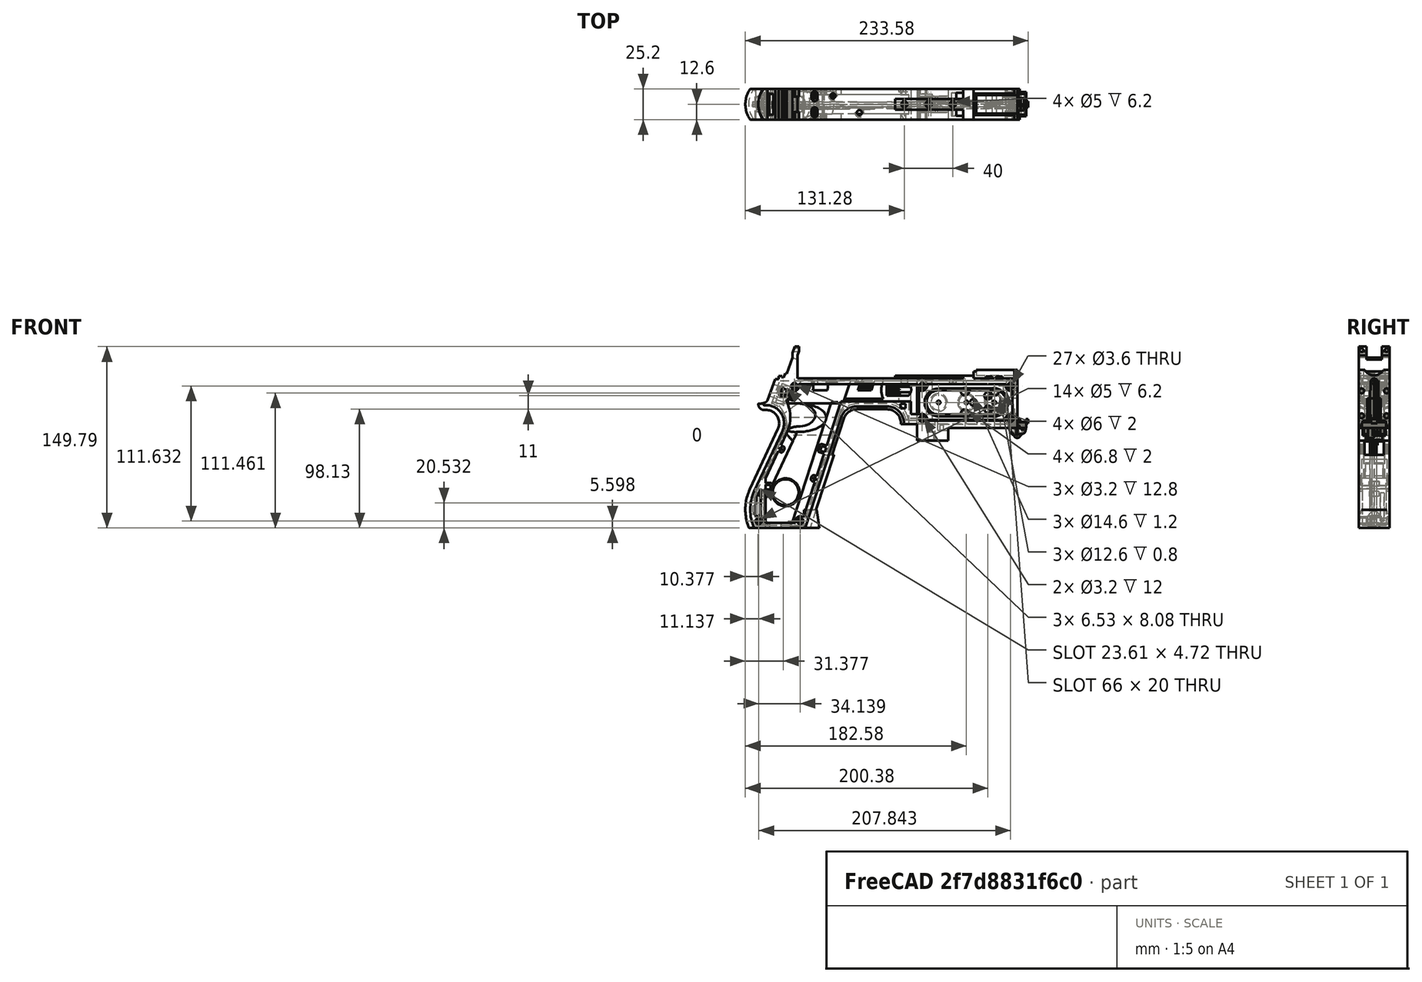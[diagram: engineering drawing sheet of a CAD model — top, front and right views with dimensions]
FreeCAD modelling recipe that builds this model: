
FCSTD DOCUMENT  (FreeCAD 1.0R39319 (Git))
Label: PICON-OF_ver_32
License: All rights reserved
LicenseURL: https://en.wikipedia.org/wiki/All_rights_reserved
objects: Sketcher::SketchObject×119, Part::Extrusion×75, Part::Cut×47, PartDesign::Pad×19, PartDesign::Chamfer×13, PartDesign::Pocket×12, PartDesign::Fillet×9, PartDesign::Body×8, Part::MultiFuse×6, PartDesign::SubtractivePipe×4, PartDesign::SubtractiveLoft×4, PartDesign::Plane×2, PartDesign::SubShapeBinder×2, Part::Part2DObjectPython×2, Part::Sweep×1, PartDesign::ShapeBinder×1, PartDesign::FeatureBase×1, Part::Cone×1, Part::Chamfer×1, Part::Mirroring×1, +1 more types
note: 570 computed .brp shape members not serialized (recipe doc carries the construction recipe); baked Part::Feature solids carry a one-line shape summary decoded from their .brp

FEATURE [Sketcher::SketchObject] Sketch  label="corpo principale"
  ArcFitTolerance = 1e-06
  AttacherType = Attacher::AttachEngine3D
  AttachmentSupport = -> [XZ_Plane]
  FullyConstrained = true
  MakeInternals = false
  MapMode = 5
  Placement = pos=(0,0,0) rot=(1,0,0;1.5708rad)
  sketch-geometry (65):
    g0: LineSegment StartX=0 StartY=0 StartZ=0 EndX=-57.2 EndY=0 EndZ=0
    g1: LineSegment StartX=-57.2 StartY=0 StartZ=0 EndX=-57.2 EndY=-10.4 EndZ=0
    g2: LineSegment StartX=-57.2 StartY=-10.4 StartZ=0 EndX=-82.8 EndY=-10.4 EndZ=0
    g3: LineSegment StartX=-82.8 StartY=-10.4 StartZ=0 EndX=-82.8 EndY=3.2 EndZ=0
    g4: LineSegment StartX=-82.8 StartY=3.2 StartZ=0 EndX=-93.6 EndY=3.2 EndZ=0
    g5: LineSegment StartX=-93.6 StartY=3.2 StartZ=0 EndX=-93.6 EndY=4 EndZ=0
    g6: LineSegment StartX=-107.6 StartY=18 StartZ=0 EndX=-132.428 EndY=18 EndZ=0
    g7: LineSegment StartX=-145.743 StartY=8.32624 StartZ=0 EndX=-175.232 EndY=-82.4316 EndZ=0
    g8: LineSegment StartX=-175.232 StartY=-82.4316 StartZ=0 EndX=-217.232 EndY=-82.4316 EndZ=0
    g9: LineSegment StartX=-217.232 StartY=-52.1862 StartZ=0 EndX=-193.988 EndY=-2.33927 EndZ=0
    g10: LineSegment StartX=-206.196 StartY=23.0857 StartZ=0 EndX=-199.861 EndY=40.4914 EndZ=0
    g11: LineSegment StartX=-199.861 StartY=40.4914 StartZ=0 EndX=-197.061 EndY=40.4914 EndZ=0
    g12: LineSegment StartX=-197.061 StartY=40.4914 StartZ=0 EndX=-197.061 EndY=42.8914 EndZ=0
    g13: LineSegment StartX=-197.061 StartY=42.8914 StartZ=0 EndX=-194.261 EndY=42.8914 EndZ=0
    g14: LineSegment StartX=-194.261 StartY=42.8914 StartZ=0 EndX=-194.535 EndY=42.1397 EndZ=0
    g15: LineSegment StartX=-194.535 StartY=42.1397 StartZ=0 EndX=-193.031 EndY=41.5924 EndZ=0
    g16: LineSegment StartX=-193.031 StartY=41.5924 StartZ=0 EndX=-191.663 EndY=45.3512 EndZ=0
    g17: LineSegment StartX=-191.663 StartY=45.3512 StartZ=0 EndX=-190.536 EndY=44.9408 EndZ=0
    g18: LineSegment StartX=-190.536 StartY=44.9408 StartZ=0 EndX=-185.747 EndY=58.0965 EndZ=0
    g19: LineSegment StartX=-185.747 StartY=58.0965 StartZ=0 EndX=-185.747 EndY=62.0965 EndZ=0
    g20: LineSegment StartX=-185.747 StartY=62.0965 StartZ=0 EndX=-183.832 EndY=67.3588 EndZ=0
    g21: LineSegment StartX=-183.832 StartY=67.3588 StartZ=0 EndX=-180.232 EndY=67.3588 EndZ=0
    g22: LineSegment StartX=-180.232 StartY=67.3588 StartZ=0 EndX=-180.232 EndY=63.7588 EndZ=0
    g23: LineSegment StartX=-180.232 StartY=63.7588 StartZ=0 EndX=-181.6 EndY=60 EndZ=0
    g24: LineSegment StartX=-181.6 StartY=60 StartZ=0 EndX=-181.6 EndY=41.2 EndZ=0
    g25: LineSegment StartX=-181.6 StartY=41.2 StartZ=0 EndX=-100.8 EndY=41.2 EndZ=0
    g26: LineSegment StartX=-36 StartY=43.2 StartZ=0 EndX=-36 EndY=41.2 EndZ=0
    g27: LineSegment StartX=0 StartY=48 StartZ=0 EndX=0 EndY=0 EndZ=0
    g28: LineSegment StartX=-209.901 StartY=19.85 StartZ=0 EndX=-209.901 EndY=20.1 EndZ=0
    g29: LineSegment StartX=-208.001 StartY=22 StartZ=0 EndX=-207.747 EndY=22 EndZ=0
    g30: LineSegment StartX=-207.583 StartY=19 StartZ=0 EndX=-209.051 EndY=19 EndZ=0
    g31: ArcOfCircle CenterX=-208.001 CenterY=20.1 CenterZ=0 NormalX=0 NormalY=0 NormalZ=1 AngleXU=0 Radius=1.9 StartAngle=1.5708 EndAngle=3.14159
    g32: GeomPoint [constr] X=-209.901 Y=22 Z=0
    g33: ArcOfCircle CenterX=-209.051 CenterY=19.85 CenterZ=0 NormalX=0 NormalY=0 NormalZ=1 AngleXU=0 Radius=0.85 StartAngle=3.14159 EndAngle=4.71239
    g34: GeomPoint [constr] X=-209.901 Y=19 Z=0
    g35: ArcOfCircle CenterX=-207.747 CenterY=23.65 CenterZ=0 NormalX=0 NormalY=0 NormalZ=1 AngleXU=0 Radius=1.65 StartAngle=4.71239 EndAngle=5.93412
    g36: GeomPoint [constr] X=-206.591 Y=22 Z=0
    g37: LineSegment StartX=-4 StartY=6 StartZ=0 EndX=-4 EndY=36.4 EndZ=0
    g38: LineSegment StartX=-4 StartY=36.4 StartZ=0 EndX=-185.2 EndY=36.4 EndZ=0
    g39: LineSegment StartX=-185.2 StartY=36.4 StartZ=0 EndX=-190.441 EndY=22 EndZ=0
    g40: LineSegment StartX=-214.575 StartY=-78.4316 StartZ=0 EndX=-178.142 EndY=-78.4316 EndZ=0
    g41: LineSegment StartX=-178.142 StartY=-78.4316 StartZ=0 EndX=-145.51 EndY=22 EndZ=0
    g42: LineSegment StartX=-145.51 StartY=22 StartZ=0 EndX=-87.91 EndY=22 EndZ=0
    g43: LineSegment StartX=-87.91 StartY=22 StartZ=0 EndX=-87.91 EndY=11.6 EndZ=0
    g44: LineSegment StartX=-87.91 StartY=11.6 StartZ=0 EndX=-80.11 EndY=11.6 EndZ=0
    g45: LineSegment StartX=-80.11 StartY=11.6 StartZ=0 EndX=-80.11 EndY=6 EndZ=0
    g46: LineSegment StartX=-80.11 StartY=6 StartZ=0 EndX=-4 EndY=6 EndZ=0
    g47: LineSegment StartX=-190.363 StartY=-4.02975 StartZ=0 EndX=-213.607 EndY=-53.8767 EndZ=0
    g48: ArcOfCircle CenterX=-132.428 CenterY=4 CenterZ=0 NormalX=0 NormalY=0 NormalZ=1 AngleXU=0 Radius=14 StartAngle=1.5708 EndAngle=2.82743
    g49: GeomPoint [constr] X=-142.6 Y=18 Z=0
    g50: ArcOfCircle CenterX=-107.6 CenterY=4 CenterZ=0 NormalX=0 NormalY=0 NormalZ=1 AngleXU=0 Radius=14 StartAngle=0 EndAngle=1.5708
    g51: GeomPoint [constr] X=-93.6 Y=18 Z=0
    g52: ArcOfCircle CenterX=-184.801 CenterY=-67.3089 CenterZ=0 NormalX=0 NormalY=0 NormalZ=1 AngleXU=0 Radius=35.7833 StartAngle=2.70526 EndAngle=3.57792
    g53: ArcOfCircle CenterX=-207.583 CenterY=4 CenterZ=0 NormalX=0 NormalY=0 NormalZ=1 AngleXU=0 Radius=15 StartAngle=5.84685 EndAngle=7.85398
    g54: LineSegment [constr] StartX=-213.607 StartY=-53.8767 StartZ=0 EndX=-217.232 EndY=-52.1862 EndZ=0
    g55: ArcOfCircle CenterX=-184.801 CenterY=-67.3089 CenterZ=0 NormalX=0 NormalY=0 NormalZ=1 AngleXU=0 Radius=31.7833 StartAngle=2.70526 EndAngle=3.49911
    g56: ArcOfCircle CenterX=-218.095 CenterY=8.90192 CenterZ=0 NormalX=0 NormalY=0 NormalZ=1 AngleXU=0 Radius=30.5989 StartAngle=5.84685 EndAngle=6.72553
    g57: LineSegment StartX=-44.6 StartY=43.2 StartZ=0 EndX=-36 EndY=43.2 EndZ=0
    g58: LineSegment StartX=-100.8 StartY=41.2 StartZ=0 EndX=-44.6 EndY=41.2 EndZ=0
    g59: LineSegment StartX=-44.6 StartY=41.2 StartZ=0 EndX=-44.6 EndY=43.2 EndZ=0
    g60: LineSegment StartX=-2.4 StartY=48 StartZ=0 EndX=0 EndY=48 EndZ=0
    g61: LineSegment StartX=-36 StartY=41.2 StartZ=0 EndX=-2.4 EndY=41.2 EndZ=0
    g62: LineSegment StartX=-2.4 StartY=41.2 StartZ=0 EndX=-2.4 EndY=48 EndZ=0
    g63: LineSegment [constr] StartX=-181.6 StartY=36.4 StartZ=0 EndX=-152.209 EndY=36.4 EndZ=0
    g64: LineSegment [constr] StartX=-181.6 StartY=36.4 StartZ=0 EndX=-130.41 EndY=36.4 EndZ=0
  constraints (183):
    c: Coincident(g-1,g0)
    c: PointOnObject(g0,g-1)
    c: Coincident(g0,g1)
    c: Vertical(g1)
    c: Coincident(g1,g2)
    c: Horizontal(g2)
    c: Coincident(g2,g3)
    c: Vertical(g3)
    c: Coincident(g3,g4)
    c: Coincident(g4,g5)
    c: Vertical(g5)
    c: Horizontal(g6)
    c: Coincident(g7,g8)
    c: Horizontal(g8)
    c: Coincident(g10,g11)
    c: Horizontal(g11)
    c: Coincident(g11,g12)
    c: Vertical(g12)
    c: Coincident(g12,g13)
    c: Horizontal(g13)
    c: Coincident(g13,g14)
    c: Coincident(g14,g15)
    c: Coincident(g15,g16)
    c: Coincident(g16,g17)
    c: Coincident(g17,g18)
    c: Coincident(g18,g19)
    c: Vertical(g19)
    c: Coincident(g19,g20)
    c: Coincident(g20,g21)
    c: Horizontal(g21)
    c: Coincident(g21,g22)
    c: Vertical(g22)
    c: Coincident(g22,g23)
    c: Coincident(g23,g24)
    c: Vertical(g24)
    c: Coincident(g24,g25)
    c: Horizontal(g25)
    c: Coincident(g57,g26)
    c: Vertical(g26)
    c: Coincident(g26,g61)
    c: PointOnObject(g60,g-2)
    c: Coincident(g60,g27)
    c: Coincident(g27,g0)
    c: DistanceY(g27,g27) = 48
    c: DistanceY(g1,g1) = 10.4
    c: DistanceX(g0,g0) = 57.2
    c: DistanceX(g2,g2) = 25.6
    c: Horizontal(g4)
    c: DistanceY(g3,g3) = 13.6
    c: DistanceX(g4,g4) = 10.8
    c: DistanceY(g5,g51) = 14.8
    c: DistanceX(g49,g51) = 49
    c: Distance(g7,g49) = 105.6
    c: DistanceX(g61,g60) = 36
    c: DistanceX(g25,g25) = 80.8
    c: DistanceY(g24,g24) = 18.8
    c: DistanceY(g22,g22) = 3.6
    c: Distance(g23) = 4
    c: Angle(g-1,g23) = 1.22173
    c: DistanceX(g21,g21) = 3.6
    c: Distance(g20) = 5.6
    c: Angle(g-1,g20) = 1.22173
    c: DistanceY(g19,g19) = 4
    c: Distance(g18) = 14
    c: Angle(g-1,g18) = 1.22173
    c: Distance(g17) = 1.2
    c: Distance(g16) = 4
    c: Angle(g16) = 1.22173
    c: Perpendicular(g18,g17)
    c: Distance(g15) = 1.6
    c: Perpendicular(g16,g15)
    c: Distance(g14) = 0.8
    c: DistanceX(g13,g13) = 2.8
    c: Perpendicular(g15,g14)
    c: DistanceY(g12,g12) = 2.4
    c: DistanceX(g11,g11) = 2.8
    c: Distance(g9) = 55
    c: Angle(g9,g-1) = 2.00713
    c: Horizontal(g29)
    c: Vertical(g28)
    c: Horizontal(g30)
    c: PointOnObject(g32,g29)
    c: PointOnObject(g32,g28)
    c: Tangent(g29,g31) = 1.5708
    c: Tangent(g28,g31) = 1.5708
    c: PointOnObject(g34,g28)
    c: PointOnObject(g34,g30)
    c: Tangent(g28,g33) = 1.5708
    c: Tangent(g30,g33) = 1.5708
    c: PointOnObject(g36,g29)
    c: PointOnObject(g36,g10)
    c: Tangent(g29,g35) = -1.5708
    c: Tangent(g10,g35) = -1.5708
    c: Angle(g-1,g10) = 1.22173
    c: Radius(g35) = 1.65
    c: Vertical(g37)
    c: Coincident(g37,g38)
    c: Horizontal(g38)
    c: Coincident(g38,g39)
    c: Horizontal(g40)
    c: Coincident(g40,g41)
    c: Coincident(g41,g42)
    c: Horizontal(g42)
    c: Coincident(g42,g43)
    c: Vertical(g43)
    c: Coincident(g43,g44)
    c: Horizontal(g44)
    c: Coincident(g44,g45)
    c: Vertical(g45)
    c: Coincident(g45,g46)
    c: Coincident(g46,g37)
    c: Horizontal(g46)
    c: DistanceY(g0,g37) = 6
    c: DistanceX(g37,g0) = 4
    c: DistanceY(g37,g25) = 4.8
    c: DistanceX(g38,g38) = 181.2
    c: DistanceX(g42,g42) = 57.6
    c: DistanceY(g49,g41) = 4
    c: DistanceX(g41,g49) = 2.91
    c: DistanceY(g43,g43) = 10.4
    c: DistanceX(g44,g44) = 7.8
    c: DistanceY(g7,g40) = 4
    c: Distance(g47) = 55
    c: Angle(g-1,g39) = 1.22173
    c: PointOnObject(g49,g7)
    c: PointOnObject(g49,g6)
    c: Tangent(g7,g48) = -1.5708
    c: Tangent(g6,g48) = -1.5708
    c: PointOnObject(g51,g5)
    c: PointOnObject(g51,g6)
    c: Tangent(g5,g50) = -1.5708
    c: Tangent(g6,g50) = -1.5708
    c: Radius(g50) = 14
    c: Radius(g48) = 14
    c: DistanceX(g8,g8) = 42
    c: Angle(g7,g-1) = 1.88496
    c: Parallel(g41,g7)
    c: Parallel(g47,g9)
    c: Coincident(g52,g8)
    c: Tangent(g52,g9) = 1.5708
    c: DistanceX(g9,g8) = 0
    c: Tangent(g53,g9) = -1.5708
    c: Tangent(g53,g30) = -1.5708
    c: Diameter(g53) = 30
    c: DistanceY(g53,g0) = -4
    c: Coincident(g54,g47)
    c: Distance(g54) = 4
    c: Coincident(g54,g9)
    c: Coincident(g55,g40)
    c: Tangent(g55,g47) = -1.5708
    c: Coincident(g52,g55)
    c: Coincident(g56,g39)
    c: Tangent(g56,g47) = 1.5708
    c: Horizontal(g57)
    c: DistanceX(g57,g57) = 8.6
    c: Coincident(g58,g25)
    c: Horizontal(g58)
    c: Coincident(g59,g58)
    c: Vertical(g59)
    c: DistanceY(g58,g57) = 2
    c: DistanceX(g58,g58) = 56.2
    c: Coincident(g59,g57)
    c: DistanceY(g41,g36) = 0
    c: DistanceY(g36,g39) = 0
    c: DistanceY(g28,g28) = 0.25
    c: DistanceX(g30,g36) = 2.46
    c: DistanceX(g28,g29) = 1.9
    c: Coincident(g62,g60)
    c: Horizontal(g60)
    c: DistanceX(g62,g27) = 2.4
    c: Coincident(g61,g62)
    c: DistanceY(g26,g26) = 2
    c: Vertical(g62)
    c: DistanceY(g61,g60) = 6.8
    c: Horizontal(g61)
    c: Distance(g63) = 29.391
    c: PointOnObject(g63,g38)
    c: PointOnObject(g63,g38)
    c: Distance(g64) = 51.19
    c: PointOnObject(g64,g38)
    c: PointOnObject(g64,g38)
    c: DistanceX(g24,g63) = 0
    c: DistanceX(g24,g64) = 0
FEATURE [Part::Extrusion] Extrude  label="Extrude corpo principale"
  Base = -> Sketch
  Dir = (0,-1,2e-16)
  DirMode = 2
  FaceMakerClass = Part::FaceMakerBullseye
  FaceMakerMode = 3
  LengthFwd = 25.2
  LengthRev = 12.6
  Solid = true
  Symmetric = true
FEATURE [Sketcher::SketchObject] Sketch002  label="scavo grilletto"
  ArcFitTolerance = 1e-06
  AttachmentSupport = -> [XZ_Plane]
  ExternalGeometry = -> [Sketch]
  FullyConstrained = true
  MakeInternals = false
  MapMode = 5
  Placement = pos=(0,0,0) rot=(1,0,0;1.5708rad)
  sketch-geometry (4):
    g0: LineSegment StartX=-89.51 StartY=22 StartZ=0 EndX=-152.71 EndY=22 EndZ=0
    g1: LineSegment StartX=-152.71 StartY=22 StartZ=0 EndX=-167.006 EndY=-22 EndZ=0
    g2: LineSegment StartX=-167.006 StartY=-22 StartZ=0 EndX=-89.51 EndY=-22 EndZ=0
    g3: LineSegment StartX=-89.51 StartY=-22 StartZ=0 EndX=-89.51 EndY=22 EndZ=0
  constraints (12):
    c: Horizontal(g0)
    c: Coincident(g0,g1)
    c: Coincident(g1,g2)
    c: Horizontal(g2)
    c: Coincident(g2,g3)
    c: Coincident(g3,g0)
    c: Vertical(g3)
    c: Angle(g1,g0) = 1.88496
    c: DistanceY(g3,g3) = 44
    c: DistanceX(g0,g0) = 63.2
    c: DistanceX(g0,g-3) = 1.6
    c: DistanceY(g-3,g0) = 0
FEATURE [Sketcher::SketchObject] Sketch004  label="traiettoria arrotondamento impugnatura anteriore"
  ArcFitTolerance = 1e-06
  AttachmentSupport = -> [XZ_Plane]
  ExternalGeometry = -> [Sketch]
  FullyConstrained = true
  MakeInternals = false
  MapMode = 5
  Placement = pos=(0,0,0) rot=(1,0,0;1.5708rad)
  sketch-geometry (13):
    g0: LineSegment StartX=-175.232 StartY=-82.4316 StartZ=0 EndX=-145.743 EndY=8.32624 EndZ=0
    g1: LineSegment StartX=-93.6 StartY=3.2 StartZ=0 EndX=-93.6 EndY=4 EndZ=0
    g2: LineSegment StartX=-132.428 StartY=18 StartZ=0 EndX=-107.6 EndY=18 EndZ=0
    g3: ArcOfCircle CenterX=-132.428 CenterY=4 CenterZ=0 NormalX=0 NormalY=0 NormalZ=1 AngleXU=0 Radius=14 StartAngle=1.5708 EndAngle=2.82743
    g4: ArcOfCircle CenterX=-107.6 CenterY=4 CenterZ=0 NormalX=0 NormalY=0 NormalZ=1 AngleXU=0 Radius=14 StartAngle=0 EndAngle=1.5708
    g5: LineSegment StartX=-175.232 StartY=-82.4316 StartZ=0 EndX=-217.232 EndY=-82.4316 EndZ=0
    g6: LineSegment StartX=-217.232 StartY=-52.1862 StartZ=0 EndX=-193.988 EndY=-2.33927 EndZ=0
    g7: LineSegment StartX=-209.051 StartY=19 StartZ=0 EndX=-207.583 EndY=19 EndZ=0
    g8: LineSegment StartX=-209.901 StartY=20.1 StartZ=0 EndX=-209.901 EndY=19.85 EndZ=0
    g9: ArcOfCircle CenterX=-184.801 CenterY=-67.3089 CenterZ=0 NormalX=0 NormalY=0 NormalZ=1 AngleXU=0 Radius=35.7833 StartAngle=2.70526 EndAngle=3.57792
    g10: ArcOfCircle CenterX=-207.583 CenterY=4 CenterZ=0 NormalX=0 NormalY=0 NormalZ=1 AngleXU=0 Radius=15 StartAngle=5.84685 EndAngle=7.85398
    g11: ArcOfCircle CenterX=-209.051 CenterY=19.85 CenterZ=0 NormalX=0 NormalY=0 NormalZ=1 AngleXU=0 Radius=0.85 StartAngle=3.14159 EndAngle=4.71239
    g12: ArcOfCircle CenterX=-208.001 CenterY=20.1 CenterZ=0 NormalX=0 NormalY=0 NormalZ=1 AngleXU=0 Radius=1.9 StartAngle=1.5708 EndAngle=3.14159
  constraints (26):
    c: Coincident(g0,g-3)
    c: Coincident(g0,g-6)
    c: Coincident(g1,g-8)
    c: Coincident(g1,g-7)
    c: Coincident(g2,g-5)
    c: Coincident(g2,g-4)
    c: Coincident(g3,g2)
    c: Tangent(g3,g0) = 1.5708
    c: Coincident(g4,g1)
    c: Tangent(g4,g2) = 1.5708
    c: Coincident(g5,g0)
    c: Coincident(g5,g-9)
    c: Coincident(g6,g-12)
    c: Coincident(g6,g-11)
    c: Coincident(g7,g-15)
    c: Coincident(g7,g-14)
    c: Coincident(g8,g-16)
    c: Coincident(g8,g-17)
    c: Tangent(g9,g6) = 1.5708
    c: Coincident(g9,g5)
    c: Coincident(g10,g7)
    c: Tangent(g10,g6) = -1.5708
    c: Tangent(g11,g7) = -1.5708
    c: Coincident(g11,g8)
    c: Tangent(g12,g8) = -1.5708
    c: Coincident(g12,g-17)
FEATURE [PartDesign::Plane] DatumPlane  label="Piano per disegno arrotondamento impugnatura"
  AttachmentSupport = -> [Sketch]
  Length = 68.5841
  MapMode = 7
  Placement = pos=(-145.743,1.8e-15,8.32624) rot=(0.154555,0.154555,0.97582;1.59527rad)
  ResizeMode = 0
  Width = 191.269
FEATURE [Sketcher::SketchObject] Sketch005  label="forma arrotondamento impugnatura anteriore"
  ArcFitTolerance = 1e-06
  AttachmentSupport = -> [DatumPlane]
  FullyConstrained = true
  MakeInternals = false
  MapMode = 5
  Placement = pos=(-145.743,1.8e-15,8.32624) rot=(0.154555,0.154555,0.97582;1.59527rad)
  sketch-geometry (5):
    g0: GeomPoint [constr] X=0 Y=-4 Z=0
    g1: GeomPoint [constr] X=-12.6 Y=7.1e-15 Z=0
    g2: GeomPoint [constr] X=12.6 Y=4.97e-14 Z=0
    g3: LineSegment StartX=-12.6 StartY=7.1e-15 StartZ=0 EndX=12.6 EndY=4.97e-14 EndZ=0
    g4: ArcOfCircle CenterX=-3.88e-14 CenterY=17.845 CenterZ=0 NormalX=0 NormalY=0 NormalZ=1 AngleXU=0 Radius=21.845 StartAngle=4.09759 EndAngle=5.32718
  constraints (11):
    c: DistanceY(g0,g-1) = 4
    c: DistanceX(g-1,g0) = 0
    c: DistanceX(g1,g-1) = 12.6
    c: DistanceX(g-1,g2) = 12.6
    c: DistanceY(g-1,g2) = 0
    c: DistanceY(g-1,g1) = 0
    c: Coincident(g3,g1)
    c: Coincident(g3,g2)
    c: Coincident(g4,g1)
    c: Coincident(g4,g2)
    c: PointOnObject(g0,g4)
FEATURE [Part::Sweep] Sweep  label="Sweep impugnatura"
  Frenet = true
  Sections = -> [Sketch005]
  Solid = true
  Spine = -> Sketch [Edge32,Edge33,Edge34,Edge35,Edge36,Edge37,Edge38,Edge39,Edge40,Edge41,Edge42,Edge43,Edge44]
  Transition = 1
FEATURE [Sketcher::SketchObject] Sketch008  label="buchi e pulizie varie"
  ArcFitTolerance = 1e-06
  AttachmentSupport = -> [XZ_Plane]
  ExternalGeometry = -> [Sketch]
  FullyConstrained = true
  MakeInternals = false
  MapMode = 5
  Placement = pos=(0,0,0) rot=(1,0,0;1.5708rad)
  sketch-geometry (26):
    g0: LineSegment StartX=-96.278 StartY=20.155 StartZ=0 EndX=-92.278 EndY=20.155 EndZ=0
    g1: LineSegment StartX=-92.278 StartY=20.155 StartZ=0 EndX=-92.278 EndY=16.155 EndZ=0
    g2: LineSegment StartX=-92.278 StartY=16.155 StartZ=0 EndX=-96.278 EndY=16.155 EndZ=0
    g3: LineSegment StartX=-96.278 StartY=16.155 StartZ=0 EndX=-96.278 EndY=20.155 EndZ=0
    g4: LineSegment StartX=-222.232 StartY=-82.4316 StartZ=0 EndX=-170.232 EndY=-82.4316 EndZ=0
    g5: LineSegment StartX=-170.232 StartY=-82.4316 StartZ=0 EndX=-170.232 EndY=-86.4316 EndZ=0
    g6: LineSegment StartX=-170.232 StartY=-86.4316 StartZ=0 EndX=-222.232 EndY=-86.4316 EndZ=0
    g7: LineSegment StartX=-222.232 StartY=-86.4316 StartZ=0 EndX=-222.232 EndY=-82.4316 EndZ=0
    g8: LineSegment StartX=-213.901 StartY=20.1 StartZ=0 EndX=-213.901 EndY=26 EndZ=0
    g9: LineSegment StartX=-213.901 StartY=26 StartZ=0 EndX=-206.196 EndY=26 EndZ=0
    g10: LineSegment StartX=-17.4 StartY=42.8 StartZ=0 EndX=-12.4 EndY=42.8 EndZ=0
    g11: LineSegment StartX=-12.4 StartY=42.8 StartZ=0 EndX=-12.4 EndY=41.2 EndZ=0
    g12: LineSegment StartX=-12.4 StartY=41.2 StartZ=0 EndX=-17.4 EndY=41.2 EndZ=0
    g13: LineSegment StartX=-17.4 StartY=41.2 StartZ=0 EndX=-17.4 EndY=42.8 EndZ=0
    g14: LineSegment StartX=-25.9 StartY=42.8 StartZ=0 EndX=-20.9 EndY=42.8 EndZ=0
    g15: LineSegment StartX=-20.9 StartY=42.8 StartZ=0 EndX=-20.9 EndY=41.2 EndZ=0
    g16: LineSegment StartX=-20.9 StartY=41.2 StartZ=0 EndX=-25.9 EndY=41.2 EndZ=0
    g17: LineSegment StartX=-25.9 StartY=41.2 StartZ=0 EndX=-25.9 EndY=42.8 EndZ=0
    g18: GeomPoint [constr] X=-206.196 Y=23.0857 Z=0
    g19: GeomPoint [constr] X=-213.901 Y=20.1 Z=0
    g20: BSplineCurve PolesCount=4 KnotsCount=2 Degree=3 IsPeriodic=0
    g21-g24: Circle [constr] x4 (B-spline internal-alignment scaffolding for g20; pole/knot coordinates omitted)
    g25: LineSegment StartX=-206.196 StartY=26 StartZ=0 EndX=-206.196 EndY=23.0857 EndZ=0
  constraints (73):
    c: Horizontal(g0)
    c: Coincident(g1,g0)
    c: Vertical(g1)
    c: Coincident(g2,g1)
    c: Horizontal(g2)
    c: Coincident(g3,g2)
    c: Coincident(g3,g0)
    c: Vertical(g3)
    c: DistanceX(g0,g-4) = 4.368
    c: DistanceY(g0,g-4) = 1.845
    c: DistanceY(g1,g1) = 4
    c: DistanceX(g2,g2) = 4
    c: Horizontal(g4)
    c: Coincident(g5,g4)
    c: Vertical(g5)
    c: Coincident(g6,g5)
    c: Horizontal(g6)
    c: Coincident(g7,g6)
    c: Coincident(g7,g4)
    c: Vertical(g7)
    c: DistanceY(g7,g7) = 4
    c: DistanceX(g4,g-5) = 5
    c: DistanceX(g-5,g4) = 5
    c: DistanceY(g4,g-5) = 0
    c: Coincident(g9,g8)
    c: Parallel(g9,g-6)
    c: DistanceX(g8,g-8) = 4
    c: Horizontal(g10)
    c: Coincident(g11,g10)
    c: Vertical(g11)
    c: Coincident(g12,g11)
    c: Horizontal(g12)
    c: Coincident(g13,g12)
    c: Coincident(g13,g10)
    c: Vertical(g13)
    c: Horizontal(g14)
    c: Coincident(g15,g14)
    c: Vertical(g15)
    c: Coincident(g16,g15)
    c: Horizontal(g16)
    c: Coincident(g17,g16)
    c: Coincident(g17,g14)
    c: Vertical(g17)
    c: DistanceY(g11,g10) = 1.6
    c: DistanceX(g10,g10) = 5
    c: DistanceY(g15,g14) = 1.6
    c: DistanceX(g14,g14) = 5
    c: DistanceX(g15,g12) = 3.5
    c: DistanceX(g11,g-9) = 10
    c: DistanceY(g-9,g11) = 0
    c: DistanceY(g-9,g15) = 0
    c: Perpendicular(g8,g9)
    c: DistanceY(g-7,g9) = 4
    c: DistanceY(g8,g-8) = 0
    c: InternalAlignment(g18,g20)
    c: InternalAlignment(g19,g20)
    c: InternalAlignment(g21,g20)
    c: Weight(g21) = 1
    c: InternalAlignment(g22,g20)
    c: Equal(g22,g21)
    c: InternalAlignment(g23,g20)
    c: Equal(g23,g21)
    c: InternalAlignment(g24,g20)
    c: Equal(g24,g21)
    c: Coincident(g18,g-12)
    c: Coincident(g19,g8)
    c: Coincident(g25,g9)
    c: Coincident(g25,g20)
    c: Vertical(g25)
    c: DistanceY(g20,g23) = 0
    c: DistanceY(g22,g18) = 2.26
    c: DistanceX(g22,g18) = 0.93
    c: DistanceX(g20,g23) = 2.9
FEATURE [Part::Extrusion] Extrude004  label="Extrude Buchi e pulizie varie"
  Base = -> Sketch008
  Dir = (0,-1,2e-16)
  DirMode = 2
  FaceMakerClass = Part::FaceMakerBullseye
  FaceMakerMode = 3
  LengthFwd = 25.2
  LengthRev = 0
  Solid = true
  Symmetric = true
FEATURE [Sketcher::SketchObject] Sketch009  label="rinforzi"
  ArcFitTolerance = 1e-06
  AttachmentSupport = -> [XZ_Plane]
  ExternalGeometry = -> [Sketch]
  FullyConstrained = true
  MakeInternals = false
  MapMode = 5
  Placement = pos=(0,0,0) rot=(1,0,0;1.5708rad)
  sketch-geometry (9):
    g0: LineSegment StartX=-87.91 StartY=22 StartZ=0 EndX=-87.91 EndY=36.4 EndZ=0
    g1: LineSegment StartX=-87.91 StartY=36.4 StartZ=0 EndX=-97.91 EndY=36.4 EndZ=0
    g2: LineSegment StartX=-97.91 StartY=36.4 StartZ=0 EndX=-97.91 EndY=22 EndZ=0
    g3: LineSegment StartX=-97.91 StartY=22 StartZ=0 EndX=-87.91 EndY=22 EndZ=0
    g4: LineSegment StartX=-149.713 StartY=9.06563 StartZ=0 EndX=-154.586 EndY=-5.93437 EndZ=0
    g5: LineSegment StartX=-154.586 StartY=-5.93437 StartZ=0 EndX=-191.863 EndY=-5.93437 EndZ=0
    g6: LineSegment StartX=-191.863 StartY=-5.93437 StartZ=0 EndX=-191.863 EndY=9.06563 EndZ=0
    g7: LineSegment StartX=-191.863 StartY=9.06563 StartZ=0 EndX=-149.713 EndY=9.06563 EndZ=0
    g8: LineSegment [constr] StartX=-145.51 StartY=22 StartZ=0 EndX=-149.713 EndY=9.06563 EndZ=0
  constraints (25):
    c: Vertical(g0)
    c: Coincident(g1,g0)
    c: Horizontal(g1)
    c: Coincident(g2,g1)
    c: Vertical(g2)
    c: Coincident(g3,g2)
    c: Coincident(g3,g0)
    c: Horizontal(g3)
    c: Coincident(g0,g-4)
    c: DistanceX(g3,g3) = 10
    c: DistanceY(g0,g-3) = 0
    c: Coincident(g5,g4)
    c: Horizontal(g5)
    c: Coincident(g6,g5)
    c: Vertical(g6)
    c: Coincident(g7,g6)
    c: Coincident(g7,g4)
    c: Horizontal(g7)
    c: Distance(g8) = 13.6
    c: Parallel(g-6,g8)
    c: Coincident(g-6,g8)
    c: Parallel(g4,g-6)
    c: DistanceY(g4,g4) = 15
    c: Coincident(g4,g8)
    c: DistanceX(g-5,g5) = -1.5
FEATURE [Part::Extrusion] Extrude001  label="Extrude scavo grilletto"
  Base = -> Sketch002
  Dir = (0,-1,2e-16)
  DirMode = 2
  FaceMakerClass = Part::FaceMakerBullseye
  FaceMakerMode = 3
  LengthFwd = 16
  LengthRev = 0
  Solid = true
  Symmetric = true
FEATURE [Part::Extrusion] Extrude005  label="Extrude Rinforzi"
  Base = -> Sketch009
  Dir = (0,-1,2e-16)
  DirMode = 2
  FaceMakerClass = Part::FaceMakerBullseye
  FaceMakerMode = 3
  LengthFwd = 2
  LengthRev = 0
  Placement = pos=(0,12.6,0) rot=(0,0,1;0rad)
  Solid = true
  Symmetric = false
FEATURE [PartDesign::ShapeBinder] CopyCut
  TraceSupport = false
FEATURE [PartDesign::Plane] DatumPlane001
  AttachmentSupport = -> [CopyCut]
  Length = 60
  MapMode = 5
  Placement = pos=(0,12.6,0) rot=(0,0.707107,0.707107;3.14159rad)
  ResizeMode = 0
  Width = 60
FEATURE [Sketcher::SketchObject] Sketch010  label="buco neopixel"
  ArcFitTolerance = 1e-06
  AttachmentSupport = -> [XZ_Plane]
  ExternalGeometry = -> [Sketch]
  FullyConstrained = true
  MakeInternals = false
  MapMode = 5
  Placement = pos=(0,0,0) rot=(1,0,0;1.5708rad)
  sketch-geometry (5):
    g0: LineSegment [constr] StartX=-199.861 StartY=40.4914 StartZ=0 EndX=-201.368 EndY=36.3521 EndZ=0
    g1: LineSegment StartX=-201.368 StartY=36.3521 StartZ=0 EndX=-204.932 EndY=26.5605 EndZ=0
    g2: LineSegment StartX=-201.368 StartY=36.3521 StartZ=0 EndX=-180.2 EndY=28.6477 EndZ=0
    g3: LineSegment StartX=-180.2 StartY=28.6477 StartZ=0 EndX=-183.764 EndY=18.8561 EndZ=0
    g4: LineSegment StartX=-183.764 StartY=18.8561 StartZ=0 EndX=-204.932 EndY=26.5605 EndZ=0
  constraints (14):
    c: Parallel(g0,g-3)
    c: Distance(g0) = 4.405
    c: Coincident(g0,g-3)
    c: Coincident(g2,g1)
    c: Coincident(g3,g2)
    c: Coincident(g4,g3)
    c: Coincident(g4,g1)
    c: Parallel(g1,g-3)
    c: Distance(g1) = 10.42
    c: Coincident(g1,g0)
    c: Parallel(g2,g4)
    c: Perpendicular(g1,g2)
    c: DistanceX(g-4,g2) = 5
    c: Parallel(g3,g1)
FEATURE [Part::Extrusion] Extrude006  label="Extrude buco neopixel"
  Base = -> Sketch010
  Dir = (0,-1,2e-16)
  DirMode = 2
  FaceMakerClass = Part::FaceMakerBullseye
  FaceMakerMode = 3
  LengthFwd = 17.2
  LengthRev = 0
  Solid = true
  Symmetric = true
FEATURE [Sketcher::SketchObject] Sketch011  label="fermo grilletto"
  ArcFitTolerance = 1e-06
  AttachmentSupport = -> [XZ_Plane]
  ExternalGeometry = -> [Sketch]
  FullyConstrained = true
  MakeInternals = false
  MapMode = 5
  Placement = pos=(0,0,0) rot=(1,0,0;1.5708rad)
  sketch-geometry (18):
    g0: LineSegment [constr] StartX=-145.51 StartY=22 StartZ=0 EndX=-157.347 EndY=-14.4293 EndZ=0
    g1: LineSegment [constr] StartX=-157.347 StartY=-14.4293 StartZ=0 EndX=-157.841 EndY=-15.951 EndZ=0
    g2: LineSegment StartX=-161.151 StartY=-13.1932 StartZ=0 EndX=-155.825 EndY=-14.9237 EndZ=0
    g3: LineSegment StartX=-163.167 StartY=-14.2205 StartZ=0 EndX=-164.403 EndY=-18.0247 EndZ=0
    g4: LineSegment StartX=-163.376 StartY=-20.0408 StartZ=0 EndX=-158.05 EndY=-21.7713 EndZ=0
    g5: LineSegment StartX=-158.05 StartY=-21.7713 StartZ=0 EndX=-155.825 EndY=-14.9237 EndZ=0
    g6: LineSegment StartX=-161.645 StartY=-14.7149 StartZ=0 EndX=-157.841 EndY=-15.951 EndZ=0
    g7: LineSegment StartX=-157.841 StartY=-15.951 StartZ=0 EndX=-159.077 EndY=-19.7552 EndZ=0
    g8: LineSegment StartX=-159.077 StartY=-19.7552 StartZ=0 EndX=-162.881 EndY=-18.5191 EndZ=0
    g9: LineSegment StartX=-162.881 StartY=-18.5191 StartZ=0 EndX=-161.645 EndY=-14.7149 EndZ=0
    g10: LineSegment [constr] StartX=-161.645 StartY=-14.7149 StartZ=0 EndX=-161.151 EndY=-13.1932 EndZ=0
    g11: LineSegment [constr] StartX=-159.077 StartY=-19.7552 StartZ=0 EndX=-157.555 EndY=-20.2496 EndZ=0
    g12: LineSegment [constr] StartX=-159.077 StartY=-19.7552 StartZ=0 EndX=-159.572 EndY=-21.2769 EndZ=0
    g13: LineSegment [constr] StartX=-161.645 StartY=-14.7149 StartZ=0 EndX=-163.167 EndY=-14.2205 EndZ=0
    g14: ArcOfCircle CenterX=-161.645 CenterY=-14.7149 CenterZ=0 NormalX=0 NormalY=0 NormalZ=1 AngleXU=0 Radius=1.6 StartAngle=1.25664 EndAngle=2.82743
    g15: GeomPoint [constr] X=-162.673 Y=-12.6988 Z=0
    g16: ArcOfCircle CenterX=-162.881 CenterY=-18.5191 CenterZ=0 NormalX=0 NormalY=0 NormalZ=1 AngleXU=0 Radius=1.6 StartAngle=2.82743 EndAngle=4.39823
    g17: GeomPoint [constr] X=-164.897 Y=-19.5464 Z=0
  constraints (48):
    c: Parallel(g0,g-3)
    c: Distance(g0) = 38.304
    c: Coincident(g0,g-3)
    c: Parallel(g1,g-3)
    c: Distance(g1) = 1.6
    c: Coincident(g1,g0)
    c: Coincident(g5,g4)
    c: Coincident(g5,g2)
    c: Coincident(g7,g6)
    c: Coincident(g8,g7)
    c: Coincident(g9,g8)
    c: Coincident(g9,g6)
    c: Parallel(g7,g-3)
    c: Parallel(g9,g7)
    c: Perpendicular(g6,g7)
    c: Parallel(g6,g8)
    c: Distance(g6) = 4
    c: Distance(g9) = 4
    c: Parallel(g5,g7)
    c: Parallel(g9,g3)
    c: Parallel(g2,g6)
    c: Parallel(g4,g8)
    c: Parallel(g13,g6)
    c: Parallel(g10,g9)
    c: Parallel(g11,g8)
    c: Parallel(g12,g7)
    c: Distance(g10) = 1.6
    c: Distance(g13) = 1.6
    c: Distance(g12) = 1.6
    c: Distance(g11) = 1.6
    c: Coincident(g10,g6)
    c: Coincident(g13,g6)
    c: Coincident(g12,g7)
    c: Coincident(g11,g7)
    c: Distance(g10,g15) = 1.6
    c: Distance(g15,g13) = 1.6
    c: Distance(g4,g12) = 1.6
    c: Distance(g4,g11) = 1.6
    c: PointOnObject(g15,g2)
    c: Tangent(g3,g14) = -1.5708
    c: Tangent(g2,g14) = 1.5708
    c: PointOnObject(g17,g4)
    c: PointOnObject(g17,g3)
    c: Tangent(g4,g16) = -1.5708
    c: Tangent(g3,g16) = -1.5708
    c: Equal(g16,g14)
    c: Coincident(g16,g8)
    c: Coincident(g6,g1)
FEATURE [Part::Extrusion] Extrude007  label="Extrude fermo grilletto"
  Base = -> Sketch011
  Dir = (0,-1,2e-16)
  DirMode = 2
  FaceMakerClass = Part::FaceMakerBullseye
  FaceMakerMode = 3
  LengthFwd = 25.2
  LengthRev = 0
  Solid = true
  Symmetric = true
FEATURE [Sketcher::SketchObject] Sketch012  label="buco oled"
  ArcFitTolerance = 1e-06
  AttachmentSupport = -> [XZ_Plane]
  ExternalGeometry = -> [Sketch]
  FullyConstrained = true
  MakeInternals = false
  MapMode = 5
  Placement = pos=(0,0,0) rot=(1,0,0;1.5708rad)
  sketch-geometry (4):
    g0: LineSegment StartX=-185.747 StartY=58.0965 StartZ=0 EndX=-180.232 EndY=56.0891 EndZ=0
    g1: LineSegment StartX=-185.747 StartY=58.0965 StartZ=0 EndX=-185.747 EndY=67.3588 EndZ=0
    g2: LineSegment StartX=-185.747 StartY=67.3588 StartZ=0 EndX=-180.232 EndY=67.3588 EndZ=0
    g3: LineSegment StartX=-180.232 StartY=67.3588 StartZ=0 EndX=-180.232 EndY=56.0891 EndZ=0
  constraints (10):
    c: Coincident(g1,g0)
    c: Coincident(g2,g1)
    c: Coincident(g3,g2)
    c: Coincident(g3,g0)
    c: Parallel(g1,g-5)
    c: Perpendicular(g-3,g0)
    c: Parallel(g2,g-6)
    c: Parallel(g3,g-4)
    c: Coincident(g0,g-5)
    c: Coincident(g2,g-6)
FEATURE [Part::Extrusion] Extrude008  label="Extrude buco oled"
  Base = -> Sketch012
  Dir = (0,-1,2e-16)
  DirMode = 2
  FaceMakerClass = Part::FaceMakerBullseye
  FaceMakerMode = 3
  LengthFwd = 12.8
  LengthRev = 0
  Solid = true
  Symmetric = true
FEATURE [Sketcher::SketchObject] Sketch013  label="buco pompa"
  ArcFitTolerance = 1e-06
  AttachmentSupport = -> [XZ_Plane]
  ExternalGeometry = -> [Sketch]
  FullyConstrained = true
  MakeInternals = false
  MapMode = 5
  Placement = pos=(0,0,0) rot=(1,0,0;1.5708rad)
  sketch-geometry (8):
    g0: LineSegment StartX=-82.8 StartY=-10.4 StartZ=0 EndX=-82.8 EndY=-9.6 EndZ=0
    g1: LineSegment StartX=-82.8 StartY=-9.6 StartZ=0 EndX=-67.9 EndY=-9.6 EndZ=0
    g2: LineSegment StartX=-67.9 StartY=-9.6 StartZ=0 EndX=-67.9 EndY=6 EndZ=0
    g3: LineSegment StartX=-67.9 StartY=6 StartZ=0 EndX=-65.9 EndY=6 EndZ=0
    g4: LineSegment StartX=-65.9 StartY=6 StartZ=0 EndX=-65.9 EndY=-1.7 EndZ=0
    g5: LineSegment StartX=-65.9 StartY=-1.7 StartZ=0 EndX=-57.2 EndY=-1.7 EndZ=0
    g6: LineSegment StartX=-57.2 StartY=-1.7 StartZ=0 EndX=-57.2 EndY=-10.4 EndZ=0
    g7: LineSegment StartX=-57.2 StartY=-10.4 StartZ=0 EndX=-82.8 EndY=-10.4 EndZ=0
  constraints (22):
    c: Vertical(g0)
    c: Coincident(g1,g0)
    c: Horizontal(g1)
    c: Coincident(g2,g1)
    c: Vertical(g2)
    c: Coincident(g3,g2)
    c: Horizontal(g3)
    c: Coincident(g4,g3)
    c: Vertical(g4)
    c: Coincident(g5,g4)
    c: Horizontal(g5)
    c: Coincident(g6,g5)
    c: Vertical(g6)
    c: Coincident(g7,g6)
    c: Coincident(g7,g0)
    c: DistanceY(g0,g0) = 0.8
    c: DistanceY(g6,g6) = 8.7
    c: DistanceX(g1,g1) = 14.9
    c: DistanceX(g3,g3) = 2
    c: Coincident(g0,g-4)
    c: DistanceY(g2,g-6) = 0
    c: Coincident(g6,g-5)
FEATURE [Part::Extrusion] Extrude009  label="Extrude buco pompa"
  Base = -> Sketch013
  Dir = (0,-1,2e-16)
  DirMode = 2
  FaceMakerClass = Part::FaceMakerBullseye
  FaceMakerMode = 3
  LengthFwd = 13.2
  LengthRev = 0
  Solid = true
  Symmetric = true
FEATURE [Sketcher::SketchObject] Sketch014  label="buco frontale"
  ArcFitTolerance = 1e-06
  AttachmentSupport = -> [XZ_Plane]
  ExternalGeometry = -> [Sketch]
  FullyConstrained = true
  MakeInternals = false
  MapMode = 5
  Placement = pos=(0,0,0) rot=(1,0,0;1.5708rad)
  sketch-geometry (10):
    g0: LineSegment StartX=0 StartY=0 StartZ=0 EndX=0 EndY=24.671 EndZ=0
    g1: LineSegment StartX=0 StartY=24.671 StartZ=0 EndX=-4 EndY=24.671 EndZ=0
    g2: LineSegment StartX=-4 StartY=24.671 StartZ=0 EndX=-4 EndY=16 EndZ=0
    g3: LineSegment StartX=-4 StartY=16 StartZ=0 EndX=-2.4 EndY=16 EndZ=0
    g4: LineSegment StartX=-2.4 StartY=16 StartZ=0 EndX=-2.4 EndY=10 EndZ=0
    g5: LineSegment StartX=-2.4 StartY=10 StartZ=0 EndX=-12 EndY=10 EndZ=0
    g6: LineSegment StartX=-12 StartY=10 StartZ=0 EndX=-12 EndY=6 EndZ=0
    g7: LineSegment StartX=-12 StartY=6 StartZ=0 EndX=-2.4 EndY=6 EndZ=0
    g8: LineSegment StartX=-2.4 StartY=6 StartZ=0 EndX=-2.4 EndY=0 EndZ=0
    g9: LineSegment StartX=-2.4 StartY=0 StartZ=0 EndX=0 EndY=0 EndZ=0
  constraints (29):
    c: Vertical(g0)
    c: Coincident(g1,g0)
    c: Horizontal(g1)
    c: Coincident(g2,g1)
    c: Vertical(g2)
    c: Coincident(g3,g2)
    c: Horizontal(g3)
    c: Coincident(g4,g3)
    c: Vertical(g4)
    c: Coincident(g5,g4)
    c: Horizontal(g5)
    c: Coincident(g6,g5)
    c: Vertical(g6)
    c: Coincident(g7,g6)
    c: Coincident(g8,g7)
    c: Vertical(g8)
    c: Coincident(g9,g8)
    c: Coincident(g9,g0)
    c: Horizontal(g9)
    c: DistanceY(g0,g0) = 24.671
    c: Horizontal(g7)
    c: DistanceY(g6,g6) = 4
    c: DistanceY(g4,g4) = 6
    c: DistanceX(g9,g9) = 2.4
    c: Coincident(g0,g-1)
    c: DistanceY(g-3,g7) = 0
    c: DistanceX(g8,g4) = 0
    c: DistanceX(g-3,g1) = 0
    c: DistanceX(g6,g-3) = 8
FEATURE [Part::Extrusion] Extrude010  label="Extrude buco frontale"
  Base = -> Sketch014
  Dir = (0,-1,2e-16)
  DirMode = 2
  FaceMakerClass = Part::FaceMakerBullseye
  FaceMakerMode = 3
  LengthFwd = 11.2
  LengthRev = 0
  Solid = true
  Symmetric = true
FEATURE [Sketcher::SketchObject] Sketch015  label="guida rail"
  ArcFitTolerance = 1e-06
  AttachmentSupport = -> [XZ_Plane]
  ExternalGeometry = -> [Sketch]
  FullyConstrained = true
  MakeInternals = false
  MapMode = 5
  Placement = pos=(0,0,0) rot=(1,0,0;1.5708rad)
  sketch-geometry (4):
    g0: LineSegment StartX=-100.8 StartY=43.2 StartZ=0 EndX=-44.6 EndY=43.2 EndZ=0
    g1: LineSegment StartX=-44.6 StartY=43.2 StartZ=0 EndX=-44.6 EndY=41.2 EndZ=0
    g2: LineSegment StartX=-44.6 StartY=41.2 StartZ=0 EndX=-100.8 EndY=41.2 EndZ=0
    g3: LineSegment StartX=-100.8 StartY=41.2 StartZ=0 EndX=-100.8 EndY=43.2 EndZ=0
  constraints (9):
    c: Horizontal(g0)
    c: Coincident(g1,g0)
    c: Coincident(g2,g1)
    c: Coincident(g3,g2)
    c: Coincident(g3,g0)
    c: Vertical(g3)
    c: Coincident(g2,g-3)
    c: Coincident(g1,g-3)
    c: Coincident(g0,g-4)
FEATURE [Part::Extrusion] Extrude011  label="Extrude guida rail"
  Base = -> Sketch015
  Dir = (0,-1,2e-16)
  DirMode = 2
  FaceMakerClass = Part::FaceMakerBullseye
  FaceMakerMode = 3
  LengthFwd = 9
  LengthRev = 0
  Solid = true
  Symmetric = true
FEATURE [Sketcher::SketchObject] Sketch016  label="guide per coperture laterali"
  ArcFitTolerance = 1e-06
  AttachmentSupport = -> [XZ_Plane]
  ExternalGeometry = -> [Sketch]
  FullyConstrained = true
  MakeInternals = false
  MapMode = 5
  Placement = pos=(0,0,0) rot=(1,0,0;1.5708rad)
  sketch-geometry (14):
    g0: Circle CenterX=-5.6 CenterY=7.6 CenterZ=0 NormalX=0 NormalY=0 NormalZ=1 AngleXU=0 Radius=1.6
    g1: Circle CenterX=-5.6 CenterY=7.6 CenterZ=0 NormalX=0 NormalY=0 NormalZ=1 AngleXU=0 Radius=4
    g2: Circle CenterX=-5.6 CenterY=34.8 CenterZ=0 NormalX=0 NormalY=0 NormalZ=1 AngleXU=0 Radius=1.6
    g3: Circle CenterX=-5.6 CenterY=34.8 CenterZ=0 NormalX=0 NormalY=0 NormalZ=1 AngleXU=0 Radius=4
    g4: Circle CenterX=-184.08 CenterY=34.8 CenterZ=0 NormalX=0 NormalY=0 NormalZ=1 AngleXU=0 Radius=1.6
    g5: Circle CenterX=-184.08 CenterY=34.8 CenterZ=0 NormalX=0 NormalY=0 NormalZ=1 AngleXU=0 Radius=4
    g6: Circle CenterX=-179.305 CenterY=-76.8316 CenterZ=0 NormalX=0 NormalY=0 NormalZ=1 AngleXU=0 Radius=1.6
    g7: Circle CenterX=-179.305 CenterY=-76.8316 CenterZ=0 NormalX=0 NormalY=0 NormalZ=1 AngleXU=0 Radius=4
    g8: Circle CenterX=-213.443 CenterY=-76.8316 CenterZ=0 NormalX=0 NormalY=0 NormalZ=1 AngleXU=0 Radius=1.6
    g9: Circle CenterX=-213.443 CenterY=-76.8316 CenterZ=0 NormalX=0 NormalY=0 NormalZ=1 AngleXU=0 Radius=4
    g10: Circle CenterX=-78.51 CenterY=7.6 CenterZ=0 NormalX=0 NormalY=0 NormalZ=1 AngleXU=0 Radius=1.6
    g11: Circle CenterX=-78.51 CenterY=7.6 CenterZ=0 NormalX=0 NormalY=0 NormalZ=1 AngleXU=0 Radius=4
    g12: Circle CenterX=-78.51 CenterY=34.8 CenterZ=0 NormalX=0 NormalY=0 NormalZ=1 AngleXU=0 Radius=1.6
    g13: Circle CenterX=-78.51 CenterY=34.8 CenterZ=0 NormalX=0 NormalY=0 NormalZ=1 AngleXU=0 Radius=4
  constraints (35):
    c: Diameter(g0) = 3.2
    c: Diameter(g1) = 8
    c: Coincident(g0,g1)
    c: Diameter(g2) = 3.2
    c: Diameter(g3) = 8
    c: Coincident(g3,g2)
    c: Tangent(g2,g-7)
    c: Diameter(g4) = 3.2
    c: Diameter(g5) = 8
    c: Coincident(g5,g4)
    c: Tangent(g4,g-7)
    c: Tangent(g4,g-8)
    c: Diameter(g6) = 3.2
    c: Diameter(g7) = 8
    c: Coincident(g7,g6)
    c: Tangent(g6,g-9)
    c: Tangent(g6,g-10)
    c: Diameter(g8) = 3.2
    c: Diameter(g9) = 8
    c: Coincident(g9,g8)
    c: Tangent(g8,g-10)
    c: Tangent(g8,g-11)
    c: Diameter(g10) = 3.2
    c: Diameter(g11) = 8
    c: Diameter(g12) = 3.2
    c: Diameter(g13) = 8
    c: Coincident(g12,g13)
    c: Coincident(g10,g11)
    c: Tangent(g12,g-7)
    c: DistanceX(g12,g10) = 0
    c: Tangent(g2,g-6)
    c: Tangent(g0,g-6)
    c: Tangent(g0,g-3)
    c: Tangent(g10,g-3)
    c: Tangent(g10,g-4)
FEATURE [Part::Extrusion] Extrude012  label="extrude guide per coperture laterali"
  Base = -> Sketch016
  Dir = (0,-1,2e-16)
  DirMode = 2
  FaceMakerClass = Part::FaceMakerBullseye
  FaceMakerMode = 3
  LengthFwd = 25.2
  LengthRev = 0
  Solid = true
  Symmetric = true
FEATURE [Sketcher::SketchObject] Sketch017  label="supporto CAM"
  ArcFitTolerance = 1e-06
  AttachmentSupport = -> [XZ_Plane]
  ExternalGeometry = -> [Sketch]
  FullyConstrained = true
  MakeInternals = false
  MapMode = 5
  Placement = pos=(0,0,0) rot=(1,0,0;1.5708rad)
  sketch-geometry (6):
    g0: LineSegment StartX=-2.4 StartY=48 StartZ=0 EndX=-2.4 EndY=41.2 EndZ=0
    g1: LineSegment StartX=-2.4 StartY=48 StartZ=0 EndX=-34 EndY=48 EndZ=0
    g2: LineSegment StartX=-34 StartY=48 StartZ=0 EndX=-34 EndY=46.72 EndZ=0
    g3: LineSegment StartX=-34 StartY=46.72 StartZ=0 EndX=-36 EndY=46.72 EndZ=0
    g4: LineSegment StartX=-36 StartY=46.72 StartZ=0 EndX=-36 EndY=41.2 EndZ=0
    g5: LineSegment StartX=-36 StartY=41.2 StartZ=0 EndX=-2.4 EndY=41.2 EndZ=0
  constraints (15):
    c: Coincident(g1,g0)
    c: Horizontal(g1)
    c: Coincident(g2,g1)
    c: Vertical(g2)
    c: Coincident(g3,g2)
    c: Horizontal(g3)
    c: Coincident(g4,g3)
    c: Coincident(g5,g4)
    c: DistanceX(g1,g0) = 31.6
    c: Coincident(g5,g0)
    c: Vertical(g4)
    c: DistanceY(g2,g1) = 1.28
    c: Coincident(g0,g-3)
    c: Coincident(g0,g-3)
    c: Coincident(g4,g-4)
FEATURE [Part::Extrusion] Extrude013  label="Extrude supporto CAM"
  Base = -> Sketch017
  Dir = (0,-1,2e-16)
  DirMode = 2
  FaceMakerClass = Part::FaceMakerBullseye
  FaceMakerMode = 3
  LengthFwd = 17.8
  LengthRev = 0
  Solid = true
  Symmetric = true
FEATURE [Sketcher::SketchObject] Sketch018  label="Scavo CAM"
  ArcFitTolerance = 1e-06
  AttachmentSupport = -> [YZ_Plane]
  ExternalGeometry = -> [Sketch]
  FullyConstrained = true
  MakeInternals = false
  MapMode = 5
  Placement = pos=(0,0,0) rot=(0.57735,0.57735,0.57735;2.0944rad)
  sketch-geometry (4):
    g0: LineSegment StartX=-7.73 StartY=48 StartZ=0 EndX=7.73 EndY=48 EndZ=0
    g1: LineSegment [constr] StartX=1.07e-14 StartY=48 StartZ=0 EndX=0 EndY=43.5155 EndZ=0
    g2: ArcOfCircle CenterX=9e-15 CenterY=52.42 CenterZ=0 NormalX=0 NormalY=0 NormalZ=1 AngleXU=0 Radius=8.90445 StartAngle=3.66102 EndAngle=5.76376
    g3: Circle [constr] CenterX=9e-15 CenterY=52.42 CenterZ=0 NormalX=0 NormalY=0 NormalZ=1 AngleXU=0 Radius=8.9
  constraints (13):
    c: Horizontal(g0)
    c: DistanceY(g-3,g0) = 0
    c: DistanceX(g0,g0) = 15.46
    c: DistanceX(g0,g-3) = 7.73
    c: DistanceX(g-3) = 0
    c: Coincident(g1,g-3)
    c: PointOnObject(g1,g-2)
    c: Coincident(g2,g0)
    c: Coincident(g2,g0)
    c: PointOnObject(g1,g2)
    c: Diameter(g3) = 17.8
    c: DistanceY(g1,g3) = 4.42
    c: Coincident(g2,g3)
FEATURE [Part::Extrusion] Extrude014  label="Extrude Scavo CAM"
  Base = -> Sketch018
  Dir = (1,0,0)
  DirMode = 2
  FaceMakerClass = Part::FaceMakerBullseye
  FaceMakerMode = 3
  LengthFwd = -34
  LengthRev = 0
  Solid = true
  Symmetric = false
FEATURE [Sketcher::SketchObject] Sketch019  label="scavo rumble"
  ArcFitTolerance = 1e-06
  AttachmentSupport = -> [XZ_Plane]
  ExternalGeometry = -> [Sketch]
  FullyConstrained = true
  MakeInternals = false
  MapMode = 5
  Placement = pos=(0,0,0) rot=(1,0,0;1.5708rad)
  sketch-geometry (6):
    g0: LineSegment StartX=-164.575 StartY=-24.3786 StartZ=0 EndX=-159.439 EndY=-26.0473 EndZ=0
    g1: LineSegment StartX=-159.439 StartY=-26.0473 StartZ=0 EndX=-166.547 EndY=-47.9216 EndZ=0
    g2: LineSegment StartX=-166.547 StartY=-47.9216 StartZ=0 EndX=-171.682 EndY=-46.2529 EndZ=0
    g3: LineSegment StartX=-171.682 StartY=-46.2529 StartZ=0 EndX=-164.575 EndY=-24.3786 EndZ=0
    g4: LineSegment [constr] StartX=-145.51 StartY=22 StartZ=0 EndX=-160.961 EndY=-25.5528 EndZ=0
    g5: LineSegment [constr] StartX=-159.439 StartY=-26.0473 StartZ=0 EndX=-160.961 EndY=-25.5528 EndZ=0
  constraints (17):
    c: Coincident(g1,g0)
    c: Coincident(g2,g1)
    c: Coincident(g3,g2)
    c: Coincident(g3,g0)
    c: Parallel(g3,g-3)
    c: Parallel(g3,g1)
    c: Perpendicular(g3,g0)
    c: Perpendicular(g2,g3)
    c: Distance(g2,g0) = 23
    c: Parallel(g4,g-3)
    c: Distance(g4) = 50
    c: Coincident(g4,g-3)
    c: Parallel(g5,g0)
    c: Distance(g5) = 1.6
    c: Coincident(g5,g0)
    c: Distance(g5,g0) = 3.8
    c: Coincident(g5,g4)
FEATURE [Part::Extrusion] Extrude015  label="scavo rumble001"
  Base = -> Sketch019
  Dir = (0,-1,2e-16)
  DirMode = 2
  FaceMakerClass = Part::FaceMakerBullseye
  FaceMakerMode = 3
  LengthFwd = 21
  LengthRev = 0
  Solid = true
  Symmetric = true
FEATURE [Sketcher::SketchObject] Sketch020  label="fermo rumble"
  ArcFitTolerance = 1e-06
  AttachmentSupport = -> [XZ_Plane]
  ExternalGeometry = -> [Sketch019,Sketch]
  FullyConstrained = true
  MakeInternals = false
  MapMode = 5
  Placement = pos=(0,0,0) rot=(1,0,0;1.5708rad)
  sketch-geometry (16):
    g0: LineSegment [constr] StartX=-166.709 StartY=-43.2425 StartZ=0 EndX=-168.068 EndY=-47.4271 EndZ=0
    g1: LineSegment [constr] StartX=-168.068 StartY=-47.4271 StartZ=0 EndX=-166.547 EndY=-47.9216 EndZ=0
    g2: LineSegment StartX=-168.121 StartY=-40.4703 StartZ=0 EndX=-166.029 EndY=-41.1502 EndZ=0
    g3: LineSegment StartX=-166.029 StartY=-41.1502 StartZ=0 EndX=-166.709 EndY=-43.2425 EndZ=0
    g4: LineSegment StartX=-166.709 StartY=-43.2425 StartZ=0 EndX=-168.801 EndY=-42.5626 EndZ=0
    g5: LineSegment StartX=-168.801 StartY=-42.5626 StartZ=0 EndX=-168.121 EndY=-40.4703 EndZ=0
    g6: LineSegment StartX=-167.627 StartY=-38.9486 StartZ=0 EndX=-164.203 EndY=-40.0611 EndZ=0
    g7: LineSegment StartX=-164.203 StartY=-40.0611 StartZ=0 EndX=-165.81 EndY=-45.0066 EndZ=0
    g8: LineSegment StartX=-165.81 StartY=-45.0066 StartZ=0 EndX=-169.234 EndY=-43.8941 EndZ=0
    g9: LineSegment StartX=-170.261 StartY=-41.878 StartZ=0 EndX=-169.643 EndY=-39.9759 EndZ=0
    g10: LineSegment [constr] StartX=-169.643 StartY=-39.9759 StartZ=0 EndX=-169.148 EndY=-38.4542 EndZ=0
    g11: LineSegment [constr] StartX=-169.148 StartY=-38.4542 StartZ=0 EndX=-167.627 EndY=-38.9486 EndZ=0
    g12: ArcOfCircle CenterX=-168.739 CenterY=-42.3724 CenterZ=0 NormalX=0 NormalY=0 NormalZ=1 AngleXU=0 Radius=1.6 StartAngle=2.82743 EndAngle=4.39823
    g13: GeomPoint [constr] X=-170.755 Y=-43.3997 Z=0
    g14: ArcOfCircle CenterX=-168.121 CenterY=-40.4703 CenterZ=0 NormalX=0 NormalY=0 NormalZ=1 AngleXU=0 Radius=1.6 StartAngle=1.25664 EndAngle=2.82743
    g15: GeomPoint [constr] X=-169.148 Y=-38.4542 Z=0
  constraints (42):
    c: Parallel(g0,g-4)
    c: Distance(g0) = 4.4
    c: Coincident(g1,g0)
    c: Perpendicular(g0,g1)
    c: Distance(g1) = 1.6
    c: Coincident(g1,g-5)
    c: Coincident(g3,g2)
    c: Coincident(g4,g3)
    c: Coincident(g5,g4)
    c: Coincident(g5,g2)
    c: Parallel(g3,g-4)
    c: Parallel(g3,g5)
    c: Perpendicular(g2,g3)
    c: Parallel(g4,g2)
    c: Distance(g2) = 2.2
    c: Distance(g3) = 2.2
    c: Coincident(g7,g6)
    c: Coincident(g8,g7)
    c: Parallel(g7,g-4)
    c: Parallel(g7,g9)
    c: Perpendicular(g6,g7)
    c: Parallel(g6,g8)
    c: Distance(g6,g15) = 5.2
    c: Distance(g7) = 5.2
    c: Coincident(g11,g10)
    c: Parallel(g10,g9)
    c: Parallel(g11,g6)
    c: Distance(g10) = 1.6
    c: Distance(g11) = 1.6
    c: Coincident(g10,g15)
    c: Distance(g11,g2) = 1.6
    c: Distance(g2,g10) = 1.6
    c: PointOnObject(g13,g8)
    c: PointOnObject(g13,g9)
    c: Tangent(g8,g12) = 1.5708
    c: Tangent(g9,g12) = 1.5708
    c: PointOnObject(g15,g9)
    c: Tangent(g6,g14) = 1.5708
    c: Tangent(g9,g14) = 1.5708
    c: Equal(g12,g14)
    c: Coincident(g6,g11)
    c: Coincident(g3,g0)
FEATURE [Part::Extrusion] Extrude016  label="Extrude fermo rumble"
  Base = -> Sketch020
  Dir = (0,-1,2e-16)
  DirMode = 2
  FaceMakerClass = Part::FaceMakerBullseye
  FaceMakerMode = 3
  LengthFwd = 25.2
  LengthRev = 0
  Solid = true
  Symmetric = true
FEATURE [Sketcher::SketchObject] Sketch021  label="perno fermo rumble001"
  ArcFitTolerance = 1e-06
  AttachmentSupport = -> [XZ_Plane001]
  FullyConstrained = true
  MakeInternals = false
  MapMode = 5
  Placement = pos=(0,0,0) rot=(1,0,0;1.5708rad)
  sketch-geometry (16):
    g0: LineSegment StartX=0 StartY=0.45 StartZ=0 EndX=0 EndY=1.55 EndZ=0
    g1: LineSegment StartX=0.45 StartY=2 StartZ=0 EndX=1.55 EndY=2 EndZ=0
    g2: LineSegment StartX=2 StartY=1.55 StartZ=0 EndX=2 EndY=0.45 EndZ=0
    g3: LineSegment StartX=1.55 StartY=0 StartZ=0 EndX=0.45 EndY=0 EndZ=0
    g4: ArcOfCircle [constr] CenterX=0.45 CenterY=1.55 CenterZ=0 NormalX=0 NormalY=0 NormalZ=1 AngleXU=0 Radius=0.45 StartAngle=1.5708 EndAngle=3.14159
    g5: GeomPoint [constr] X=0 Y=2 Z=0
    g6: LineSegment StartX=0.45 StartY=2 StartZ=0 EndX=0 EndY=1.55 EndZ=0
    g7: ArcOfCircle [constr] CenterX=1.55 CenterY=1.55 CenterZ=0 NormalX=0 NormalY=0 NormalZ=1 AngleXU=0 Radius=0.45 StartAngle=0 EndAngle=1.5708
    g8: GeomPoint [constr] X=2 Y=2 Z=0
    g9: LineSegment StartX=2 StartY=1.55 StartZ=0 EndX=1.55 EndY=2 EndZ=0
    g10: ArcOfCircle [constr] CenterX=1.55 CenterY=0.45 CenterZ=0 NormalX=0 NormalY=0 NormalZ=1 AngleXU=0 Radius=0.45 StartAngle=4.71239 EndAngle=6.28319
    g11: GeomPoint [constr] X=2 Y=0 Z=0
    g12: LineSegment StartX=1.55 StartY=0 StartZ=0 EndX=2 EndY=0.45 EndZ=0
    g13: ArcOfCircle [constr] CenterX=0.45 CenterY=0.45 CenterZ=0 NormalX=0 NormalY=0 NormalZ=1 AngleXU=0 Radius=0.45 StartAngle=3.14159 EndAngle=4.71239
    g14: GeomPoint [constr] X=0 Y=0 Z=0
    g15: LineSegment StartX=0 StartY=0.45 StartZ=0 EndX=0.45 EndY=0 EndZ=0
  constraints (35):
    c: Coincident(g14,g-1)
    c: PointOnObject(g5,g-2)
    c: Horizontal(g1)
    c: Vertical(g2)
    c: Horizontal(g3)
    c: DistanceX(g5,g8) = 2
    c: DistanceY(g11,g8) = 2
    c: PointOnObject(g5,g0)
    c: PointOnObject(g5,g1)
    c: Tangent(g0,g4) = 1.5708
    c: Tangent(g1,g4) = 1.5708
    c: Coincident(g6,g0)
    c: Coincident(g6,g1)
    c: PointOnObject(g8,g2)
    c: PointOnObject(g8,g1)
    c: Tangent(g2,g7) = 1.5708
    c: Tangent(g1,g7) = 1.5708
    c: Coincident(g9,g2)
    c: Coincident(g9,g1)
    c: PointOnObject(g11,g2)
    c: PointOnObject(g11,g3)
    c: Tangent(g2,g10) = 1.5708
    c: Tangent(g3,g10) = 1.5708
    c: Coincident(g12,g2)
    c: Coincident(g12,g3)
    c: PointOnObject(g14,g0)
    c: PointOnObject(g14,g3)
    c: Tangent(g0,g13) = 1.5708
    c: Tangent(g3,g13) = 1.5708
    c: Coincident(g15,g0)
    c: Coincident(g15,g3)
    c: Equal(g6,g9)
    c: Equal(g9,g12)
    c: Equal(g12,g15)
    c: DistanceX(g14,g3) = 0.45
FEATURE [Part::Extrusion] Extrude017  label="Extrude perno fermo rumble"
  Base = -> Sketch021
  Dir = (0,-1,2e-16)
  DirMode = 2
  FaceMakerClass = Part::FaceMakerBullseye
  FaceMakerMode = 3
  LengthFwd = 25.2
  LengthRev = 0
  Solid = true
  Symmetric = true
FEATURE [Sketcher::SketchObject] Sketch022  label="fori per M3x5(OD)x6(L)"
  ArcFitTolerance = 1e-06
  AttachmentSupport = -> [XZ_Plane]
  ExternalGeometry = -> [Sketch016]
  FullyConstrained = true
  MakeInternals = false
  MapMode = 5
  Placement = pos=(0,0,0) rot=(1,0,0;1.5708rad)
  sketch-geometry (7):
    g0: Circle CenterX=-5.6 CenterY=34.8 CenterZ=0 NormalX=0 NormalY=0 NormalZ=1 AngleXU=0 Radius=2.5
    g1: Circle CenterX=-5.6 CenterY=7.6 CenterZ=0 NormalX=0 NormalY=0 NormalZ=1 AngleXU=0 Radius=2.5
    g2: Circle CenterX=-78.51 CenterY=34.8 CenterZ=0 NormalX=0 NormalY=0 NormalZ=1 AngleXU=0 Radius=2.5
    g3: Circle CenterX=-78.51 CenterY=7.6 CenterZ=0 NormalX=0 NormalY=0 NormalZ=1 AngleXU=0 Radius=2.5
    g4: Circle CenterX=-184.08 CenterY=34.8 CenterZ=0 NormalX=0 NormalY=0 NormalZ=1 AngleXU=0 Radius=2.5
    g5: Circle CenterX=-179.305 CenterY=-76.8316 CenterZ=0 NormalX=0 NormalY=0 NormalZ=1 AngleXU=0 Radius=2.5
    g6: Circle CenterX=-213.443 CenterY=-76.8316 CenterZ=0 NormalX=0 NormalY=0 NormalZ=1 AngleXU=0 Radius=2.5
  constraints (14):
    c: Diameter(g0) = 5
    c: Diameter(g1) = 5
    c: Diameter(g2) = 5
    c: Diameter(g3) = 5
    c: Diameter(g4) = 5
    c: Diameter(g5) = 5
    c: Diameter(g6) = 5
    c: Coincident(g0,g-8)
    c: Coincident(g1,g-9)
    c: Coincident(g2,g-6)
    c: Coincident(g3,g-7)
    c: Coincident(g4,g-5)
    c: Coincident(g5,g-4)
    c: Coincident(g6,g-3)
FEATURE [Part::Extrusion] Extrude018  label="Extrude fori M3x5x6 - dx"
  Base = -> Sketch022
  Dir = (0,-1,2e-16)
  DirMode = 2
  FaceMakerClass = Part::FaceMakerBullseye
  FaceMakerMode = 3
  LengthFwd = 6.2
  LengthRev = 0
  Placement = pos=(0,-9.5,0) rot=(0,0,1;0rad)
  Solid = true
  Symmetric = true
FEATURE [Part::Extrusion] Extrude019  label="Extrude fori M3x5x6 - sx"
  Base = -> Sketch022
  Dir = (0,-1,2e-16)
  DirMode = 2
  FaceMakerClass = Part::FaceMakerBullseye
  FaceMakerMode = 3
  LengthFwd = 6.2
  LengthRev = 0
  Placement = pos=(0,9.5,0) rot=(0,0,1;0rad)
  Solid = true
  Symmetric = true
FEATURE [Sketcher::SketchObject] Sketch023  label="foro anteriore M3x5x6"
  ArcFitTolerance = 1e-06
  AttachmentSupport = -> [YZ_Plane]
  FullyConstrained = true
  MakeInternals = false
  MapMode = 5
  Placement = pos=(0,0,0) rot=(0.57735,0.57735,0.57735;2.0944rad)
  sketch-geometry (2):
    g0: LineSegment [constr] StartX=0 StartY=0 StartZ=0 EndX=0 EndY=38.6 EndZ=0
    g1: Circle CenterX=0 CenterY=38.6 CenterZ=0 NormalX=0 NormalY=0 NormalZ=1 AngleXU=0 Radius=2.5
  constraints (5):
    c: Coincident(g0,g-1)
    c: PointOnObject(g0,g-2)
    c: DistanceY(g0,g0) = 38.6
    c: Diameter(g1) = 5
    c: Coincident(g1,g0)
FEATURE [Part::Extrusion] Extrude020  label="Extrude foro anteriore M3x5x6"
  Base = -> Sketch023
  Dir = (1,0,0)
  DirMode = 2
  FaceMakerClass = Part::FaceMakerBullseye
  FaceMakerMode = 3
  LengthFwd = -6.2
  LengthRev = 0
  Solid = true
  Symmetric = false
FEATURE [Sketcher::SketchObject] Sketch024  label="fori per viti frontale"
  ArcFitTolerance = 1e-06
  AttachmentSupport = -> [YZ_Plane]
  FullyConstrained = true
  MakeInternals = false
  MapMode = 5
  Placement = pos=(0,0,0) rot=(0.57735,0.57735,0.57735;2.0944rad)
  sketch-geometry (9):
    g0: LineSegment [constr] StartX=-10.3 StartY=30.721 StartZ=0 EndX=10.3 EndY=30.721 EndZ=0
    g1: LineSegment [constr] StartX=10.3 StartY=30.721 StartZ=0 EndX=10.3 EndY=10.121 EndZ=0
    g2: LineSegment [constr] StartX=10.3 StartY=10.121 StartZ=0 EndX=-10.3 EndY=10.121 EndZ=0
    g3: LineSegment [constr] StartX=-10.3 StartY=10.121 StartZ=0 EndX=-10.3 EndY=30.721 EndZ=0
    g4: LineSegment [constr] StartX=0 StartY=0 StartZ=0 EndX=0 EndY=10.121 EndZ=0
    g5: Circle CenterX=-10.3 CenterY=30.721 CenterZ=0 NormalX=0 NormalY=0 NormalZ=1 AngleXU=0 Radius=2
    g6: Circle CenterX=10.3 CenterY=30.721 CenterZ=0 NormalX=0 NormalY=0 NormalZ=1 AngleXU=0 Radius=2
    g7: Circle CenterX=-10.3 CenterY=10.121 CenterZ=0 NormalX=0 NormalY=0 NormalZ=1 AngleXU=0 Radius=2
    g8: Circle CenterX=10.3 CenterY=10.121 CenterZ=0 NormalX=0 NormalY=0 NormalZ=1 AngleXU=0 Radius=2
  constraints (22):
    c: Horizontal(g0)
    c: Coincident(g1,g0)
    c: Vertical(g1)
    c: Coincident(g2,g1)
    c: Horizontal(g2)
    c: Coincident(g3,g2)
    c: Coincident(g3,g0)
    c: Vertical(g3)
    c: DistanceX(g0,g0) = 20.6
    c: DistanceY(g3,g3) = 20.6
    c: Coincident(g4,g-1)
    c: PointOnObject(g4,g-2)
    c: DistanceY(g4,g4) = 10.121
    c: Symmetric(g2,g2,g4)
    c: Diameter(g5) = 4
    c: Diameter(g6) = 4
    c: Diameter(g7) = 4
    c: Diameter(g8) = 4
    c: Coincident(g5,g0)
    c: Coincident(g6,g0)
    c: Coincident(g7,g2)
    c: Coincident(g8,g1)
FEATURE [Part::Extrusion] Extrude021  label="Extrude fori per viti frontale"
  Base = -> Sketch024
  Dir = (1,0,0)
  DirMode = 2
  FaceMakerClass = Part::FaceMakerBullseye
  FaceMakerMode = 3
  LengthFwd = -2.4
  LengthRev = 0
  Solid = true
  Symmetric = false
FEATURE [Sketcher::SketchObject] Sketch025  label="foro per filo CAM"
  ArcFitTolerance = 1e-06
  AttachmentSupport = -> [XZ_Plane]
  ExternalGeometry = -> [Sketch]
  FullyConstrained = true
  MakeInternals = false
  MapMode = 5
  Placement = pos=(0,0,0) rot=(1,0,0;1.5708rad)
  sketch-geometry (4):
    g0: LineSegment StartX=-44.6 StartY=41.2 StartZ=0 EndX=-44.6 EndY=36.4 EndZ=0
    g1: LineSegment StartX=-44.6 StartY=36.4 StartZ=0 EndX=-54.6 EndY=36.4 EndZ=0
    g2: LineSegment StartX=-54.6 StartY=36.4 StartZ=0 EndX=-50.4 EndY=41.2 EndZ=0
    g3: LineSegment StartX=-50.4 StartY=41.2 StartZ=0 EndX=-44.6 EndY=41.2 EndZ=0
  constraints (11):
    c: Vertical(g0)
    c: Coincident(g1,g0)
    c: Horizontal(g1)
    c: Coincident(g2,g1)
    c: Coincident(g3,g2)
    c: Coincident(g3,g0)
    c: Horizontal(g3)
    c: Coincident(g0,g-3)
    c: DistanceY(g0,g-4) = 0
    c: DistanceX(g3,g3) = 5.8
    c: DistanceX(g1,g1) = 10
FEATURE [Part::Extrusion] Extrude022  label="Extrude foro per filo CAM dx"
  Base = -> Sketch025
  Dir = (0,-1,2e-16)
  DirMode = 2
  FaceMakerClass = Part::FaceMakerBullseye
  FaceMakerMode = 3
  LengthFwd = 4.9
  LengthRev = 0
  Placement = pos=(0,6.95,0) rot=(0,0,1;0rad)
  Solid = true
  Symmetric = true
FEATURE [Part::Extrusion] Extrude023  label="Extrude foro per filo CAM sx"
  Base = -> Sketch025
  Dir = (0,-1,2e-16)
  DirMode = 2
  FaceMakerClass = Part::FaceMakerBullseye
  FaceMakerMode = 3
  LengthFwd = 4.9
  LengthRev = 0
  Placement = pos=(0,-6.95,0) rot=(0,0,1;0rad)
  Solid = true
  Symmetric = true
FEATURE [Sketcher::SketchObject] Sketch026  label="foro sotto anteriore M3x5x6"
  ArcFitTolerance = 1e-06
  AttachmentSupport = -> [XY_Plane]
  FullyConstrained = true
  MakeInternals = false
  MapMode = 5
  sketch-geometry (2):
    g0: LineSegment [constr] StartX=0 StartY=0 StartZ=0 EndX=-16.5 EndY=0 EndZ=0
    g1: Circle CenterX=-16.5 CenterY=0 CenterZ=0 NormalX=0 NormalY=0 NormalZ=1 AngleXU=0 Radius=2.5
  constraints (5):
    c: Distance(g0) = 16.5
    c: Coincident(g0,g-1)
    c: PointOnObject(g0,g-1)
    c: Diameter(g1) = 5
    c: Coincident(g0,g1)
FEATURE [Sketcher::SketchObject] Sketch027  label="foro sotto posteriore M3x5x6"
  ArcFitTolerance = 1e-06
  AttachmentSupport = -> [XY_Plane]
  ExternalGeometry = -> [Sketch]
  FullyConstrained = true
  MakeInternals = false
  MapMode = 5
  sketch-geometry (2):
    g0: LineSegment [constr] StartX=-82.8 StartY=2e-16 StartZ=0 EndX=-71.3 EndY=2e-16 EndZ=0
    g1: Circle CenterX=-71.3 CenterY=2e-16 CenterZ=0 NormalX=0 NormalY=0 NormalZ=1 AngleXU=0 Radius=2.5
  constraints (5):
    c: Distance(g0) = 11.5
    c: Coincident(g0,g-3)
    c: PointOnObject(g0,g-3)
    c: Diameter(g1) = 5
    c: Coincident(g1,g0)
FEATURE [Sketcher::SketchObject] Sketch029  label="fori sotto impugnatura"
  ArcFitTolerance = 1e-06
  AttachmentSupport = -> [XY_Plane]
  ExternalGeometry = -> [Sketch]
  FullyConstrained = true
  MakeInternals = false
  MapMode = 5
  sketch-geometry (15):
    g0: LineSegment [constr] StartX=-175.232 StartY=-1.83e-14 StartZ=0 EndX=-191.232 EndY=0 EndZ=0
    g1: Circle CenterX=-191.232 CenterY=0 CenterZ=0 NormalX=0 NormalY=0 NormalZ=1 AngleXU=0 Radius=3.95
    g2: LineSegment [constr] StartX=-175.232 StartY=-1.83e-14 StartZ=0 EndX=-204.275 EndY=0 EndZ=0
    g3: LineSegment StartX=-204.275 StartY=3.525 StartZ=0 EndX=-204.275 EndY=-3.525 EndZ=0
    g4: LineSegment StartX=-205.4 StartY=-4.65 StartZ=0 EndX=-206.65 EndY=-4.65 EndZ=0
    g5: LineSegment StartX=-207.775 StartY=-3.525 StartZ=0 EndX=-207.775 EndY=3.525 EndZ=0
    g6: LineSegment StartX=-206.65 StartY=4.65 StartZ=0 EndX=-205.4 EndY=4.65 EndZ=0
    g7: ArcOfCircle CenterX=-206.65 CenterY=3.525 CenterZ=0 NormalX=0 NormalY=0 NormalZ=1 AngleXU=0 Radius=1.125 StartAngle=1.5708 EndAngle=3.14159
    g8: GeomPoint [constr] X=-207.775 Y=4.65 Z=0
    g9: ArcOfCircle CenterX=-205.4 CenterY=3.525 CenterZ=0 NormalX=0 NormalY=0 NormalZ=1 AngleXU=0 Radius=1.125 StartAngle=0 EndAngle=1.5708
    g10: GeomPoint [constr] X=-204.275 Y=4.65 Z=0
    g11: ArcOfCircle CenterX=-205.4 CenterY=-3.525 CenterZ=0 NormalX=0 NormalY=0 NormalZ=1 AngleXU=0 Radius=1.125 StartAngle=4.71239 EndAngle=6.28319
    g12: GeomPoint [constr] X=-204.275 Y=-4.65 Z=0
    g13: ArcOfCircle CenterX=-206.65 CenterY=-3.525 CenterZ=0 NormalX=0 NormalY=0 NormalZ=1 AngleXU=0 Radius=1.125 StartAngle=3.14159 EndAngle=4.71239
    g14: GeomPoint [constr] X=-207.775 Y=-4.65 Z=0
  constraints (35):
    c: Distance(g0) = 16
    c: Coincident(g0,g-3)
    c: PointOnObject(g0,g-1)
    c: Diameter(g1) = 7.9
    c: Coincident(g1,g0)
    c: Coincident(g2,g0)
    c: PointOnObject(g2,g-1)
    c: Vertical(g3)
    c: Horizontal(g4)
    c: Vertical(g5)
    c: Horizontal(g6)
    c: DistanceY(g12,g10) = 9.3
    c: DistanceX(g8,g10) = 3.5
    c: Symmetric(g10,g12,g2)
    c: PointOnObject(g8,g5)
    c: PointOnObject(g8,g6)
    c: Tangent(g5,g7) = 1.5708
    c: Tangent(g6,g7) = 1.5708
    c: PointOnObject(g10,g3)
    c: PointOnObject(g10,g6)
    c: Tangent(g3,g9) = 1.5708
    c: Tangent(g6,g9) = 1.5708
    c: PointOnObject(g12,g3)
    c: PointOnObject(g12,g4)
    c: Tangent(g3,g11) = 1.5708
    c: Tangent(g4,g11) = 1.5708
    c: PointOnObject(g14,g4)
    c: PointOnObject(g14,g5)
    c: Tangent(g4,g13) = 1.5708
    c: Tangent(g5,g13) = 1.5708
    c: Equal(g7,g9)
    c: Equal(g9,g11)
    c: Equal(g11,g13)
    c: DistanceX(g6,g6) = 1.25
    c: DistanceX(g-5,g5) = 6.8
FEATURE [Sketcher::SketchObject] Sketch030  label="fori superiori per solenoide e oled"
  ArcFitTolerance = 1e-06
  AttachmentSupport = -> [XY_Plane]
  ExternalGeometry = -> [Sketch]
  FullyConstrained = true
  MakeInternals = false
  MapMode = 5
  sketch-geometry (33):
    g0: LineSegment [constr] StartX=-181.6 StartY=1.12e-14 StartZ=0 EndX=-169.91 EndY=0 EndZ=0
    g1: LineSegment [constr] StartX=-169.91 StartY=0 StartZ=0 EndX=-169.91 EndY=-2.6 EndZ=0
    g2: LineSegment [constr] StartX=-169.91 StartY=0 StartZ=0 EndX=-169.91 EndY=2.6 EndZ=0
    g3: LineSegment StartX=-169.91 StartY=4.975 StartZ=0 EndX=-169.91 EndY=8.225 EndZ=0
    g4: LineSegment StartX=-167.535 StartY=10.6 StartZ=0 EndX=-167.285 EndY=10.6 EndZ=0
    g5: LineSegment StartX=-164.91 StartY=8.225 StartZ=0 EndX=-164.91 EndY=4.975 EndZ=0
    g6: LineSegment StartX=-167.285 StartY=2.6 StartZ=0 EndX=-167.535 EndY=2.6 EndZ=0
    g7: LineSegment StartX=-169.91 StartY=-4.975 StartZ=0 EndX=-169.91 EndY=-8.225 EndZ=0
    g8: LineSegment StartX=-167.535 StartY=-10.6 StartZ=0 EndX=-167.285 EndY=-10.6 EndZ=0
    g9: LineSegment StartX=-164.91 StartY=-8.225 StartZ=0 EndX=-164.91 EndY=-4.975 EndZ=0
    g10: LineSegment StartX=-167.285 StartY=-2.6 StartZ=0 EndX=-167.535 EndY=-2.6 EndZ=0
    g11: ArcOfCircle CenterX=-167.535 CenterY=8.225 CenterZ=0 NormalX=0 NormalY=0 NormalZ=1 AngleXU=0 Radius=2.375 StartAngle=1.5708 EndAngle=3.14159
    g12: GeomPoint [constr] X=-169.91 Y=10.6 Z=0
    g13: ArcOfCircle CenterX=-167.285 CenterY=8.225 CenterZ=0 NormalX=0 NormalY=0 NormalZ=1 AngleXU=0 Radius=2.375 StartAngle=0 EndAngle=1.5708
    g14: GeomPoint [constr] X=-164.91 Y=10.6 Z=0
    g15: ArcOfCircle CenterX=-167.285 CenterY=4.975 CenterZ=0 NormalX=0 NormalY=0 NormalZ=1 AngleXU=0 Radius=2.375 StartAngle=4.71239 EndAngle=6.28319
    g16: GeomPoint [constr] X=-164.91 Y=2.6 Z=0
    g17: ArcOfCircle CenterX=-167.535 CenterY=4.975 CenterZ=0 NormalX=0 NormalY=0 NormalZ=1 AngleXU=0 Radius=2.375 StartAngle=3.14159 EndAngle=4.71239
    g18: GeomPoint [constr] X=-169.91 Y=2.6 Z=0
    g19: ArcOfCircle CenterX=-167.535 CenterY=-4.975 CenterZ=0 NormalX=0 NormalY=0 NormalZ=1 AngleXU=0 Radius=2.375 StartAngle=1.5708 EndAngle=3.14159
    g20: GeomPoint [constr] X=-169.91 Y=-2.6 Z=0
    g21: ArcOfCircle CenterX=-167.285 CenterY=-4.975 CenterZ=0 NormalX=0 NormalY=0 NormalZ=1 AngleXU=0 Radius=2.375 StartAngle=0 EndAngle=1.5708
    g22: GeomPoint [constr] X=-164.91 Y=-2.6 Z=0
    g23: ArcOfCircle CenterX=-167.285 CenterY=-8.225 CenterZ=0 NormalX=0 NormalY=0 NormalZ=1 AngleXU=0 Radius=2.375 StartAngle=4.71239 EndAngle=6.28319
    g24: GeomPoint [constr] X=-164.91 Y=-10.6 Z=0
    g25: ArcOfCircle CenterX=-167.535 CenterY=-8.225 CenterZ=0 NormalX=0 NormalY=0 NormalZ=1 AngleXU=0 Radius=2.375 StartAngle=3.14159 EndAngle=4.71239
    g26: GeomPoint [constr] X=-169.91 Y=-10.6 Z=0
    g27: LineSegment [constr] StartX=-181.6 StartY=1.12e-14 StartZ=0 EndX=-152.209 EndY=0 EndZ=0
    g28: LineSegment [constr] StartX=-181.6 StartY=1.12e-14 StartZ=0 EndX=-130.41 EndY=0 EndZ=0
    g29: LineSegment [constr] StartX=-152.209 StartY=0 StartZ=0 EndX=-152.209 EndY=6.95 EndZ=0
    g30: LineSegment [constr] StartX=-130.41 StartY=0 StartZ=0 EndX=-130.41 EndY=-6.95 EndZ=0
    g31: Circle CenterX=-152.209 CenterY=6.95 CenterZ=0 NormalX=0 NormalY=0 NormalZ=1 AngleXU=0 Radius=2.1
    g32: Circle CenterX=-130.41 CenterY=-6.95 CenterZ=0 NormalX=0 NormalY=0 NormalZ=1 AngleXU=0 Radius=2.1
  constraints (79):
    c: Distance(g0) = 11.69
    c: PointOnObject(g0,g-1)
    c: Coincident(g-4,g0)
    c: Distance(g1) = 2.6
    c: Coincident(g1,g0)
    c: Vertical(g1)
    c: Distance(g2) = 2.6
    c: Coincident(g2,g0)
    c: Vertical(g2)
    c: Distance(g18,g12) = 8
    c: Coincident(g18,g2)
    c: Vertical(g3)
    c: Distance(g14,g12) = 5
    c: Horizontal(g4)
    c: Distance(g16,g14) = 8
    c: Vertical(g5)
    c: Distance(g26,g20) = 8
    c: Coincident(g20,g1)
    c: Vertical(g7)
    c: Distance(g26,g24) = 5
    c: Horizontal(g8)
    c: Distance(g24,g22) = 8
    c: Vertical(g9)
    c: PointOnObject(g12,g3)
    c: PointOnObject(g12,g4)
    c: Tangent(g3,g11) = 1.5708
    c: Tangent(g4,g11) = 1.5708
    c: PointOnObject(g14,g5)
    c: PointOnObject(g14,g4)
    c: Tangent(g5,g13) = 1.5708
    c: Tangent(g4,g13) = 1.5708
    c: PointOnObject(g16,g5)
    c: PointOnObject(g16,g6)
    c: Tangent(g5,g15) = 1.5708
    c: Tangent(g6,g15) = 1.5708
    c: PointOnObject(g18,g3)
    c: PointOnObject(g18,g6)
    c: Tangent(g3,g17) = 1.5708
    c: Tangent(g6,g17) = 1.5708
    c: Equal(g11,g13)
    c: Equal(g13,g15)
    c: Equal(g15,g17)
    c: DistanceX(g4,g4) = 0.25
    c: PointOnObject(g20,g7)
    c: PointOnObject(g20,g10)
    c: Tangent(g7,g19) = -1.5708
    c: Tangent(g10,g19) = -1.5708
    c: PointOnObject(g22,g9)
    c: PointOnObject(g22,g10)
    c: Tangent(g9,g21) = -1.5708
    c: Tangent(g10,g21) = -1.5708
    c: PointOnObject(g24,g9)
    c: PointOnObject(g24,g8)
    c: Tangent(g9,g23) = -1.5708
    c: Tangent(g8,g23) = -1.5708
    c: PointOnObject(g26,g8)
    c: PointOnObject(g26,g7)
    c: Tangent(g8,g25) = -1.5708
    c: Tangent(g7,g25) = -1.5708
    c: Equal(g19,g21)
    c: Equal(g21,g23)
    c: Equal(g23,g25)
    c: DistanceX(g10,g10) = 0.25
    c: Distance(g27) = 29.391
    c: Coincident(g27,g0)
    c: PointOnObject(g27,g-1)
    c: Distance(g28) = 51.19
    c: Coincident(g28,g0)
    c: PointOnObject(g28,g-1)
    c: Distance(g29) = 6.95
    c: Coincident(g29,g27)
    c: Vertical(g29)
    c: Distance(g30) = 6.95
    c: Coincident(g30,g28)
    c: Vertical(g30)
    c: Diameter(g31) = 4.2
    c: Diameter(g32) = 4.2
    c: Coincident(g32,g30)
    c: Coincident(g31,g29)
FEATURE [Sketcher::SketchObject] Sketch031  label="fori inferiori switch pompa"
  ArcFitTolerance = 1e-06
  AttachmentSupport = -> [XY_Plane]
  ExternalGeometry = -> [Sketch]
  FullyConstrained = true
  MakeInternals = false
  MapMode = 5
  sketch-geometry (4):
    g0: LineSegment [constr] StartX=-57.2 StartY=1.9e-15 StartZ=0 EndX=-62.45 EndY=1.9e-15 EndZ=0
    g1: LineSegment [constr] StartX=-62.45 StartY=3.25 StartZ=0 EndX=-62.45 EndY=-3.25 EndZ=0
    g2: Circle CenterX=-62.45 CenterY=3.25 CenterZ=0 NormalX=0 NormalY=0 NormalZ=1 AngleXU=0 Radius=1.6
    g3: Circle CenterX=-62.45 CenterY=-3.25 CenterZ=0 NormalX=0 NormalY=0 NormalZ=1 AngleXU=0 Radius=1.6
  constraints (10):
    c: Distance(g0) = 5.25
    c: Coincident(g0,g-3)
    c: PointOnObject(g0,g-3)
    c: Vertical(g1)
    c: DistanceY(g1,g1) = 6.5
    c: Symmetric(g1,g1,g0)
    c: Diameter(g2) = 3.2
    c: Diameter(g3) = 3.2
    c: Coincident(g2,g1)
    c: Coincident(g3,g1)
FEATURE [Sketcher::SketchObject] Sketch032  label="spazio per PILA 18650"
  ArcFitTolerance = 1e-06
  AttachmentSupport = -> [XY_Plane]
  ExternalGeometry = -> [Sketch]
  FullyConstrained = true
  MakeInternals = false
  MapMode = 5
  sketch-geometry (2):
    g0: LineSegment [constr] StartX=-178.142 StartY=-1.74e-14 StartZ=0 EndX=-190.142 EndY=-1.83e-14 EndZ=0
    g1: Circle CenterX=-190.142 CenterY=-1.83e-14 CenterZ=0 NormalX=0 NormalY=0 NormalZ=1 AngleXU=0 Radius=9.25
  constraints (5):
    c: Distance(g0) = 12
    c: Coincident(g0,g-3)
    c: PointOnObject(g0,g-4)
    c: Diameter(g1) = 18.5
    c: Coincident(g1,g0)
FEATURE [Part::Extrusion] Extrude030  label="Extrude spazio per PILA 18650"
  Base = -> Sketch032
  Dir = (0,0,1)
  DirLink = -> Sketch [Edge45]
  DirMode = 2
  FaceMakerClass = Part::FaceMakerBullseye
  FaceMakerMode = 3
  LengthFwd = 68
  LengthRev = 0
  Placement = pos=(6,0,-72.7) rot=(0,0,1;0rad)
  Solid = true
  Symmetric = false
FEATURE [Sketcher::SketchObject] Sketch033  label="fermo per scheda micro"
  ArcFitTolerance = 1e-06
  AttachmentSupport = -> [XZ_Plane]
  ExternalGeometry = -> [Sketch]
  FullyConstrained = true
  MakeInternals = false
  MapMode = 5
  Placement = pos=(0,0,0) rot=(1,0,0;1.5708rad)
  sketch-geometry (12):
    g0: LineSegment StartX=-11.6 StartY=6 StartZ=0 EndX=-4 EndY=6 EndZ=0
    g1: LineSegment StartX=-4 StartY=6 StartZ=0 EndX=-4 EndY=36.4 EndZ=0
    g2: LineSegment StartX=-4 StartY=36.4 StartZ=0 EndX=-11.6 EndY=36.4 EndZ=0
    g3: LineSegment StartX=-11.6 StartY=36.4 StartZ=0 EndX=-11.6 EndY=6 EndZ=0
    g4: LineSegment StartX=-80.11 StartY=11.6 StartZ=0 EndX=-70.51 EndY=11.6 EndZ=0
    g5: LineSegment StartX=-70.51 StartY=11.6 StartZ=0 EndX=-70.51 EndY=6 EndZ=0
    g6: LineSegment StartX=-70.51 StartY=6 StartZ=0 EndX=-80.11 EndY=6 EndZ=0
    g7: LineSegment StartX=-80.11 StartY=6 StartZ=0 EndX=-80.11 EndY=11.6 EndZ=0
    g8: LineSegment StartX=-78.51 StartY=36.4 StartZ=0 EndX=-70.51 EndY=36.4 EndZ=0
    g9: LineSegment StartX=-70.51 StartY=36.4 StartZ=0 EndX=-70.51 EndY=30.8 EndZ=0
    g10: LineSegment StartX=-70.51 StartY=30.8 StartZ=0 EndX=-78.51 EndY=30.8 EndZ=0
    g11: LineSegment StartX=-78.51 StartY=30.8 StartZ=0 EndX=-78.51 EndY=36.4 EndZ=0
  constraints (33):
    c: Horizontal(g0)
    c: Coincident(g1,g0)
    c: Coincident(g2,g1)
    c: Horizontal(g2)
    c: Coincident(g3,g2)
    c: Coincident(g3,g0)
    c: Vertical(g3)
    c: DistanceX(g2,g2) = 7.6
    c: Coincident(g1,g-3)
    c: Coincident(g0,g-3)
    c: Horizontal(g4)
    c: Coincident(g5,g4)
    c: Vertical(g5)
    c: Coincident(g6,g5)
    c: Horizontal(g6)
    c: Coincident(g7,g6)
    c: Coincident(g7,g4)
    c: Vertical(g7)
    c: DistanceY(g5,g5) = 5.6
    c: DistanceX(g4,g4) = 9.6
    c: Coincident(g9,g8)
    c: Vertical(g9)
    c: Coincident(g10,g9)
    c: Horizontal(g10)
    c: Coincident(g11,g10)
    c: Coincident(g11,g8)
    c: Vertical(g11)
    c: DistanceY(g9,g9) = 5.6
    c: DistanceX(g10,g10) = 8
    c: Coincident(g4,g-4)
    c: DistanceX(g4,g10) = 1.6
    c: Horizontal(g8)
    c: DistanceY(g8,g1) = 0
FEATURE [Sketcher::SketchObject] Sketch034  label="buchi guida rail"
  ArcFitTolerance = 1e-06
  AttachmentSupport = -> [XY_Plane]
  ExternalGeometry = -> [Sketch]
  FullyConstrained = true
  MakeInternals = false
  MapMode = 5
  sketch-geometry (6):
    g0: LineSegment [constr] StartX=-100.8 StartY=9.1e-15 StartZ=0 EndX=-93.3 EndY=0 EndZ=0
    g1: LineSegment [constr] StartX=-93.3 StartY=0 StartZ=0 EndX=-73.3 EndY=0 EndZ=0
    g2: LineSegment [constr] StartX=-73.3 StartY=0 StartZ=0 EndX=-53.3 EndY=0 EndZ=0
    g3: Circle CenterX=-93.3 CenterY=0 CenterZ=0 NormalX=0 NormalY=0 NormalZ=1 AngleXU=0 Radius=2.5
    g4: Circle CenterX=-73.3 CenterY=0 CenterZ=0 NormalX=0 NormalY=0 NormalZ=1 AngleXU=0 Radius=2.5
    g5: Circle CenterX=-53.3 CenterY=0 CenterZ=0 NormalX=0 NormalY=0 NormalZ=1 AngleXU=0 Radius=2.5
  constraints (15):
    c: Distance(g0) = 7.5
    c: Coincident(g0,g-3)
    c: PointOnObject(g0,g-1)
    c: Distance(g1) = 20
    c: Coincident(g1,g0)
    c: PointOnObject(g1,g-1)
    c: Distance(g2) = 20
    c: Coincident(g2,g1)
    c: PointOnObject(g2,g-1)
    c: Diameter(g3) = 5
    c: Diameter(g4) = 5
    c: Diameter(g5) = 5
    c: Coincident(g3,g0)
    c: Coincident(g4,g1)
    c: Coincident(g5,g2)
FEATURE [PartDesign::FeatureBase] BaseFeature
  BaseFeature = -> Extrude017
  Suppressed = false
FEATURE [PartDesign::Body] Body001  label="perno fermo rumble"
  AllowCompound = false
  BaseFeature = -> Extrude017
  Group = -> [BaseFeature,Sketch021]
  Origin = -> Origin001
  Tip = -> BaseFeature
FEATURE [Part::Extrusion] Extrude032  label="Extrude buchi guida rail"
  Base = -> Sketch034
  Dir = (0,0,1)
  DirMode = 2
  FaceMakerClass = Part::FaceMakerBullseye
  FaceMakerMode = 3
  LengthFwd = -6.2
  LengthRev = 0
  Placement = pos=(0,0,43.2) rot=(0,0,1;0rad)
  Solid = true
  Symmetric = false
FEATURE [Part::Extrusion] Extrude033  label="Extrude fori superiori per solenoide e oled001"
  Base = -> Sketch030
  Dir = (0,0,1)
  DirMode = 2
  FaceMakerClass = Part::FaceMakerBullseye
  FaceMakerMode = 3
  LengthFwd = -4.8
  LengthRev = 0
  Placement = pos=(0,0,41.2) rot=(0,0,1;0rad)
  Solid = true
  Symmetric = false
FEATURE [Part::Extrusion] Extrude034  label="Extrude fori sotto impugnatura001"
  Base = -> Sketch029
  Dir = (0,0,1)
  DirMode = 2
  FaceMakerClass = Part::FaceMakerBullseye
  FaceMakerMode = 3
  LengthFwd = 5
  LengthRev = 0
  Placement = pos=(0,0,-83) rot=(0,0,1;0rad)
  Solid = true
  Symmetric = false
FEATURE [Part::Extrusion] Extrude035  label="Extrude fori inferiori switch pompa001"
  Base = -> Sketch031
  Dir = (0,0,1)
  DirMode = 2
  FaceMakerClass = Part::FaceMakerBullseye
  FaceMakerMode = 3
  LengthFwd = 4
  LengthRev = 0
  Placement = pos=(0,0,-1.7) rot=(0,0,1;0rad)
  Solid = true
  Symmetric = false
FEATURE [Part::Extrusion] Extrude036  label="Extrude foro sotto posteriore M3x5x007"
  Base = -> Sketch027
  Dir = (0,0,1)
  DirMode = 2
  FaceMakerClass = Part::FaceMakerBullseye
  FaceMakerMode = 3
  LengthFwd = 6.2
  LengthRev = 0
  Placement = pos=(0,0,-9.6) rot=(0,0,1;0rad)
  Solid = true
  Symmetric = false
FEATURE [Part::Extrusion] Extrude037  label="Extrude foro sotto anteriore M3x5x007"
  Base = -> Sketch026
  Dir = (0,0,1)
  DirMode = 2
  FaceMakerClass = Part::FaceMakerBullseye
  FaceMakerMode = 3
  LengthFwd = 6.2
  LengthRev = 0
  Solid = true
  Symmetric = false
FEATURE [Sketcher::SketchObject] Sketch035  label="foro per fissaggio micro"
  ArcFitTolerance = 1e-06
  AttachmentSupport = -> [XZ_Plane]
  ExternalGeometry = -> [Sketch,Sketch033]
  FullyConstrained = true
  MakeInternals = false
  MapMode = 5
  Placement = pos=(0,0,0) rot=(1,0,0;1.5708rad)
  sketch-geometry (3):
    g0: Circle CenterX=-7.8 CenterY=21.2 CenterZ=0 NormalX=0 NormalY=0 NormalZ=1 AngleXU=0 Radius=1.6
    g1: GeomPoint [constr] X=-4 Y=21.2 Z=0
    g2: LineSegment [constr] StartX=-4 StartY=21.2 StartZ=0 EndX=-11.6 EndY=21.2 EndZ=0
  constraints (6):
    c: Diameter(g0) = 3.2
    c: Symmetric(g-3,g-3,g1)
    c: Coincident(g2,g1)
    c: Horizontal(g2)
    c: DistanceX(g-4,g2) = 0
    c: Symmetric(g2,g1,g0)
FEATURE [Part::Extrusion] Extrude038  label="Extrude foro per fissaggio micro"
  Base = -> Sketch035
  Dir = (0,-1,2e-16)
  DirMode = 2
  FaceMakerClass = Part::FaceMakerBullseye
  FaceMakerMode = 3
  LengthFwd = 3
  LengthRev = 0
  Placement = pos=(0,8.6,0) rot=(0,0,1;0rad)
  Solid = true
  Symmetric = false
FEATURE [Sketcher::SketchObject] Sketch036  label="supporto per alimentatore"
  ArcFitTolerance = 1e-06
  AttachmentSupport = -> [XZ_Plane]
  ExternalGeometry = -> [Sketch,Sketch016,Sketch022]
  FullyConstrained = true
  MakeInternals = false
  MapMode = 5
  Placement = pos=(0,0,0) rot=(1,0,0;1.5708rad)
  sketch-geometry (5):
    g0: LineSegment StartX=-211.843 StartY=-50.0944 StartZ=0 EndX=-211.843 EndY=-80.4316 EndZ=0
    g1: LineSegment StartX=-211.843 StartY=-50.0944 StartZ=0 EndX=-207.775 EndY=-41.3701 EndZ=0
    g2: LineSegment [constr] StartX=-209.443 StartY=-50.0944 StartZ=0 EndX=-209.443 EndY=-80.4316 EndZ=0
    g3: LineSegment StartX=-207.775 StartY=-41.3701 StartZ=0 EndX=-207.775 EndY=-80.4316 EndZ=0
    g4: LineSegment StartX=-211.843 StartY=-80.4316 StartZ=0 EndX=-207.775 EndY=-80.4316 EndZ=0
  constraints (15):
    c: Vertical(g0)
    c: Coincident(g1,g0)
    c: Vertical(g2)
    c: Tangent(g2,g-5)
    c: Coincident(g3,g1)
    c: Vertical(g3)
    c: DistanceY(g-3,g3) = -2
    c: Tangent(g1,g-8)
    c: DistanceY(g-3,g0) = -2
    c: Coincident(g4,g0)
    c: Coincident(g4,g3)
    c: Tangent(g0,g-6)
    c: DistanceY(g-3,g2) = -2
    c: DistanceY(g2,g0) = 0
    c: DistanceX(g-3,g3) = 6.8
FEATURE [Part::Extrusion] Extrude039  label="Extrude039 supporto alimentatore"
  Base = -> Sketch036
  Dir = (0,-1,2e-16)
  DirMode = 2
  FaceMakerClass = Part::FaceMakerBullseye
  FaceMakerMode = 3
  LengthFwd = 25.2
  LengthRev = 0
  Solid = true
  Symmetric = true
FEATURE [Sketcher::SketchObject] Sketch037  label="scavo per alimentatore"
  ArcFitTolerance = 1e-06
  AttachmentSupport = -> [XZ_Plane]
  ExternalGeometry = -> [Sketch036]
  FullyConstrained = true
  MakeInternals = false
  MapMode = 5
  Placement = pos=(0,0,0) rot=(1,0,0;1.5708rad)
  sketch-geometry (4):
    g0: LineSegment StartX=-209.575 StartY=-50.4316 StartZ=0 EndX=-209.575 EndY=-80.4316 EndZ=0
    g1: LineSegment StartX=-209.575 StartY=-50.4316 StartZ=0 EndX=-207.775 EndY=-50.4316 EndZ=0
    g2: LineSegment StartX=-207.775 StartY=-50.4316 StartZ=0 EndX=-207.775 EndY=-80.4316 EndZ=0
    g3: LineSegment StartX=-207.775 StartY=-80.4316 StartZ=0 EndX=-209.575 EndY=-80.4316 EndZ=0
  constraints (11):
    c: Vertical(g0)
    c: Coincident(g1,g0)
    c: Horizontal(g1)
    c: Coincident(g2,g1)
    c: Vertical(g2)
    c: Coincident(g3,g2)
    c: Coincident(g3,g0)
    c: Horizontal(g3)
    c: DistanceX(g1,g1) = 1.8
    c: Coincident(g2,g-3)
    c: DistanceY(g2,g2) = 30
FEATURE [Part::Extrusion] Extrude040  label="Extrude040 scavo alimentatore"
  Base = -> Sketch037
  Dir = (0,-1,2e-16)
  DirMode = 2
  FaceMakerClass = Part::FaceMakerBullseye
  FaceMakerMode = 3
  LengthFwd = 19.5
  LengthRev = 0
  Solid = true
  Symmetric = true
FEATURE [Part::Extrusion] Extrude031  label="Extrude fermo per scheda micro"
  Base = -> Sketch033
  Dir = (0,-1,2e-16)
  DirMode = 2
  FaceMakerClass = Part::FaceMakerBullseye
  FaceMakerMode = 3
  LengthFwd = 3
  LengthRev = 0
  Placement = pos=(0,8.6,0) rot=(0,0,1;0rad)
  Solid = true
  Symmetric = false
FEATURE [Sketcher::SketchObject] Sketch038  label="scavo driver solenoide"
  ArcFitTolerance = 1e-06
  AttachmentSupport = -> [XZ_Plane]
  ExternalGeometry = -> [Sketch,Sketch036]
  FullyConstrained = true
  MakeInternals = false
  MapMode = 5
  Placement = pos=(0,0,0) rot=(1,0,0;1.5708rad)
  sketch-geometry (7):
    g0: LineSegment StartX=-193.66 StartY=-11.0994 StartZ=0 EndX=-195.11 EndY=-10.4232 EndZ=0
    g1: LineSegment StartX=-195.11 StartY=-10.4232 StartZ=0 EndX=-209.225 EndY=-40.6939 EndZ=0
    g2: LineSegment StartX=-193.66 StartY=-11.0994 StartZ=0 EndX=-190.216 EndY=-12.7054 EndZ=0
    g3: LineSegment StartX=-190.216 StartY=-12.7054 StartZ=0 EndX=-204.331 EndY=-42.9761 EndZ=0
    g4: LineSegment StartX=-204.331 StartY=-42.9761 StartZ=0 EndX=-207.775 EndY=-41.3701 EndZ=0
    g5: LineSegment [constr] StartX=-209.225 StartY=-40.6939 StartZ=0 EndX=-207.775 EndY=-41.3701 EndZ=0
    g6: LineSegment StartX=-209.225 StartY=-40.6939 StartZ=0 EndX=-207.775 EndY=-41.3701 EndZ=0
  constraints (19):
    c: Coincident(g1,g0)
    c: Coincident(g3,g2)
    c: Coincident(g4,g3)
    c: Distance(g2) = 3.8
    c: Distance(g1) = 33.4
    c: Coincident(g5,g1)
    c: Distance(g5) = 1.6
    c: Coincident(g-4,g5)
    c: Perpendicular(g5,g-3)
    c: Parallel(g1,g-3)
    c: Perpendicular(g1,g0)
    c: Distance(g0) = 1.6
    c: Coincident(g6,g1)
    c: Coincident(g6,g5)
    c: Parallel(g3,g-3)
    c: Perpendicular(g3,g4)
    c: Perpendicular(g2,g3)
    c: Coincident(g2,g0)
    c: Coincident(g4,g5)
FEATURE [Part::Extrusion] Extrude041  label="Extrude scavo driver solenoide"
  Base = -> Sketch038
  Dir = (0,-1,2e-16)
  DirMode = 2
  FaceMakerClass = Part::FaceMakerBullseye
  FaceMakerMode = 3
  LengthFwd = 17
  LengthRev = 0
  Solid = true
  Symmetric = true
FEATURE [Sketcher::SketchObject] Sketch039  label="scavo per cavo usb per micro"
  ArcFitTolerance = 1e-06
  AttachmentSupport = -> [XZ_Plane]
  ExternalGeometry = -> [Sketch,Sketch016]
  FullyConstrained = true
  MakeInternals = false
  MapMode = 5
  Placement = pos=(0,0,0) rot=(1,0,0;1.5708rad)
  sketch-geometry (4):
    g0: LineSegment StartX=-82.51 StartY=36.4 StartZ=0 EndX=-74.51 EndY=36.4 EndZ=0
    g1: LineSegment StartX=-74.51 StartY=36.4 StartZ=0 EndX=-74.51 EndY=30.8 EndZ=0
    g2: LineSegment StartX=-74.51 StartY=30.8 StartZ=0 EndX=-82.51 EndY=30.8 EndZ=0
    g3: LineSegment StartX=-82.51 StartY=30.8 StartZ=0 EndX=-82.51 EndY=36.4 EndZ=0
  constraints (11):
    c: Coincident(g1,g0)
    c: Vertical(g1)
    c: Coincident(g2,g1)
    c: Horizontal(g2)
    c: Coincident(g3,g2)
    c: Coincident(g3,g0)
    c: Vertical(g3)
    c: Tangent(g0,g-3)
    c: Tangent(g2,g-4)
    c: Tangent(g3,g-4)
    c: Tangent(g1,g-4)
FEATURE [Part::Extrusion] Extrude042  label="Extrude scavo per cavo usb per micro"
  Base = -> Sketch039
  Dir = (0,-1,2e-16)
  DirMode = 2
  FaceMakerClass = Part::FaceMakerBullseye
  FaceMakerMode = 3
  LengthFwd = 11.2
  LengthRev = 0
  Solid = true
  Symmetric = true
FEATURE [Sketcher::SketchObject] Sketch040  label="scavo saldature alimentatore connettore 5v"
  ArcFitTolerance = 1e-06
  AttachmentSupport = -> [XZ_Plane]
  ExternalGeometry = -> [Sketch037]
  FullyConstrained = true
  MakeInternals = false
  MapMode = 5
  Placement = pos=(0,0,0) rot=(1,0,0;1.5708rad)
  sketch-geometry (4):
    g0: LineSegment StartX=-211.175 StartY=-52.4316 StartZ=0 EndX=-211.175 EndY=-56.4316 EndZ=0
    g1: LineSegment StartX=-211.175 StartY=-52.4316 StartZ=0 EndX=-209.575 EndY=-52.4316 EndZ=0
    g2: LineSegment StartX=-209.575 StartY=-52.4316 StartZ=0 EndX=-209.575 EndY=-56.4316 EndZ=0
    g3: LineSegment StartX=-209.575 StartY=-56.4316 StartZ=0 EndX=-211.175 EndY=-56.4316 EndZ=0
  constraints (11):
    c: Vertical(g0)
    c: Coincident(g1,g0)
    c: Horizontal(g1)
    c: Coincident(g2,g1)
    c: Coincident(g3,g2)
    c: Coincident(g3,g0)
    c: Horizontal(g3)
    c: DistanceX(g1,g1) = 1.6
    c: DistanceY(g2,g2) = 4
    c: Tangent(g2,g-3)
    c: DistanceY(g1,g-3) = 2
FEATURE [Part::Extrusion] Extrude043  label="Extrude scavo saldature alimentatore connettore 5v"
  Base = -> Sketch040
  Dir = (0,-1,2e-16)
  DirMode = 2
  FaceMakerClass = Part::FaceMakerBullseye
  FaceMakerMode = 3
  LengthFwd = 8
  LengthRev = 0
  Solid = true
  Symmetric = true
FEATURE [Sketcher::SketchObject] Sketch041  label="scavo saldature alimentatore connettore 5v verticali"
  ArcFitTolerance = 1e-06
  AttachmentSupport = -> [XZ_Plane]
  ExternalGeometry = -> [Sketch037]
  FullyConstrained = true
  MakeInternals = false
  MapMode = 5
  Placement = pos=(0,0,0) rot=(1,0,0;1.5708rad)
  sketch-geometry (4):
    g0: LineSegment StartX=-211.175 StartY=-53.6316 StartZ=0 EndX=-209.575 EndY=-53.6316 EndZ=0
    g1: LineSegment StartX=-209.575 StartY=-53.6316 StartZ=0 EndX=-209.575 EndY=-76.6316 EndZ=0
    g2: LineSegment StartX=-209.575 StartY=-76.6316 StartZ=0 EndX=-211.175 EndY=-76.6316 EndZ=0
    g3: LineSegment StartX=-211.175 StartY=-76.6316 StartZ=0 EndX=-211.175 EndY=-53.6316 EndZ=0
  constraints (11):
    c: Horizontal(g0)
    c: Coincident(g1,g0)
    c: Coincident(g2,g1)
    c: Horizontal(g2)
    c: Coincident(g3,g2)
    c: Coincident(g3,g0)
    c: Vertical(g3)
    c: DistanceY(g3,g3) = 23
    c: DistanceX(g0,g0) = 1.6
    c: Tangent(g1,g-3)
    c: DistanceY(g0,g-3) = 3.2
FEATURE [Part::Extrusion] Extrude044  label="Extrude scavo saldature alimentatore connettore 5v verticali"
  Base = -> Sketch041
  Dir = (0,-1,2e-16)
  DirMode = 2
  FaceMakerClass = Part::FaceMakerBullseye
  FaceMakerMode = 3
  LengthFwd = 3.2
  LengthRev = 0
  Placement = pos=(0,8.3,0) rot=(0,0,1;0rad)
  Solid = true
  Symmetric = false
FEATURE [Sketcher::SketchObject] Sketch042  label="fermi per driver solenoide e alimentatore"
  ArcFitTolerance = 1e-06
  AttachmentSupport = -> [XZ_Plane]
  ExternalGeometry = -> [Sketch036,Sketch037,Sketch,Sketch038]
  FullyConstrained = true
  MakeInternals = false
  MapMode = 5
  Placement = pos=(0,0,0) rot=(1,0,0;1.5708rad)
  sketch-geometry (27):
    g0: LineSegment StartX=-195.773 StartY=-15.631 StartZ=0 EndX=-196.702 EndY=-17.6249 EndZ=0
    g1: LineSegment StartX=-196.702 StartY=-17.6249 StartZ=0 EndX=-194.709 EndY=-18.5546 EndZ=0
    g2: LineSegment StartX=-194.709 StartY=-18.5546 StartZ=0 EndX=-193.779 EndY=-16.5607 EndZ=0
    g3: LineSegment StartX=-193.779 StartY=-16.5607 StartZ=0 EndX=-195.773 EndY=-15.631 EndZ=0
    g4: LineSegment StartX=-196.547 StartY=-13.5047 StartZ=0 EndX=-198.829 EndY=-18.3988 EndZ=0
    g5: LineSegment StartX=-198.829 StartY=-18.3988 StartZ=0 EndX=-195.385 EndY=-20.0047 EndZ=0
    g6: LineSegment StartX=-193.258 StartY=-19.2308 StartZ=0 EndX=-192.329 EndY=-17.2369 EndZ=0
    g7: LineSegment StartX=-193.103 StartY=-15.1106 StartZ=0 EndX=-196.547 EndY=-13.5047 EndZ=0
    g8: LineSegment [constr] StartX=-193.935 StartY=-20.6809 StartZ=0 EndX=-193.258 EndY=-19.2308 EndZ=0
    g9: LineSegment [constr] StartX=-193.935 StartY=-20.6809 StartZ=0 EndX=-195.385 EndY=-20.0047 EndZ=0
    g10: ArcOfCircle CenterX=-193.779 CenterY=-16.5607 CenterZ=0 NormalX=0 NormalY=0 NormalZ=1 AngleXU=0 Radius=1.6 StartAngle=5.84685 EndAngle=7.41765
    g11: GeomPoint [constr] X=-191.653 Y=-15.7868 Z=0
    g12: ArcOfCircle CenterX=-194.709 CenterY=-18.5546 CenterZ=0 NormalX=0 NormalY=0 NormalZ=1 AngleXU=0 Radius=1.6 StartAngle=4.27606 EndAngle=5.84685
    g13: GeomPoint [constr] X=-193.935 Y=-20.6809 Z=0
    g14: LineSegment StartX=-207.775 StartY=-46.8316 StartZ=0 EndX=-207.775 EndY=-50.8316 EndZ=0
    g15: LineSegment StartX=-207.775 StartY=-46.8316 StartZ=0 EndX=-203.775 EndY=-46.8316 EndZ=0
    g16: LineSegment StartX=-203.775 StartY=-46.8316 StartZ=0 EndX=-203.775 EndY=-50.8316 EndZ=0
    g17: LineSegment StartX=-207.775 StartY=-50.8316 StartZ=0 EndX=-203.775 EndY=-50.8316 EndZ=0
    g18: LineSegment StartX=-209.375 StartY=-52.4316 StartZ=0 EndX=-203.775 EndY=-52.4316 EndZ=0
    g19: LineSegment StartX=-202.175 StartY=-50.8316 StartZ=0 EndX=-202.175 EndY=-46.8316 EndZ=0
    g20: LineSegment StartX=-203.775 StartY=-45.2316 StartZ=0 EndX=-209.375 EndY=-45.2316 EndZ=0
    g21: LineSegment StartX=-209.375 StartY=-45.2316 StartZ=0 EndX=-209.375 EndY=-52.4316 EndZ=0
    g22: ArcOfCircle CenterX=-203.775 CenterY=-46.8316 CenterZ=0 NormalX=0 NormalY=0 NormalZ=1 AngleXU=0 Radius=1.6 StartAngle=1.8e-15 EndAngle=1.5708
    g23: GeomPoint [constr] X=-202.175 Y=-45.2316 Z=0
    g24: ArcOfCircle CenterX=-203.775 CenterY=-50.8316 CenterZ=0 NormalX=0 NormalY=0 NormalZ=1 AngleXU=0 Radius=1.6 StartAngle=4.71239 EndAngle=6.28319
    g25: GeomPoint [constr] X=-202.175 Y=-52.4316 Z=0
    g26: LineSegment [constr] StartX=-207.775 StartY=-50.4316 StartZ=0 EndX=-207.775 EndY=-50.8316 EndZ=0
  constraints (69):
    c: Coincident(g1,g0)
    c: Coincident(g2,g1)
    c: Coincident(g3,g2)
    c: Coincident(g3,g0)
    c: Parallel(g0,g2)
    c: Perpendicular(g3,g0)
    c: Perpendicular(g1,g0)
    c: Coincident(g5,g4)
    c: Coincident(g7,g4)
    c: Distance(g3) = 2.2
    c: Distance(g2) = 2.2
    c: Parallel(g6,g2)
    c: Parallel(g6,g4)
    c: Perpendicular(g5,g6)
    c: Perpendicular(g7,g6)
    c: Distance(g13,g11) = 5.4
    c: Distance(g5,g13) = 5.4
    c: Coincident(g9,g8)
    c: Distance(g8) = 1.6
    c: Distance(g9) = 1.6
    c: Perpendicular(g9,g8)
    c: Parallel(g8,g6)
    c: Coincident(g8,g13)
    c: Distance(g8,g1) = 1.6
    c: Distance(g9,g1) = 1.6
    c: Tangent(g0,g-5)
    c: Distance(g0,g-6) = 26.2
    c: PointOnObject(g11,g7)
    c: PointOnObject(g11,g6)
    c: Tangent(g7,g10) = -1.5708
    c: Tangent(g6,g10) = -1.5708
    c: PointOnObject(g13,g5)
    c: Tangent(g5,g12) = -1.5708
    c: Tangent(g6,g12) = -1.5708
    c: Equal(g10,g12)
    c: Coincident(g10,g2)
    c: Vertical(g14)
    c: Coincident(g15,g14)
    c: Horizontal(g15)
    c: Coincident(g16,g15)
    c: Vertical(g16)
    c: Coincident(g17,g14)
    c: Coincident(g17,g16)
    c: Horizontal(g17)
    c: Distance(g16) = 4
    c: Distance(g15) = 4
    c: Horizontal(g18)
    c: Vertical(g19)
    c: Horizontal(g20)
    c: Coincident(g21,g20)
    c: Coincident(g21,g18)
    c: Vertical(g21)
    c: Distance(g20,g23) = 7.2
    c: Distance(g25,g23) = 7.2
    c: DistanceY(g18,g14) = 1.6
    c: DistanceX(g18,g14) = 1.6
    c: PointOnObject(g23,g20)
    c: PointOnObject(g23,g19)
    c: Tangent(g20,g22) = -1.5708
    c: Tangent(g19,g22) = -1.5708
    c: PointOnObject(g25,g19)
    c: Tangent(g18,g24) = -1.5708
    c: Tangent(g19,g24) = -1.5708
    c: Equal(g22,g24)
    c: Coincident(g22,g15)
    c: Vertical(g26)
    c: Distance(g26) = 0.4
    c: Coincident(g26,g-4)
    c: Coincident(g14,g26)
FEATURE [Part::Extrusion] Extrude045  label="Extrude fermi per driver solenoide e alimentatore"
  Base = -> Sketch042
  Dir = (0,-1,2e-16)
  DirMode = 2
  FaceMakerClass = Part::FaceMakerBullseye
  FaceMakerMode = 3
  LengthFwd = 25.2
  LengthRev = 0
  Solid = true
  Symmetric = true
FEATURE [Sketcher::SketchObject] Sketch043  label="scavo pulizia fermo alimentatore"
  ArcFitTolerance = 1e-06
  AttachmentSupport = -> [XZ_Plane]
  ExternalGeometry = -> [Sketch042,Sketch036,Sketch037]
  FullyConstrained = true
  MakeInternals = false
  MapMode = 5
  Placement = pos=(0,0,0) rot=(1,0,0;1.5708rad)
  sketch-geometry (6):
    g0: LineSegment StartX=-209.375 StartY=-52.4316 StartZ=0 EndX=-209.375 EndY=-50.4316 EndZ=0
    g1: LineSegment StartX=-209.375 StartY=-50.4316 StartZ=0 EndX=-207.775 EndY=-50.4316 EndZ=0
    g2: LineSegment StartX=-207.775 StartY=-50.4316 StartZ=0 EndX=-207.775 EndY=-45.2316 EndZ=0
    g3: LineSegment StartX=-207.775 StartY=-45.2316 StartZ=0 EndX=-202.175 EndY=-45.2316 EndZ=0
    g4: LineSegment StartX=-202.175 StartY=-45.2316 StartZ=0 EndX=-202.175 EndY=-52.4316 EndZ=0
    g5: LineSegment StartX=-202.175 StartY=-52.4316 StartZ=0 EndX=-209.375 EndY=-52.4316 EndZ=0
  constraints (13):
    c: Vertical(g0)
    c: Coincident(g1,g0)
    c: Coincident(g2,g1)
    c: Coincident(g3,g2)
    c: Coincident(g4,g3)
    c: Coincident(g5,g4)
    c: Coincident(g5,g0)
    c: Horizontal(g5)
    c: Coincident(g0,g-6)
    c: Tangent(g1,g-8)
    c: Tangent(g2,g-4)
    c: Tangent(g3,g-7)
    c: Tangent(g4,g-3)
FEATURE [Part::Extrusion] Extrude046  label="Extrude scavo pulizia fermo alimentatore"
  Base = -> Sketch043
  Dir = (0,-1,2e-16)
  DirMode = 2
  FaceMakerClass = Part::FaceMakerBullseye
  FaceMakerMode = 3
  LengthFwd = 19.5
  LengthRev = 0
  Solid = true
  Symmetric = true
FEATURE [Sketcher::SketchObject] Sketch044  label="buchini per fissaggio oled"
  ArcFitTolerance = 1e-06
  AttachmentSupport = -> [YZ_Plane]
  ExternalGeometry = -> [Sketch]
  FullyConstrained = true
  MakeInternals = false
  MapMode = 5
  Placement = pos=(0,0,0) rot=(0.57735,0.57735,0.57735;2.0944rad)
  sketch-geometry (5):
    g0: LineSegment [constr] StartX=1.5e-14 StartY=67.3588 StartZ=0 EndX=0 EndY=64.3588 EndZ=0
    g1: LineSegment [constr] StartX=0 StartY=64.3588 StartZ=0 EndX=10.4 EndY=64.3588 EndZ=0
    g2: LineSegment [constr] StartX=0 StartY=64.3588 StartZ=0 EndX=-10.4 EndY=64.3588 EndZ=0
    g3: Circle CenterX=10.4 CenterY=64.3588 CenterZ=0 NormalX=0 NormalY=0 NormalZ=1 AngleXU=0 Radius=1.5
    g4: Circle CenterX=-10.4 CenterY=64.3588 CenterZ=0 NormalX=0 NormalY=0 NormalZ=1 AngleXU=0 Radius=1.5
  constraints (13):
    c: Distance(g0) = 3
    c: PointOnObject(g0,g-2)
    c: Coincident(g1,g0)
    c: Horizontal(g1)
    c: Coincident(g2,g0)
    c: Horizontal(g2)
    c: DistanceX(g1,g1) = 10.4
    c: Coincident(g3,g1)
    c: Diameter(g4) = 3
    c: Coincident(g4,g2)
    c: Coincident(g0,g-7)
    c: Equal(g1,g2)
    c: Equal(g4,g3)
FEATURE [Part::Extrusion] Extrude047  label="Extrude buchini per fissaggio oled"
  Base = -> Sketch044
  Dir = (1,0,0)
  DirMode = 2
  FaceMakerClass = Part::FaceMakerBullseye
  FaceMakerMode = 3
  LengthFwd = 10
  LengthRev = 0
  Placement = pos=(-186,0,0) rot=(0,0,1;0rad)
  Solid = true
  Symmetric = false
FEATURE [Sketcher::SketchObject] Sketch046  label="scavo 5x5 neopixel"
  ArcFitTolerance = 1e-06
  AttachmentSupport = -> [YZ_Plane002]
  FullyConstrained = true
  MakeInternals = false
  MapMode = 5
  Placement = pos=(0,0,0) rot=(0.57735,0.57735,0.57735;2.0944rad)
  sketch-geometry (4):
    g0: LineSegment StartX=-2.7 StartY=2.7 StartZ=0 EndX=2.7 EndY=2.7 EndZ=0
    g1: LineSegment StartX=2.7 StartY=2.7 StartZ=0 EndX=2.7 EndY=-2.7 EndZ=0
    g2: LineSegment StartX=2.7 StartY=-2.7 StartZ=0 EndX=-2.7 EndY=-2.7 EndZ=0
    g3: LineSegment StartX=-2.7 StartY=-2.7 StartZ=0 EndX=-2.7 EndY=2.7 EndZ=0
  constraints (11):
    c: Horizontal(g0)
    c: Coincident(g1,g0)
    c: Vertical(g1)
    c: Coincident(g2,g1)
    c: Horizontal(g2)
    c: Coincident(g3,g2)
    c: Coincident(g3,g0)
    c: Vertical(g3)
    c: DistanceX(g0,g0) = 5.4
    c: DistanceY(g1,g1) = 5.4
    c: Symmetric(g0,g1,g-1)
FEATURE [Part::Extrusion] Extrude049  label="Extrude scavo 5x5 neopixel"
  Base = -> Sketch046
  Dir = (1,0,0)
  DirMode = 2
  FaceMakerClass = Part::FaceMakerBullseye
  FaceMakerMode = 3
  LengthFwd = 1
  LengthRev = 0
  Solid = true
  Symmetric = false
FEATURE [Sketcher::SketchObject] Sketch047  label="scavo 10x10 neopixel corpo"
  ArcFitTolerance = 1e-06
  AttachmentSupport = -> [YZ_Plane002]
  FullyConstrained = true
  MakeInternals = false
  MapMode = 5
  Placement = pos=(0,0,0) rot=(0.57735,0.57735,0.57735;2.0944rad)
  sketch-geometry (4):
    g0: LineSegment StartX=-5 StartY=5.1 StartZ=0 EndX=5 EndY=5.1 EndZ=0
    g1: LineSegment StartX=5 StartY=5.1 StartZ=0 EndX=5 EndY=-5.1 EndZ=0
    g2: LineSegment StartX=5 StartY=-5.1 StartZ=0 EndX=-5 EndY=-5.1 EndZ=0
    g3: LineSegment StartX=-5 StartY=-5.1 StartZ=0 EndX=-5 EndY=5.1 EndZ=0
  constraints (11):
    c: Horizontal(g0)
    c: Coincident(g1,g0)
    c: Vertical(g1)
    c: Coincident(g2,g1)
    c: Horizontal(g2)
    c: Coincident(g3,g2)
    c: Coincident(g3,g0)
    c: Vertical(g3)
    c: DistanceX(g0,g0) = 10
    c: DistanceY(g1,g1) = 10.2
    c: Symmetric(g0,g2,g-1)
FEATURE [Part::Extrusion] Extrude050  label="Extrude scavo 10x10 neopixel corpo"
  Base = -> Sketch047
  Dir = (1,0,0)
  DirMode = 2
  FaceMakerClass = Part::FaceMakerBullseye
  FaceMakerMode = 3
  LengthFwd = 8
  LengthRev = 0
  Placement = pos=(1,0,0) rot=(0,0,1;0rad)
  Solid = true
  Symmetric = false
FEATURE [Sketcher::SketchObject] Sketch048  label="buco per perno blocco neopixel"
  ArcFitTolerance = 1e-06
  AttachmentSupport = -> [XZ_Plane002]
  FullyConstrained = true
  MakeInternals = false
  MapMode = 5
  Placement = pos=(0,0,0) rot=(1,0,0;1.5708rad)
  sketch-geometry (4):
    g0: LineSegment StartX=3 StartY=1.2 StartZ=0 EndX=3 EndY=-1.2 EndZ=0
    g1: LineSegment StartX=3 StartY=-1.2 StartZ=0 EndX=5.4 EndY=-1.2 EndZ=0
    g2: LineSegment StartX=5.4 StartY=-1.2 StartZ=0 EndX=5.4 EndY=1.2 EndZ=0
    g3: LineSegment StartX=5.4 StartY=1.2 StartZ=0 EndX=3 EndY=1.2 EndZ=0
  constraints (11):
    c: Coincident(g1,g0)
    c: Horizontal(g1)
    c: Coincident(g2,g1)
    c: Vertical(g2)
    c: Coincident(g3,g2)
    c: Coincident(g3,g0)
    c: Horizontal(g3)
    c: DistanceX(g1,g1) = 2.4
    c: DistanceY(g2,g2) = 2.4
    c: Symmetric(g0,g0,g-1)
    c: DistanceX(g-1,g0) = 3
FEATURE [Sketcher::SketchObject] Sketch045  label="blocco principale per neopixel"
  ArcFitTolerance = 1e-06
  AttachmentSupport = -> [XZ_Plane002]
  ExternalGeometry = -> [Sketch048]
  FullyConstrained = true
  MakeInternals = false
  MapMode = 5
  Placement = pos=(0,0,0) rot=(1,0,0;1.5708rad)
  sketch-geometry (6):
    g0: LineSegment StartX=0 StartY=5.1 StartZ=0 EndX=0 EndY=-5.1 EndZ=0
    g1: LineSegment StartX=0 StartY=-5.1 StartZ=0 EndX=3 EndY=-5.1 EndZ=0
    g2: LineSegment StartX=7 StartY=-1.1 StartZ=0 EndX=7 EndY=5.1 EndZ=0
    g3: LineSegment StartX=7 StartY=5.1 StartZ=0 EndX=0 EndY=5.1 EndZ=0
    g4: ArcOfCircle CenterX=3 CenterY=-1.1 CenterZ=0 NormalX=0 NormalY=0 NormalZ=1 AngleXU=0 Radius=4 StartAngle=4.71239 EndAngle=6.28319
    g5: GeomPoint [constr] X=7 Y=-5.1 Z=0
  constraints (15):
    c: Vertical(g0)
    c: Coincident(g1,g0)
    c: Horizontal(g1)
    c: Vertical(g2)
    c: Coincident(g3,g2)
    c: Coincident(g3,g0)
    c: Horizontal(g3)
    c: DistanceY(g0,g0) = 10.2
    c: Symmetric(g0,g0,g-1)
    c: DistanceX(g3,g3) = 7
    c: PointOnObject(g5,g2)
    c: PointOnObject(g5,g1)
    c: Tangent(g2,g4) = -1.5708
    c: Tangent(g1,g4) = -1.5708
    c: DistanceX(g-3,g1) = 0
FEATURE [Part::Extrusion] Extrude048  label="Extrude blocco principale per neopixel"
  Base = -> Sketch045
  Dir = (0,-1,2e-16)
  DirMode = 2
  FaceMakerClass = Part::FaceMakerBullseye
  FaceMakerMode = 3
  LengthFwd = 17
  LengthRev = 0
  Solid = true
  Symmetric = true
FEATURE [Part::Extrusion] Extrude051  label="Extrude buco per perno blocco neopixel"
  Base = -> Sketch048
  Dir = (0,-1,2e-16)
  DirMode = 2
  FaceMakerClass = Part::FaceMakerBullseye
  FaceMakerMode = 3
  LengthFwd = 17
  LengthRev = 0
  Solid = true
  Symmetric = true
FEATURE [Sketcher::SketchObject] Sketch049  label="rinforzi esterni per corpo neopoixel"
  ArcFitTolerance = 1e-06
  AttachmentSupport = -> [XZ_Plane002]
  ExternalGeometry = -> [Sketch045]
  FullyConstrained = true
  MakeInternals = false
  MapMode = 5
  Placement = pos=(0,0,0) rot=(1,0,0;1.5708rad)
  sketch-geometry (8):
    g0: LineSegment StartX=1 StartY=-4.1 StartZ=0 EndX=2 EndY=-4.1 EndZ=0
    g1: LineSegment StartX=2 StartY=-4.1 StartZ=0 EndX=2 EndY=-5.1 EndZ=0
    g2: LineSegment StartX=2 StartY=-5.1 StartZ=0 EndX=1 EndY=-5.1 EndZ=0
    g3: LineSegment StartX=1 StartY=-5.1 StartZ=0 EndX=1 EndY=-4.1 EndZ=0
    g4: LineSegment StartX=1 StartY=5.1 StartZ=0 EndX=2 EndY=5.1 EndZ=0
    g5: LineSegment StartX=2 StartY=5.1 StartZ=0 EndX=2 EndY=4.1 EndZ=0
    g6: LineSegment StartX=2 StartY=4.1 StartZ=0 EndX=1 EndY=4.1 EndZ=0
    g7: LineSegment StartX=1 StartY=4.1 StartZ=0 EndX=1 EndY=5.1 EndZ=0
  constraints (24):
    c: Horizontal(g0)
    c: Coincident(g1,g0)
    c: Vertical(g1)
    c: Coincident(g2,g1)
    c: Horizontal(g2)
    c: Coincident(g3,g2)
    c: Coincident(g3,g0)
    c: Vertical(g3)
    c: Horizontal(g4)
    c: Coincident(g5,g4)
    c: Vertical(g5)
    c: Coincident(g6,g5)
    c: Horizontal(g6)
    c: Coincident(g7,g6)
    c: Coincident(g7,g4)
    c: Vertical(g7)
    c: DistanceX(g4,g4) = 1
    c: DistanceY(g5,g5) = 1
    c: DistanceX(g0,g0) = 1
    c: DistanceY(g1,g1) = 1
    c: DistanceX(g-3,g4) = 1
    c: DistanceY(g-3,g4) = 0
    c: DistanceX(g-4,g2) = 1
    c: DistanceY(g2,g-4) = 0
FEATURE [Part::Extrusion] Extrude052  label="Extrude rinforzi esterni per corpo neopoixel"
  Base = -> Sketch049
  Dir = (0,-1,2e-16)
  DirMode = 2
  FaceMakerClass = Part::FaceMakerBullseye
  FaceMakerMode = 3
  LengthFwd = 17
  LengthRev = 0
  Solid = true
  Symmetric = true
FEATURE [Part::Cut] Cut030
  Base = -> Extrude048
  Refine = true
  Tool = -> Extrude050
FEATURE [Part::Cut] Cut031
  Base = -> Cut030
  Refine = true
  Tool = -> Extrude049
FEATURE [Part::Cut] Cut032
  Base = -> Cut031
  Refine = true
  Tool = -> Extrude051
FEATURE [Part::MultiFuse] Fusion001  label="fusion neopixel"
  Refine = true
  Shapes = -> [Cut032,Extrude052]
FEATURE [Sketcher::SketchObject] Sketch052  label="scavo saldature driver solenoide"
  ArcFitTolerance = 1e-06
  AttachmentSupport = -> [XZ_Plane]
  ExternalGeometry = -> [Sketch038]
  FullyConstrained = true
  MakeInternals = false
  MapMode = 5
  Placement = pos=(0,0,0) rot=(1,0,0;1.5708rad)
  sketch-geometry (4):
    g0: LineSegment StartX=-196.56 StartY=-9.74706 StartZ=0 EndX=-198.25 EndY=-13.3723 EndZ=0
    g1: LineSegment StartX=-198.25 StartY=-13.3723 StartZ=0 EndX=-196.8 EndY=-14.0485 EndZ=0
    g2: LineSegment StartX=-196.8 StartY=-14.0485 StartZ=0 EndX=-195.11 EndY=-10.4232 EndZ=0
    g3: LineSegment StartX=-195.11 StartY=-10.4232 StartZ=0 EndX=-196.56 EndY=-9.74706 EndZ=0
  constraints (11):
    c: Coincident(g1,g0)
    c: Coincident(g2,g1)
    c: Coincident(g3,g2)
    c: Coincident(g3,g0)
    c: Parallel(g2,g0)
    c: Perpendicular(g2,g3)
    c: Perpendicular(g1,g2,g1) = 1.5708
    c: Parallel(g2,g-3)
    c: Distance(g2) = 4
    c: Distance(g3) = 1.6
    c: Coincident(g2,g-3)
FEATURE [Part::Extrusion] Extrude055  label="Extrude scavo saldature driver solenoide"
  Base = -> Sketch052
  Dir = (0,-1,2e-16)
  DirMode = 2
  FaceMakerClass = Part::FaceMakerBullseye
  FaceMakerMode = 3
  LengthFwd = 6
  LengthRev = 0
  Solid = true
  Symmetric = true
FEATURE [Sketcher::SketchObject] Sketch053  label="scavo saldature rumble"
  ArcFitTolerance = 1e-06
  AttachmentSupport = -> [XZ_Plane]
  ExternalGeometry = -> [Sketch019]
  FullyConstrained = true
  MakeInternals = false
  MapMode = 5
  Placement = pos=(0,0,0) rot=(1,0,0;1.5708rad)
  sketch-geometry (4):
    g0: LineSegment StartX=-165.31 StartY=-44.1173 StartZ=0 EndX=-166.547 EndY=-47.9216 EndZ=0
    g1: LineSegment StartX=-166.547 StartY=-47.9216 StartZ=0 EndX=-165.405 EndY=-48.2924 EndZ=0
    g2: LineSegment StartX=-165.405 StartY=-48.2924 StartZ=0 EndX=-164.169 EndY=-44.4881 EndZ=0
    g3: LineSegment StartX=-164.169 StartY=-44.4881 StartZ=0 EndX=-165.31 EndY=-44.1173 EndZ=0
  constraints (11):
    c: Coincident(g1,g0)
    c: Coincident(g2,g1)
    c: Coincident(g3,g2)
    c: Coincident(g3,g0)
    c: Parallel(g0,g2)
    c: Perpendicular(g3,g0)
    c: Perpendicular(g1,g0)
    c: Parallel(g0,g-3)
    c: Distance(g0) = 4
    c: Distance(g1) = 1.2
    c: Coincident(g0,g-3)
FEATURE [Part::Extrusion] Extrude056  label="Extrude scavo saldature rumble"
  Base = -> Sketch053
  Dir = (0,-1,2e-16)
  DirMode = 2
  FaceMakerClass = Part::FaceMakerBullseye
  FaceMakerMode = 3
  LengthFwd = 8.4
  LengthRev = 0
  Solid = true
  Symmetric = true
FEATURE [Part::Cone] Cone  label="Cono"
  Angle = 180
  AttacherType = Attacher::AttachEngine3D
  Height = 15
  Placement = pos=(-176,0,-82.43) rot=(0,0,1;-1.5708rad)
  Radius1 = 12.6
  Radius2 = 10.5
FEATURE [Sketcher::SketchObject] Sketch054  label="scavo saldature alimentatore connettore USB"
  ArcFitTolerance = 1e-06
  AttachmentSupport = -> [XZ_Plane]
  ExternalGeometry = -> [Sketch037]
  FullyConstrained = true
  MakeInternals = false
  MapMode = 5
  Placement = pos=(0,0,0) rot=(1,0,0;1.5708rad)
  sketch-geometry (4):
    g0: LineSegment StartX=-209.575 StartY=-80.4316 StartZ=0 EndX=-210.375 EndY=-80.4316 EndZ=0
    g1: LineSegment StartX=-210.375 StartY=-80.4316 StartZ=0 EndX=-210.375 EndY=-72.4316 EndZ=0
    g2: LineSegment StartX=-210.375 StartY=-72.4316 StartZ=0 EndX=-209.575 EndY=-72.4316 EndZ=0
    g3: LineSegment StartX=-209.575 StartY=-72.4316 StartZ=0 EndX=-209.575 EndY=-80.4316 EndZ=0
  constraints (11):
    c: Horizontal(g0)
    c: Coincident(g1,g0)
    c: Vertical(g1)
    c: Coincident(g2,g1)
    c: Horizontal(g2)
    c: Coincident(g3,g2)
    c: Coincident(g3,g0)
    c: Vertical(g3)
    c: DistanceX(g0,g0) = 0.8
    c: DistanceY(g3,g3) = 8
    c: Coincident(g0,g-4)
FEATURE [Part::Extrusion] Extrude057  label="Extrude scavo saldature alimentatore connettore USB"
  Base = -> Sketch054
  Dir = (0,-1,2e-16)
  DirMode = 2
  FaceMakerClass = Part::FaceMakerBullseye
  FaceMakerMode = 3
  LengthFwd = 11
  LengthRev = 0
  Solid = true
  Symmetric = true
FEATURE [Sketcher::SketchObject] Sketch055  label="buco interno per micro switch"
  ArcFitTolerance = 1e-06
  AttachmentSupport = -> [XZ_Plane]
  ExternalGeometry = -> [Sketch]
  FullyConstrained = true
  MakeInternals = false
  MapMode = 5
  Placement = pos=(0,0,0) rot=(1,0,0;1.5708rad)
  sketch-geometry (11):
    g0: LineSegment [constr] StartX=-194.483 StartY=34.2854 StartZ=0 EndX=-196.022 EndY=30.0568 EndZ=0
    g1: LineSegment [constr] StartX=-196.022 StartY=30.0568 StartZ=0 EndX=-197.561 EndY=25.8282 EndZ=0
    g2: LineSegment [constr] StartX=-196.022 StartY=30.0568 StartZ=0 EndX=-194.143 EndY=29.3727 EndZ=0
    g3: LineSegment [constr] StartX=-196.022 StartY=30.0568 StartZ=0 EndX=-197.902 EndY=30.7408 EndZ=0
    g4: LineSegment StartX=-196.362 StartY=34.9694 StartZ=0 EndX=-192.604 EndY=33.6014 EndZ=0
    g5: LineSegment StartX=-199.441 StartY=26.5122 StartZ=0 EndX=-195.682 EndY=25.1441 EndZ=0
    g6: LineSegment StartX=-192.604 StartY=33.6014 StartZ=0 EndX=-195.682 EndY=25.1441 EndZ=0
    g7: LineSegment StartX=-196.362 StartY=34.9694 StartZ=0 EndX=-199.441 EndY=26.5122 EndZ=0
    g8: GeomPoint [constr] X=-187.821 Y=29.2 Z=0
    g9: LineSegment [constr] StartX=-188.505 StartY=27.3206 StartZ=0 EndX=-196.022 EndY=30.0568 EndZ=0
    g10: LineSegment [constr] StartX=-187.821 StartY=29.2 StartZ=0 EndX=-188.505 EndY=27.3206 EndZ=0
  constraints (27):
    c: Coincident(g2,g0)
    c: Parallel(g0,g-3)
    c: Tangent(g1,g0) = -1.5708
    c: Perpendicular(g0,g2)
    c: Tangent(g2,g3)
    c: Distance(g0,g1) = 9
    c: Equal(g0,g1)
    c: Distance(g3,g2) = 4
    c: Equal(g2,g3)
    c: Parallel(g3,g4)
    c: Symmetric(g4,g4,g0)
    c: Parallel(g6,g1)
    c: Parallel(g7,g1)
    c: Symmetric(g6,g6,g2)
    c: Symmetric(g5,g5,g1)
    c: Symmetric(g7,g7,g3)
    c: Coincident(g7,g4)
    c: Coincident(g6,g4)
    c: Coincident(g5,g6)
    c: Symmetric(g-3,g-3,g8)
    c: Perpendicular(g-3,g9)
    c: Distance(g9) = 8
    c: Coincident(g3,g9)
    c: Coincident(g10,g8)
    c: Parallel(g10,g-3)
    c: Distance(g10) = 2
    c: Coincident(g10,g9)
FEATURE [Part::Extrusion] Extrude058  label="Extrude buco interno per micro switch sinistro"
  Base = -> Sketch055
  Dir = (0,-1,2e-16)
  DirMode = 2
  FaceMakerClass = Part::FaceMakerBullseye
  FaceMakerMode = 3
  LengthFwd = 9
  LengthRev = 0
  Placement = pos=(0,10.6,0) rot=(0,0,1;0rad)
  Solid = true
  Symmetric = false
FEATURE [Sketcher::SketchObject] Sketch056  label="buco esterno per micro switch"
  ArcFitTolerance = 1e-06
  AttachmentSupport = -> [XZ_Plane]
  ExternalGeometry = -> [Sketch055]
  FullyConstrained = true
  MakeInternals = false
  MapMode = 5
  Placement = pos=(0,0,0) rot=(1,0,0;1.5708rad)
  sketch-geometry (17):
    g0: GeomPoint [constr] X=-194.143 Y=29.3727 Z=0
    g1: GeomPoint [constr] X=-194.483 Y=34.2854 Z=0
    g2: GeomPoint [constr] X=-197.902 Y=30.7408 Z=0
    g3: GeomPoint [constr] X=-197.561 Y=25.8282 Z=0
    g4: GeomPoint [constr] X=-196.022 Y=30.0568 Z=0
    g5: LineSegment [constr] StartX=-194.483 StartY=34.2854 StartZ=0 EndX=-196.022 EndY=30.0568 EndZ=0
    g6: LineSegment [constr] StartX=-196.022 StartY=30.0568 StartZ=0 EndX=-197.561 EndY=25.8282 EndZ=0
    g7: LineSegment [constr] StartX=-197.902 StartY=30.7408 StartZ=0 EndX=-196.022 EndY=30.0568 EndZ=0
    g8: LineSegment [constr] StartX=-196.022 StartY=30.0568 StartZ=0 EndX=-194.143 EndY=29.3727 EndZ=0
    g9: LineSegment [constr] StartX=-195.338 StartY=31.9362 StartZ=0 EndX=-196.022 EndY=30.0568 EndZ=0
    g10: LineSegment [constr] StartX=-196.022 StartY=30.0568 StartZ=0 EndX=-196.706 EndY=28.1774 EndZ=0
    g11: LineSegment [constr] StartX=-196.022 StartY=30.0568 StartZ=0 EndX=-196.821 EndY=30.3475 EndZ=0
    g12: LineSegment [constr] StartX=-196.022 StartY=30.0568 StartZ=0 EndX=-195.223 EndY=29.7661 EndZ=0
    g13: LineSegment StartX=-194.539 StartY=31.6454 StartZ=0 EndX=-195.907 EndY=27.8867 EndZ=0
    g14: LineSegment StartX=-196.137 StartY=32.2269 StartZ=0 EndX=-197.505 EndY=28.4681 EndZ=0
    g15: LineSegment StartX=-196.137 StartY=32.2269 StartZ=0 EndX=-194.539 EndY=31.6454 EndZ=0
    g16: LineSegment StartX=-197.505 StartY=28.4681 StartZ=0 EndX=-195.907 EndY=27.8867 EndZ=0
  constraints (34):
    c: Symmetric(g-5,g-5,g1)
    c: Symmetric(g-5,g-6,g0)
    c: Symmetric(g-6,g-6,g3)
    c: Symmetric(g-5,g-6,g2)
    c: Coincident(g5,g1)
    c: Coincident(g5,g4)
    c: Coincident(g6,g4)
    c: Coincident(g6,g3)
    c: Equal(g5,g6)
    c: Coincident(g7,g2)
    c: Coincident(g7,g4)
    c: Coincident(g8,g4)
    c: Coincident(g8,g0)
    c: Equal(g7,g8)
    c: Coincident(g11,g9)
    c: Coincident(g12,g9)
    c: Tangent(g10,g9) = -1.5708
    c: Perpendicular(g11,g9)
    c: Parallel(g9,g-4)
    c: Equal(g9,g10)
    c: Parallel(g12,g11)
    c: Equal(g11,g12)
    c: Distance(g11,g12) = 1.7
    c: Distance(g9,g10) = 4
    c: Symmetric(g13,g13,g12)
    c: Parallel(g13,g9)
    c: Symmetric(g14,g14,g11)
    c: Symmetric(g15,g15,g9)
    c: Parallel(g15,g11)
    c: Symmetric(g16,g16,g10)
    c: Coincident(g16,g14)
    c: Coincident(g15,g14)
    c: Coincident(g13,g15)
    c: Coincident(g9,g4)
FEATURE [Part::Extrusion] Extrude059  label="Extrude buco esterno per micro switch sinistro"
  Base = -> Sketch056
  Dir = (0,-1,2e-16)
  DirMode = 2
  FaceMakerClass = Part::FaceMakerBullseye
  FaceMakerMode = 3
  LengthFwd = 2
  LengthRev = 0
  Placement = pos=(0,12.6,0) rot=(0,0,1;0rad)
  Solid = true
  Symmetric = false
FEATURE [Sketcher::SketchObject] Sketch057  label="buco interno per SWITCH"
  ArcFitTolerance = 1e-06
  AttachmentSupport = -> [XZ_Plane]
  ExternalGeometry = -> [Sketch]
  FullyConstrained = true
  MakeInternals = false
  MapMode = 5
  Placement = pos=(0,0,0) rot=(1,0,0;1.5708rad)
  sketch-geometry (10):
    g0: GeomPoint [constr] X=-187.821 Y=29.2 Z=0
    g1: LineSegment [constr] StartX=-188.505 StartY=27.3206 StartZ=0 EndX=-193.203 EndY=29.0307 EndZ=0
    g2: LineSegment [constr] StartX=-190.809 StartY=35.6086 StartZ=0 EndX=-195.597 EndY=22.4529 EndZ=0
    g3: GeomPoint [constr] X=-193.203 Y=29.0307 Z=0
    g4: LineSegment [constr] StartX=-196.492 StartY=30.2278 StartZ=0 EndX=-189.914 EndY=27.8336 EndZ=0
    g5: LineSegment StartX=-194.098 StartY=36.8056 StartZ=0 EndX=-187.52 EndY=34.4115 EndZ=0
    g6: LineSegment StartX=-194.098 StartY=36.8056 StartZ=0 EndX=-198.886 EndY=23.6499 EndZ=0
    g7: LineSegment StartX=-187.52 StartY=34.4115 StartZ=0 EndX=-192.308 EndY=21.2558 EndZ=0
    g8: LineSegment StartX=-198.886 StartY=23.6499 StartZ=0 EndX=-192.308 EndY=21.2558 EndZ=0
    g9: LineSegment [constr] StartX=-187.821 StartY=29.2 StartZ=0 EndX=-188.505 EndY=27.3206 EndZ=0
  constraints (23):
    c: Symmetric(g-3,g-3,g0)
    c: Perpendicular(g1,g-3)
    c: Parallel(g2,g-3)
    c: Symmetric(g2,g2,g3)
    c: Perpendicular(g2,g4)
    c: Symmetric(g4,g4,g3)
    c: Distance(g2) = 14
    c: Distance(g4) = 7
    c: Distance(g1) = 5
    c: Parallel(g5,g4)
    c: Parallel(g7,g2)
    c: Symmetric(g5,g5,g2)
    c: Symmetric(g6,g6,g4)
    c: Symmetric(g7,g7,g4)
    c: Symmetric(g8,g8,g2)
    c: Coincident(g6,g5)
    c: Coincident(g7,g5)
    c: Coincident(g8,g7)
    c: Coincident(g3,g1)
    c: Coincident(g9,g0)
    c: Parallel(g9,g-3)
    c: Distance(g9) = 2
    c: Coincident(g1,g9)
FEATURE [Sketcher::SketchObject] Sketch058  label="buco esterno per SWITCH"
  ArcFitTolerance = 1e-06
  AttachmentSupport = -> [XZ_Plane]
  ExternalGeometry = -> [Sketch057]
  FullyConstrained = true
  MakeInternals = false
  MapMode = 5
  Placement = pos=(0,0,0) rot=(1,0,0;1.5708rad)
  sketch-geometry (12):
    g0: GeomPoint [constr] X=-190.809 Y=35.6086 Z=0
    g1: GeomPoint [constr] X=-196.492 Y=30.2278 Z=0
    g2: GeomPoint [constr] X=-189.914 Y=27.8336 Z=0
    g3: GeomPoint [constr] X=-195.597 Y=22.4529 Z=0
    g4: GeomPoint [constr] X=-193.203 Y=29.0307 Z=0
    g5: LineSegment [constr] StartX=-192.006 StartY=32.3196 StartZ=0 EndX=-194.4 EndY=25.7418 EndZ=0
    g6: GeomPoint [constr] X=-193.203 Y=29.0307 Z=0
    g7: LineSegment [constr] StartX=-195.082 StartY=29.7148 StartZ=0 EndX=-191.324 EndY=28.3467 EndZ=0
    g8: LineSegment StartX=-193.885 StartY=33.0037 StartZ=0 EndX=-190.127 EndY=31.6356 EndZ=0
    g9: LineSegment StartX=-190.127 StartY=31.6356 StartZ=0 EndX=-192.521 EndY=25.0578 EndZ=0
    g10: LineSegment StartX=-196.28 StartY=26.4258 StartZ=0 EndX=-192.521 EndY=25.0578 EndZ=0
    g11: LineSegment StartX=-193.885 StartY=33.0037 StartZ=0 EndX=-196.28 EndY=26.4258 EndZ=0
  constraints (21):
    c: Symmetric(g-6,g-6,g3)
    c: Symmetric(g-4,g-6,g2)
    c: Symmetric(g-5,g-4,g0)
    c: Symmetric(g-5,g-6,g1)
    c: Symmetric(g1,g2,g4)
    c: Parallel(g5,g-4)
    c: Symmetric(g5,g5,g6)
    c: Perpendicular(g7,g5)
    c: Symmetric(g7,g7,g6)
    c: Distance(g5) = 7
    c: Distance(g7) = 4
    c: Parallel(g8,g7)
    c: Parallel(g11,g5)
    c: Symmetric(g8,g8,g5)
    c: Symmetric(g9,g9,g7)
    c: Symmetric(g10,g10,g5)
    c: Symmetric(g11,g11,g7)
    c: Coincident(g11,g8)
    c: Coincident(g9,g8)
    c: Coincident(g9,g10)
    c: Coincident(g6,g4)
FEATURE [Part::Extrusion] Extrude060  label="Extrude buco interno per SWITCH destro"
  Base = -> Sketch057
  Dir = (0,-1,2e-16)
  DirMode = 2
  FaceMakerClass = Part::FaceMakerBullseye
  FaceMakerMode = 3
  LengthFwd = 13.2
  LengthRev = 0
  Placement = pos=(0,2.6,0) rot=(0,0,1;0rad)
  Solid = true
  Symmetric = false
FEATURE [Part::Extrusion] Extrude061  label="Extrude buco esterno per SWITCH destro"
  Base = -> Sketch058
  Dir = (0,-1,2e-16)
  DirMode = 2
  FaceMakerClass = Part::FaceMakerBullseye
  FaceMakerMode = 3
  LengthFwd = 2
  LengthRev = 0
  Placement = pos=(0,-10.6,0) rot=(0,0,1;0rad)
  Solid = true
  Symmetric = false
FEATURE [Sketcher::SketchObject] Sketch059  label="buco per spazio introduzione SWITCH"
  ArcFitTolerance = 1e-06
  AttachmentSupport = -> [XZ_Plane]
  ExternalGeometry = -> [Sketch057,Sketch010]
  FullyConstrained = true
  MakeInternals = false
  MapMode = 5
  Placement = pos=(0,0,0) rot=(1,0,0;1.5708rad)
  sketch-geometry (8):
    g0: LineSegment [constr] StartX=-201.368 StartY=36.3521 StartZ=0 EndX=-195.094 EndY=34.0687 EndZ=0
    g1: LineSegment [constr] StartX=-194.098 StartY=36.8056 StartZ=0 EndX=-195.094 EndY=34.0687 EndZ=0
    g2: LineSegment StartX=-198.658 StartY=24.2771 StartZ=0 EndX=-199.654 EndY=21.5401 EndZ=0
    g3: LineSegment StartX=-199.654 StartY=21.5401 StartZ=0 EndX=-181.196 EndY=14.822 EndZ=0
    g4: LineSegment StartX=-181.196 StartY=14.822 StartZ=0 EndX=-180.2 EndY=17.559 EndZ=0
    g5: LineSegment StartX=-180.2 StartY=17.559 StartZ=0 EndX=-198.658 EndY=24.2771 EndZ=0
    g6: LineSegment [constr] StartX=-204.932 StartY=26.5605 StartZ=0 EndX=-198.658 EndY=24.2771 EndZ=0
    g7: LineSegment [constr] StartX=-198.658 StartY=24.2771 StartZ=0 EndX=-199.654 EndY=21.5401 EndZ=0
  constraints (20):
    c: Parallel(g1,g-3)
    c: Parallel(g0,g-4)
    c: Coincident(g0,g-4)
    c: Coincident(g1,g-3)
    c: Coincident(g0,g1)
    c: Coincident(g3,g2)
    c: Coincident(g4,g3)
    c: Coincident(g5,g4)
    c: Coincident(g5,g2)
    c: Parallel(g5,g-5)
    c: Parallel(g3,g-5)
    c: Parallel(g4,g-6)
    c: DistanceX(g-6,g4) = 0
    c: Coincident(g6,g-5)
    c: Equal(g6,g0)
    c: Coincident(g7,g6)
    c: Equal(g7,g1)
    c: Tangent(g7,g-3)
    c: Coincident(g2,g6)
    c: Coincident(g2,g7)
FEATURE [Part::Extrusion] Extrude062  label="Extrude buco per spazio introduzione SWITCH"
  Base = -> Sketch059
  Dir = (0,-1,2e-16)
  DirMode = 2
  FaceMakerClass = Part::FaceMakerBullseye
  FaceMakerMode = 3
  LengthFwd = 13.2
  LengthRev = 0
  Solid = true
  Symmetric = true
FEATURE [Part::Extrusion] Extrude063  label="Extrude buco interno per SWITCH sinistro"
  Base = -> Sketch057
  Dir = (0,-1,2e-16)
  DirMode = 2
  FaceMakerClass = Part::FaceMakerBullseye
  FaceMakerMode = 3
  LengthFwd = 13.2
  LengthRev = 0
  Placement = pos=(0,10.6,0) rot=(0,0,1;0rad)
  Solid = true
  Symmetric = false
FEATURE [Part::Extrusion] Extrude064  label="Extrude buco esterno per SWITCH sinistro"
  Base = -> Sketch058
  Dir = (0,-1,2e-16)
  DirMode = 2
  FaceMakerClass = Part::FaceMakerBullseye
  FaceMakerMode = 3
  LengthFwd = 2
  LengthRev = 0
  Placement = pos=(0,12.6,0) rot=(0,0,1;0rad)
  Solid = true
  Symmetric = false
FEATURE [Sketcher::SketchObject] Sketch060  label="prova spazio switch"
  ArcFitTolerance = 1e-06
  AttachmentSupport = -> [XY_Plane003]
  FullyConstrained = true
  MakeInternals = false
  MapMode = 5
  sketch-geometry (12):
    g0: LineSegment StartX=-7.5 StartY=10 StartZ=0 EndX=-7.5 EndY=-10 EndZ=0
    g1: LineSegment StartX=-7.5 StartY=-10 StartZ=0 EndX=7.5 EndY=-10 EndZ=0
    g2: LineSegment StartX=7.5 StartY=-10 StartZ=0 EndX=7.5 EndY=10 EndZ=0
    g3: LineSegment StartX=7.5 StartY=10 StartZ=0 EndX=-7.5 EndY=10 EndZ=0
    g4: GeomPoint [constr] X=0 Y=0 Z=0
    g5: LineSegment StartX=-2.95 StartY=-5.55 StartZ=0 EndX=2.95 EndY=-5.55 EndZ=0
    g6: LineSegment StartX=2.95 StartY=-5.55 StartZ=0 EndX=2.95 EndY=5.55 EndZ=0
    g7: LineSegment StartX=2.95 StartY=5.55 StartZ=0 EndX=-2.95 EndY=5.55 EndZ=0
    g8: LineSegment StartX=-2.95 StartY=5.55 StartZ=0 EndX=-2.95 EndY=-5.55 EndZ=0
    g9: GeomPoint [constr] X=0 Y=0 Z=0
    g10: Circle CenterX=0 CenterY=7.75 CenterZ=0 NormalX=0 NormalY=0 NormalZ=1 AngleXU=0 Radius=1.6
    g11: Circle CenterX=0 CenterY=-7.75 CenterZ=0 NormalX=0 NormalY=0 NormalZ=1 AngleXU=0 Radius=1.6
  constraints (29):
    c: Coincident(g0,g1)
    c: Coincident(g1,g2)
    c: Coincident(g2,g3)
    c: Coincident(g3,g0)
    c: Vertical(g0)
    c: Vertical(g2)
    c: Horizontal(g1)
    c: Horizontal(g3)
    c: Symmetric(g2,g0,g4)
    c: Coincident(g4,g-1)
    c: Distance(g3) = 15
    c: Distance(g2) = 20
    c: Coincident(g5,g6)
    c: Coincident(g6,g7)
    c: Coincident(g7,g8)
    c: Coincident(g8,g5)
    c: Horizontal(g5)
    c: Horizontal(g7)
    c: Vertical(g6)
    c: Vertical(g8)
    c: Symmetric(g7,g5,g9)
    c: Coincident(g9,g4)
    c: Distance(g7) = 5.9
    c: Distance(g6) = 11.1
    c: Diameter(g10) = 3.2
    c: Equal(g10,g11)
    c: Symmetric(g10,g11,g-1)
    c: PointOnObject(g10,g-2)
    c: Distance(g10,g11) = 15.5
FEATURE [Part::Extrusion] Extrude065  label="Extrude prova spazio switch"
  Base = -> Sketch060
  Dir = (0,0,1)
  DirMode = 2
  FaceMakerClass = Part::FaceMakerBullseye
  FaceMakerMode = 3
  LengthFwd = 5
  LengthRev = 0
  Solid = true
  Symmetric = false
FEATURE [Sketcher::SketchObject] Sketch061  label="struttura esterna blocco switch"
  ArcFitTolerance = 1e-06
  AttachmentSupport = -> [XZ_Plane003]
  FullyConstrained = true
  MakeInternals = false
  MapMode = 5
  Placement = pos=(0,0,0) rot=(1,0,0;1.5708rad)
  sketch-geometry (5):
    g0: LineSegment StartX=-1 StartY=-5.1 StartZ=0 EndX=1 EndY=-5.1 EndZ=0
    g1: LineSegment StartX=1 StartY=-5.1 StartZ=0 EndX=1 EndY=5.1 EndZ=0
    g2: LineSegment StartX=1 StartY=5.1 StartZ=0 EndX=-1 EndY=5.1 EndZ=0
    g3: LineSegment StartX=-1 StartY=5.1 StartZ=0 EndX=-1 EndY=-5.1 EndZ=0
    g4: GeomPoint [constr] X=0 Y=0 Z=0
  constraints (12):
    c: Coincident(g0,g1)
    c: Coincident(g1,g2)
    c: Coincident(g2,g3)
    c: Coincident(g3,g0)
    c: Horizontal(g0)
    c: Horizontal(g2)
    c: Vertical(g1)
    c: Vertical(g3)
    c: Symmetric(g2,g0,g4)
    c: Distance(g1,g3) = 2
    c: Distance(g0,g2) = 10.2
    c: Coincident(g4,g-1)
FEATURE [Part::Extrusion] Extrude066  label="Extrude struttura esterna blocco switch"
  Base = -> Sketch061
  Dir = (0,-1,2e-16)
  DirMode = 2
  FaceMakerClass = Part::FaceMakerBullseye
  FaceMakerMode = 3
  LengthFwd = 16.8
  LengthRev = 0
  Solid = true
  Symmetric = true
FEATURE [Sketcher::SketchObject] Sketch062  label="struttura interna blocco switch"
  ArcFitTolerance = 1e-06
  AttachmentSupport = -> [XZ_Plane003]
  ExternalGeometry = -> [Sketch061]
  FullyConstrained = true
  MakeInternals = false
  MapMode = 5
  Placement = pos=(0,0,0) rot=(1,0,0;1.5708rad)
  sketch-geometry (5):
    g0: LineSegment StartX=-1 StartY=3.1 StartZ=0 EndX=-1 EndY=-3.1 EndZ=0
    g1: LineSegment StartX=-1 StartY=-3.1 StartZ=0 EndX=1 EndY=-3.1 EndZ=0
    g2: LineSegment StartX=1 StartY=-3.1 StartZ=0 EndX=1 EndY=3.1 EndZ=0
    g3: LineSegment StartX=1 StartY=3.1 StartZ=0 EndX=-1 EndY=3.1 EndZ=0
    g4: GeomPoint [constr] X=0 Y=0 Z=0
  constraints (12):
    c: Coincident(g0,g1)
    c: Coincident(g1,g2)
    c: Coincident(g2,g3)
    c: Coincident(g3,g0)
    c: Vertical(g0)
    c: Vertical(g2)
    c: Horizontal(g1)
    c: Horizontal(g3)
    c: Symmetric(g2,g0,g4)
    c: Coincident(g4,g-1)
    c: Distance(g0) = 6.2
    c: Equal(g3,g-3)
FEATURE [Part::Extrusion] Extrude067  label="Extrude struttura interna blocco switch"
  Base = -> Sketch062
  Dir = (0,-1,2e-16)
  DirMode = 2
  FaceMakerClass = Part::FaceMakerBullseye
  FaceMakerMode = 3
  LengthFwd = 12.8
  LengthRev = 0
  Solid = true
  Symmetric = true
FEATURE [Part::Cut] Cut036  label="struttura blocco switch"
  Base = -> Extrude066
  Refine = true
  Tool = -> Extrude067
FEATURE [Sketcher::SketchObject] Sketch063  label="blocchi tra switch"
  ArcFitTolerance = 1e-06
  AttachmentSupport = -> [XZ_Plane003]
  ExternalGeometry = -> [Sketch061,Sketch062]
  FullyConstrained = true
  MakeInternals = false
  MapMode = 5
  Placement = pos=(0,0,0) rot=(1,0,0;1.5708rad)
  sketch-geometry (8):
    g0: LineSegment StartX=-3 StartY=5.1 StartZ=0 EndX=-1 EndY=5.1 EndZ=0
    g1: LineSegment StartX=-1 StartY=5.1 StartZ=0 EndX=-1 EndY=3.1 EndZ=0
    g2: LineSegment StartX=-1 StartY=3.1 StartZ=0 EndX=-3 EndY=3.1 EndZ=0
    g3: LineSegment StartX=-3 StartY=3.1 StartZ=0 EndX=-3 EndY=5.1 EndZ=0
    g4: LineSegment StartX=-3 StartY=-3.1 StartZ=0 EndX=-1 EndY=-3.1 EndZ=0
    g5: LineSegment StartX=-1 StartY=-3.1 StartZ=0 EndX=-1 EndY=-5.1 EndZ=0
    g6: LineSegment StartX=-1 StartY=-5.1 StartZ=0 EndX=-3 EndY=-5.1 EndZ=0
    g7: LineSegment StartX=-3 StartY=-5.1 StartZ=0 EndX=-3 EndY=-3.1 EndZ=0
  constraints (20):
    c: Horizontal(g0)
    c: Coincident(g1,g0)
    c: Coincident(g2,g1)
    c: Horizontal(g2)
    c: Coincident(g3,g2)
    c: Coincident(g3,g0)
    c: Vertical(g3)
    c: Horizontal(g4)
    c: Coincident(g5,g4)
    c: Coincident(g6,g5)
    c: Horizontal(g6)
    c: Coincident(g7,g6)
    c: Coincident(g7,g4)
    c: Vertical(g7)
    c: Coincident(g0,g-4)
    c: Coincident(g1,g-5)
    c: Coincident(g4,g-6)
    c: Coincident(g5,g-7)
    c: Distance(g0) = 2
    c: Distance(g4) = 2
FEATURE [PartDesign::Body] Body003  label="blocco switch e neopixel"
  AllowCompound = false
  Group = -> [Sketch060,Sketch061,Sketch062,Sketch063]
  Origin = -> Origin003
FEATURE [Part::Extrusion] Extrude068  label="Extrude blocchi tra switch"
  Base = -> Sketch063
  Dir = (0,-1,2e-16)
  DirMode = 2
  FaceMakerClass = Part::FaceMakerBullseye
  FaceMakerMode = 3
  LengthFwd = 7.6
  LengthRev = 0
  Solid = true
  Symmetric = true
FEATURE [Part::MultiFuse] Fusion002  label="Fusion blocco switch"
  Refine = true
  Shapes = -> [Cut036,Extrude068]
FEATURE [Sketcher::SketchObject] Sketch066  label="piano per rampino"
  ArcFitTolerance = 1e-06
  AttachmentSupport = -> [XZ_Plane002]
  ExternalGeometry = -> [Sketch045]
  FullyConstrained = true
  MakeInternals = false
  MapMode = 5
  Placement = pos=(0,0,0) rot=(1,0,0;1.5708rad)
  sketch-geometry (4):
    g0: LineSegment StartX=5.4 StartY=5.1 StartZ=0 EndX=5.4 EndY=3.9 EndZ=0
    g1: LineSegment StartX=5.4 StartY=3.9 StartZ=0 EndX=7 EndY=3.9 EndZ=0
    g2: LineSegment StartX=7 StartY=3.9 StartZ=0 EndX=7 EndY=5.1 EndZ=0
    g3: LineSegment StartX=7 StartY=5.1 StartZ=0 EndX=5.4 EndY=5.1 EndZ=0
  constraints (11):
    c: Coincident(g0,g1)
    c: Coincident(g1,g2)
    c: Coincident(g2,g3)
    c: Coincident(g3,g0)
    c: Vertical(g0)
    c: Vertical(g2)
    c: Horizontal(g1)
    c: Horizontal(g3)
    c: Distance(g0,g2) = 1.6
    c: Distance(g1,g3) = 1.2
    c: Coincident(g2,g-3)
FEATURE [Sketcher::SketchObject] Sketch064  label="rampini_per_serraggio_struttura"
  ArcFitTolerance = 1e-06
  AttachmentSupport = -> [XZ_Plane002]
  ExternalGeometry = -> [Sketch066,Sketch045]
  FullyConstrained = true
  MakeInternals = false
  MapMode = 5
  Placement = pos=(0,0,0) rot=(1,0,0;1.5708rad)
  sketch-geometry (7):
    g0: LineSegment StartX=7 StartY=5.1 StartZ=0 EndX=7 EndY=3.9 EndZ=0
    g1: LineSegment StartX=7 StartY=3.9 StartZ=0 EndX=9 EndY=3.9 EndZ=0
    g2: LineSegment StartX=7 StartY=5.1 StartZ=0 EndX=7 EndY=5.1 EndZ=0
    g3: LineSegment StartX=7 StartY=5.1 StartZ=0 EndX=7 EndY=7.5 EndZ=0
    g4: LineSegment StartX=9 StartY=5.1 StartZ=0 EndX=9 EndY=3.9 EndZ=0
    g5: LineSegment StartX=7 StartY=7.5 StartZ=0 EndX=9 EndY=7.5 EndZ=0
    g6: LineSegment StartX=9 StartY=7.5 StartZ=0 EndX=9 EndY=5.1 EndZ=0
  constraints (20):
    c: Vertical(g0)
    c: Coincident(g1,g0)
    c: Horizontal(g1)
    c: Coincident(g2,g0)
    c: Horizontal(g2)
    c: Coincident(g3,g2)
    c: Vertical(g3)
    c: Coincident(g5,g3)
    c: Coincident(g4,g6)
    c: Coincident(g4,g1)
    c: Vertical(g4)
    c: Coincident(g0,g-3)
    c: DistanceY(g-4,g3) = 2.4
    c: DistanceX(g1,g1) = 2
    c: DistanceY(g2,g6) = 0
    c: DistanceX(g2,g2) = 0
    c: DistanceY(g0,g0) = 1.2
    c: Coincident(g5,g6)
    c: Horizontal(g5)
    c: Vertical(g6)
FEATURE [Part::Extrusion] Extrude070  label="Extrude piano per rampino"
  Base = -> Sketch066
  Dir = (0,-1,2e-16)
  DirMode = 2
  FaceMakerClass = Part::FaceMakerBullseye
  FaceMakerMode = 3
  LengthFwd = 17
  LengthRev = 0
  Solid = true
  Symmetric = true
FEATURE [Part::Extrusion] Extrude071  label="Extrude rampini_per_serraggio_struttura"
  Base = -> Sketch064
  Dir = (0,-1,2e-16)
  DirMode = 2
  FaceMakerClass = Part::FaceMakerBullseye
  FaceMakerMode = 3
  LengthFwd = 5
  LengthRev = 0
  Solid = true
  Symmetric = true
FEATURE [Part::MultiFuse] Fusion003  label="Fusion supporto neopixel completo"
  Refine = true
  Shapes = -> [Fusion001,Extrude070,Extrude071]
FEATURE [Sketcher::SketchObject] Sketch067  label="perno per blocco switch"
  ArcFitTolerance = 1e-06
  AttachmentSupport = -> [XZ_Plane]
  ExternalGeometry = -> [Sketch,Sketch010]
  FullyConstrained = true
  MakeInternals = false
  MapMode = 5
  Placement = pos=(0,0,0) rot=(1,0,0;1.5708rad)
  sketch-geometry (14):
    g0: LineSegment StartX=-191.073 StartY=24.9429 StartZ=0 EndX=-185.81 EndY=23.0276 EndZ=0
    g1: LineSegment StartX=-183.76 StartY=23.9839 StartZ=0 EndX=-182.392 EndY=27.7427 EndZ=0
    g2: LineSegment StartX=-183.348 StartY=29.7934 StartZ=0 EndX=-188.61 EndY=31.7087 EndZ=0
    g3: LineSegment StartX=-188.61 StartY=31.7087 StartZ=0 EndX=-191.073 EndY=24.9429 EndZ=0
    g4: GeomPoint [constr] X=-186.459 Y=27.0946 Z=0
    g5: LineSegment StartX=-189.022 StartY=25.8992 StartZ=0 EndX=-185.263 EndY=24.5311 EndZ=0
    g6: LineSegment StartX=-185.263 StartY=24.5311 StartZ=0 EndX=-183.895 EndY=28.2899 EndZ=0
    g7: LineSegment StartX=-183.895 StartY=28.2899 StartZ=0 EndX=-187.654 EndY=29.658 EndZ=0
    g8: LineSegment StartX=-187.654 StartY=29.658 StartZ=0 EndX=-189.022 EndY=25.8992 EndZ=0
    g9: GeomPoint [constr] X=-186.459 Y=27.0946 Z=0
    g10: ArcOfCircle CenterX=-185.263 CenterY=24.5311 CenterZ=0 NormalX=0 NormalY=0 NormalZ=1 AngleXU=0 Radius=1.6 StartAngle=4.36332 EndAngle=5.93412
    g11: GeomPoint [constr] X=-184.307 Y=22.4804 Z=0
    g12: ArcOfCircle CenterX=-183.895 CenterY=28.2899 CenterZ=0 NormalX=0 NormalY=0 NormalZ=1 AngleXU=0 Radius=1.6 StartAngle=5.93412 EndAngle=7.50492
    g13: GeomPoint [constr] X=-181.844 Y=29.2462 Z=0
  constraints (30):
    c: Coincident(g2,g3)
    c: Coincident(g3,g0)
    c: Symmetric(g13,g0,g4)
    c: Distance(g11,g3) = 7.2
    c: Distance(g0,g2) = 7.2
    c: Parallel(g3,g1)
    c: Parallel(g2,g0)
    c: Perpendicular(g2,g3)
    c: Coincident(g5,g6)
    c: Coincident(g6,g7)
    c: Coincident(g7,g8)
    c: Coincident(g8,g5)
    c: Symmetric(g7,g5,g9)
    c: Distance(g6,g8) = 4
    c: Distance(g5,g7) = 4
    c: Coincident(g9,g4)
    c: Parallel(g8,g6)
    c: Parallel(g7,g5)
    c: Perpendicular(g7,g8)
    c: Tangent(g8,g-3)
    c: Tangent(g2,g-4)
    c: PointOnObject(g11,g1)
    c: PointOnObject(g11,g0)
    c: Tangent(g1,g10) = -1.5708
    c: Tangent(g0,g10) = -1.5708
    c: PointOnObject(g13,g1)
    c: Tangent(g1,g12) = -1.5708
    c: Tangent(g2,g12) = -1.5708
    c: Equal(g10,g12)
    c: Coincident(g10,g5)
FEATURE [Part::Extrusion] Extrude072  label="Extrude perno per blocco switch"
  Base = -> Sketch067
  Dir = (0,-1,2e-16)
  DirMode = 2
  FaceMakerClass = Part::FaceMakerBullseye
  FaceMakerMode = 3
  LengthFwd = 25.2
  LengthRev = 0
  Solid = true
  Symmetric = true
FEATURE [Part::MultiFuse] Fusion
  Refine = true
  Shapes = -> [Extrude,Sweep,Extrude007,Extrude011,Extrude005,Extrude012,Extrude013,Extrude016,Extrude031,Extrude039,Extrude045,Extrude072]
FEATURE [Part::Cut] Cut
  Base = -> Fusion
  Refine = true
  Tool = -> Extrude001
FEATURE [Part::Cut] Cut001
  Base = -> Cut
  Refine = true
  Tool = -> Extrude004
FEATURE [Part::Cut] Cut002
  Base = -> Cut001
  Refine = true
  Tool = -> Extrude006
FEATURE [Part::Cut] Cut003
  Base = -> Cut002
  Refine = true
  Tool = -> Extrude008
FEATURE [Part::Cut] Cut004
  Base = -> Cut003
  Refine = true
  Tool = -> Extrude009
FEATURE [Part::Cut] Cut005
  Base = -> Cut004
  Refine = true
  Tool = -> Extrude010
FEATURE [Part::Cut] Cut006
  Base = -> Cut005
  Refine = true
  Tool = -> Extrude014
FEATURE [Part::Cut] Cut007
  Base = -> Cut006
  Refine = true
  Tool = -> Extrude015
FEATURE [Part::Cut] Cut008
  Base = -> Cut007
  Refine = true
  Tool = -> Extrude018
FEATURE [Part::Cut] Cut009
  Base = -> Cut008
  Refine = true
  Tool = -> Extrude019
FEATURE [Part::Cut] Cut010
  Base = -> Cut009
  Refine = true
  Tool = -> Extrude020
FEATURE [Part::Cut] Cut011
  Base = -> Cut010
  Refine = true
  Tool = -> Extrude021
FEATURE [Part::Cut] Cut012
  Base = -> Cut011
  Refine = true
  Tool = -> Extrude022
FEATURE [Part::Cut] Cut013
  Base = -> Cut012
  Refine = true
  Tool = -> Extrude023
FEATURE [Part::Cut] Cut014
  Base = -> Cut013
  Refine = true
  Tool = -> Extrude032
FEATURE [Part::Cut] Cut015
  Base = -> Cut014
  Refine = true
  Tool = -> Extrude033
FEATURE [Part::Cut] Cut016
  Base = -> Cut015
  Refine = true
  Tool = -> Extrude034
FEATURE [Part::Cut] Cut017
  Base = -> Cut016
  Refine = true
  Tool = -> Extrude035
FEATURE [Part::Cut] Cut018
  Base = -> Cut017
  Refine = true
  Tool = -> Extrude036
FEATURE [Part::Cut] Cut019
  Base = -> Cut018
  Refine = true
  Tool = -> Extrude037
FEATURE [Part::Cut] Cut020
  Base = -> Cut019
  Refine = true
  Tool = -> Extrude030
FEATURE [Part::Cut] Cut022
  Base = -> Cut020
  Refine = true
  Tool = -> Extrude038
FEATURE [Part::Cut] Cut023
  Base = -> Cut022
  Refine = true
  Tool = -> Extrude041
FEATURE [Part::Cut] Cut024
  Base = -> Cut023
  Refine = true
  Tool = -> Extrude040
FEATURE [Part::Cut] Cut025
  Base = -> Cut024
  Refine = true
  Tool = -> Extrude042
FEATURE [Part::Cut] Cut026
  Base = -> Cut025
  Refine = true
  Tool = -> Extrude043
FEATURE [Part::Cut] Cut027
  Base = -> Cut026
  Refine = true
  Tool = -> Extrude044
FEATURE [Part::Cut] Cut028
  Base = -> Cut027
  Refine = true
  Tool = -> Extrude046
FEATURE [Part::Cut] Cut029
  Base = -> Cut028
  Refine = true
  Tool = -> Extrude047
FEATURE [Part::Cut] Cut033
  Base = -> Cut029
  Refine = true
  Tool = -> Extrude055
FEATURE [Part::Cut] Cut034
  Base = -> Cut033
  Refine = true
  Tool = -> Extrude056
FEATURE [Part::Cut] Cut035
  Base = -> Cut034
  Refine = true
  Tool = -> Extrude057
FEATURE [Part::Cut] Cut037
  Base = -> Cut035
  Refine = true
  Tool = -> Extrude060
FEATURE [Part::Cut] Cut038
  Base = -> Cut037
  Refine = true
  Tool = -> Extrude061
FEATURE [Part::Cut] Cut039
  Base = -> Cut038
  Refine = true
  Tool = -> Extrude063
FEATURE [Part::Cut] Cut040
  Base = -> Cut039
  Refine = true
  Tool = -> Extrude064
FEATURE [Part::Cut] Cut041
  Base = -> Cut040
  Refine = true
  Tool = -> Extrude062
FEATURE [Sketcher::SketchObject] Sketch068  label="base con smusso sopra neopixel"
  ArcFitTolerance = 1e-06
  AttachmentSupport = -> [YZ_Plane002]
  FullyConstrained = true
  MakeInternals = false
  MapMode = 5
  Placement = pos=(0,0,0) rot=(0.57735,0.57735,0.57735;2.0944rad)
  sketch-geometry (5):
    g0: LineSegment StartX=-9.5 StartY=-6.1 StartZ=0 EndX=9.5 EndY=-6.1 EndZ=0
    g1: LineSegment StartX=9.5 StartY=-6.1 StartZ=0 EndX=9.5 EndY=6.1 EndZ=0
    g2: LineSegment StartX=9.5 StartY=6.1 StartZ=0 EndX=-9.5 EndY=6.1 EndZ=0
    g3: LineSegment StartX=-9.5 StartY=6.1 StartZ=0 EndX=-9.5 EndY=-6.1 EndZ=0
    g4: GeomPoint [constr] X=0 Y=0 Z=0
  constraints (12):
    c: Coincident(g0,g1)
    c: Coincident(g1,g2)
    c: Coincident(g2,g3)
    c: Coincident(g3,g0)
    c: Horizontal(g0)
    c: Horizontal(g2)
    c: Vertical(g1)
    c: Vertical(g3)
    c: Symmetric(g2,g0,g4)
    c: Distance(g1,g3) = 19
    c: Distance(g0,g2) = 12.2
    c: Coincident(g4,g-1)
FEATURE [PartDesign::Body] Body002  label="supporto per neopixel"
  AllowCompound = false
  Group = -> [Sketch045,Sketch046,Sketch047,Sketch048,Sketch049,Sketch064,Sketch066,Sketch068]
  Origin = -> Origin002
FEATURE [Part::Extrusion] Extrude073  label="Extrude base con smusso sopra neopixel"
  Base = -> Sketch068
  Dir = (1,0,0)
  DirMode = 2
  FaceMakerClass = Part::FaceMakerBullseye
  FaceMakerMode = 3
  LengthFwd = -1
  LengthRev = 0
  Solid = true
  Symmetric = false
FEATURE [Part::Chamfer] Chamfer  label="Chamfer frontale supporto neopixel da fondere al supporto"
  Base = -> Extrude073
  EdgeLinks = -> Extrude073 [Edge4,Edge7,Edge10,Edge12]
  Edges = 4 edges r=0.5: [Edge4,Edge7,Edge10,Edge12]
FEATURE [Sketcher::SketchObject] Sketch069  label="cilindro minore"
  ArcFitTolerance = 1e-06
  AttachmentSupport = -> [XZ_Plane004]
  FullyConstrained = true
  MakeInternals = false
  MapMode = 5
  Placement = pos=(0,0,0) rot=(1,0,0;1.5708rad)
  sketch-geometry (1):
    g0: Circle CenterX=0 CenterY=0 CenterZ=0 NormalX=0 NormalY=0 NormalZ=1 AngleXU=0 Radius=5.8
  constraints (2):
    c: Diameter(g0) = 11.6
    c: Coincident(g0,g-1)
FEATURE [Sketcher::SketchObject] Sketch070  label="cilindro maggiore"
  ArcFitTolerance = 1e-06
  AttachmentSupport = -> [XZ_Plane004]
  ExternalGeometry = -> [Sketch069]
  FullyConstrained = true
  MakeInternals = false
  MapMode = 5
  Placement = pos=(0,0,0) rot=(1,0,0;1.5708rad)
  sketch-geometry (1):
    g0: Circle CenterX=0 CenterY=0 CenterZ=0 NormalX=0 NormalY=0 NormalZ=1 AngleXU=0 Radius=6.5
  constraints (2):
    c: Coincident(g0,g-1)
    c: Diameter(g0) = 13
FEATURE [Sketcher::SketchObject] Sketch071  label="buco interno"
  ArcFitTolerance = 1e-06
  AttachmentSupport = -> [XZ_Plane004]
  ExternalGeometry = -> [Sketch069]
  FullyConstrained = true
  MakeInternals = false
  MapMode = 5
  Placement = pos=(0,0,0) rot=(1,0,0;1.5708rad)
  sketch-geometry (1):
    g0: Circle CenterX=0 CenterY=0 CenterZ=0 NormalX=0 NormalY=0 NormalZ=1 AngleXU=0 Radius=5
  constraints (2):
    c: Coincident(g0,g-1)
    c: Diameter(g0) = 10
FEATURE [PartDesign::Pad] Pad
  Direction = (0,-1,2e-16)
  Length = 1.2
  Length2 = 10
  Placement = pos=(0,0,0) rot=(1,0,0;1.5708rad)
  Profile = -> Sketch070
  ReferenceAxis = -> Sketch070 [N_Axis]
  Refine = true
  Suppressed = false
  Type = 0
FEATURE [PartDesign::Pad] Pad001
  BaseFeature = -> Pad
  Direction = (0,-1,2e-16)
  Length = 5.6
  Length2 = 10
  Placement = pos=(0,0,0) rot=(1,0,0;1.5708rad)
  Profile = -> Sketch069
  ReferenceAxis = -> Sketch069 [N_Axis]
  Refine = true
  Suppressed = false
  Type = 0
FEATURE [PartDesign::Pocket] Pocket
  BaseFeature = -> Pad001
  Direction = (0,1,-2e-16)
  Length = 7
  Length2 = 5
  Midplane = true
  Placement = pos=(0,0,0) rot=(1,0,0;1.5708rad)
  Profile = -> Sketch071
  ReferenceAxis = -> Sketch071 [N_Axis]
  Refine = true
  Suppressed = false
  Type = 0
FEATURE [PartDesign::Fillet] Fillet
  Base = -> Pocket [Face7]
  BaseFeature = -> Pocket
  Placement = pos=(0,0,0) rot=(1,0,0;1.5708rad)
  Radius = 1
  Refine = true
  SupportTransform = false
  Suppressed = false
  UseAllEdges = false
FEATURE [PartDesign::Body] Body004  label="pulsanti lato sinistro"
  AllowCompound = false
  Group = -> [Sketch069,Sketch070,Sketch071,Pad,Pad001,Pocket,Fillet]
  Origin = -> Origin004
  Tip = -> Fillet
FEATURE [Sketcher::SketchObject] Sketch072  label="buco per saldature e diodo driver solenoide"
  ArcFitTolerance = 1e-06
  AttachmentSupport = -> [XZ_Plane]
  ExternalGeometry = -> [Sketch038]
  FullyConstrained = true
  MakeInternals = false
  MapMode = 5
  Placement = pos=(0,0,0) rot=(1,0,0;1.5708rad)
  sketch-geometry (4):
    g0: LineSegment StartX=-209.225 StartY=-40.6939 StartZ=0 EndX=-204.154 EndY=-29.8182 EndZ=0
    g1: LineSegment StartX=-204.154 StartY=-29.8182 StartZ=0 EndX=-206.51 EndY=-28.7194 EndZ=0
    g2: LineSegment StartX=-206.51 StartY=-28.7194 StartZ=0 EndX=-211.582 EndY=-39.5951 EndZ=0
    g3: LineSegment StartX=-211.582 StartY=-39.5951 StartZ=0 EndX=-209.225 EndY=-40.6939 EndZ=0
  constraints (11):
    c: Coincident(g1,g0)
    c: Coincident(g2,g1)
    c: Coincident(g3,g2)
    c: Coincident(g3,g0)
    c: Parallel(g-3,g0)
    c: Parallel(g0,g2)
    c: Perpendicular(g0,g3)
    c: Perpendicular(g1,g0)
    c: Distance(g3) = 2.6
    c: Distance(g2) = 12
    c: Coincident(g0,g-3)
FEATURE [Part::Extrusion] Extrude074  label="Extrude buco per saldature e diodo driver solenoide"
  Base = -> Sketch072
  Dir = (0,-1,2e-16)
  DirMode = 2
  FaceMakerClass = Part::FaceMakerBullseye
  FaceMakerMode = 3
  LengthFwd = 14.6
  LengthRev = 0
  Solid = true
  Symmetric = true
FEATURE [Part::Cut] Cut042
  Base = -> Cut041
  Refine = true
  Tool = -> Extrude074
FEATURE [Sketcher::SketchObject] Sketch073  label="fori slargati blocco solenoide"
  ArcFitTolerance = 1e-06
  AttachmentSupport = -> [XY_Plane]
  ExternalGeometry = -> [Sketch030]
  FullyConstrained = true
  MakeInternals = false
  MapMode = 5
  sketch-geometry (2):
    g0: Circle CenterX=-152.209 CenterY=6.95 CenterZ=0 NormalX=0 NormalY=0 NormalZ=1 AngleXU=0 Radius=3.7
    g1: Circle CenterX=-130.41 CenterY=-6.95 CenterZ=0 NormalX=0 NormalY=0 NormalZ=1 AngleXU=0 Radius=3.7
  constraints (4):
    c: Diameter(g0) = 7.4
    c: Coincident(g0,g-3)
    c: Diameter(g1) = 7.4
    c: Coincident(g1,g-4)
FEATURE [Part::Extrusion] Extrude075  label="Extrude fori slargati blocco solenoide"
  Base = -> Sketch073
  Dir = (0,0,1)
  DirMode = 2
  FaceMakerClass = Part::FaceMakerBullseye
  FaceMakerMode = 3
  LengthFwd = 1.5
  LengthRev = 0
  Placement = pos=(0,0,36.4) rot=(0,0,1;0rad)
  Solid = true
  Symmetric = false
FEATURE [Part::Cut] Cut043
  Base = -> Cut042
  Refine = true
  Tool = -> Extrude075
FEATURE [Sketcher::SketchObject] Sketch074  label="lato sx pistola"
  ArcFitTolerance = 1e-06
  AttachmentSupport = -> [XZ_Plane]
  ExternalGeometry = -> [Sketch016,Sketch,Sketch058]
  FullyConstrained = true
  MakeInternals = false
  MapMode = 5
  Placement = pos=(0,0,0) rot=(1,0,0;1.5708rad)
  sketch-geometry (37):
    g0: LineSegment StartX=-82.8 StartY=3.2 StartZ=0 EndX=0 EndY=3.2 EndZ=0
    g1: LineSegment StartX=-82.8 StartY=3.2 StartZ=0 EndX=-82.8 EndY=6.2 EndZ=0
    g2: LineSegment [constr] StartX=-107.6 StartY=18 StartZ=0 EndX=-107.6 EndY=20 EndZ=0
    g3: LineSegment [constr] StartX=-132.428 StartY=18 StartZ=0 EndX=-132.428 EndY=20 EndZ=0
    g4: LineSegment StartX=-132.428 StartY=20 StartZ=0 EndX=-107.6 EndY=20 EndZ=0
    g5: ArcOfCircle CenterX=-107.6 CenterY=4 CenterZ=0 NormalX=0 NormalY=0 NormalZ=1 AngleXU=0 Radius=16 StartAngle=0.137937 EndAngle=1.5708
    g6: LineSegment StartX=-82.8 StartY=6.2 StartZ=0 EndX=-91.752 EndY=6.2 EndZ=0
    g7: LineSegment [constr] StartX=-145.743 StartY=8.32624 StartZ=0 EndX=-147.645 EndY=8.94427 EndZ=0
    g8: ArcOfCircle CenterX=-132.428 CenterY=4 CenterZ=0 NormalX=0 NormalY=0 NormalZ=1 AngleXU=0 Radius=16 StartAngle=1.5708 EndAngle=2.82743
    g9: LineSegment StartX=-215.932 StartY=-80.4316 StartZ=0 EndX=-176.685 EndY=-80.4316 EndZ=0
    g10: LineSegment StartX=-147.645 StartY=8.94427 StartZ=0 EndX=-176.685 EndY=-80.4316 EndZ=0
    g11: LineSegment [constr] StartX=-193.988 StartY=-2.33927 StartZ=0 EndX=-192.176 EndY=-3.18451 EndZ=0
    g12: LineSegment [constr] StartX=-217.232 StartY=-52.1862 StartZ=0 EndX=-215.42 EndY=-53.0314 EndZ=0
    g13: LineSegment StartX=-192.176 StartY=-3.18451 StartZ=0 EndX=-215.42 EndY=-53.0314 EndZ=0
    g14: ArcOfCircle CenterX=-184.801 CenterY=-67.3089 CenterZ=0 NormalX=0 NormalY=0 NormalZ=1 AngleXU=0 Radius=33.7833 StartAngle=2.70526 EndAngle=3.54053
    g15: ArcOfCircle CenterX=-207.583 CenterY=4 CenterZ=0 NormalX=0 NormalY=0 NormalZ=1 AngleXU=0 Radius=17 StartAngle=5.84685 EndAngle=7.56663
    g16: LineSegment StartX=-202.765 StartY=20.303 StartZ=0 EndX=-195.887 EndY=39.2 EndZ=0
    g17: LineSegment [constr] StartX=-193.885 StartY=33.0037 StartZ=0 EndX=-197.644 EndY=34.3718 EndZ=0
    g18: LineSegment StartX=-195.887 StartY=39.2 StartZ=0 EndX=0 EndY=39.2 EndZ=0
    g19: LineSegment StartX=0 StartY=3.2 StartZ=0 EndX=0 EndY=39.2 EndZ=0
    g20: LineSegment StartX=-189.939 StartY=31.5672 StartZ=0 EndX=-192.333 EndY=24.9893 EndZ=0
    g21: LineSegment StartX=-196.467 StartY=26.4942 StartZ=0 EndX=-194.073 EndY=33.0721 EndZ=0
    g22: Circle CenterX=-213.443 CenterY=-76.8316 CenterZ=0 NormalX=0 NormalY=0 NormalZ=1 AngleXU=0 Radius=1.8
    g23: Circle CenterX=-179.305 CenterY=-76.8316 CenterZ=0 NormalX=0 NormalY=0 NormalZ=1 AngleXU=0 Radius=1.8
    g24: Circle CenterX=-184.08 CenterY=34.8 CenterZ=0 NormalX=0 NormalY=0 NormalZ=1 AngleXU=0 Radius=1.8
    g25: Circle CenterX=-78.51 CenterY=34.8 CenterZ=0 NormalX=0 NormalY=0 NormalZ=1 AngleXU=0 Radius=1.8
    g26: Circle CenterX=-78.51 CenterY=7.6 CenterZ=0 NormalX=0 NormalY=0 NormalZ=1 AngleXU=0 Radius=1.8
    g27: Circle CenterX=-5.6 CenterY=34.8 CenterZ=0 NormalX=0 NormalY=0 NormalZ=1 AngleXU=0 Radius=1.8
    g28: Circle CenterX=-5.6 CenterY=7.6 CenterZ=0 NormalX=0 NormalY=0 NormalZ=1 AngleXU=0 Radius=1.8
    g29: LineSegment StartX=-190.127 StartY=31.6356 StartZ=0 EndX=-189.939 EndY=31.5672 EndZ=0
    g30: LineSegment StartX=-194.073 StartY=33.0721 StartZ=0 EndX=-193.885 EndY=33.0037 EndZ=0
    g31: LineSegment StartX=-193.885 StartY=33.0037 StartZ=0 EndX=-190.127 EndY=31.6356 EndZ=0
    g32: LineSegment StartX=-196.467 StartY=26.4942 StartZ=0 EndX=-192.333 EndY=24.9893 EndZ=0
    g33: Circle CenterX=-19 CenterY=21.2 CenterZ=0 NormalX=0 NormalY=0 NormalZ=1 AngleXU=0 Radius=6.3
    g34: Circle CenterX=-42 CenterY=21.2 CenterZ=0 NormalX=0 NormalY=0 NormalZ=1 AngleXU=0 Radius=6.3
    g35: Circle CenterX=-65 CenterY=21.2 CenterZ=0 NormalX=0 NormalY=0 NormalZ=1 AngleXU=0 Radius=6.3
    g36: LineSegment [constr] StartX=-4 StartY=21.2 StartZ=0 EndX=-65 EndY=21.2 EndZ=0
  constraints (96):
    c: Coincident(g0,g-41)
    c: Horizontal(g0)
    c: PointOnObject(g0,g-39)
    c: Coincident(g1,g0)
    c: Vertical(g1)
    c: DistanceY(g1,g1) = 3
    c: Coincident(g2,g-17)
    c: Vertical(g2)
    c: Coincident(g3,g-16)
    c: Vertical(g3)
    c: DistanceY(g2,g2) = 2
    c: DistanceY(g3,g3) = 2
    c: Coincident(g4,g3)
    c: Coincident(g4,g2)
    c: Coincident(g5,g-17)
    c: Coincident(g5,g2)
    c: Coincident(g6,g1)
    c: Horizontal(g6)
    c: Coincident(g6,g5)
    c: Coincident(g7,g-15)
    c: Coincident(g8,g7)
    c: Coincident(g8,g3)
    c: Coincident(g8,g-15)
    c: Horizontal(g9)
    c: DistanceY(g-13,g9) = 2
    c: Coincident(g10,g7)
    c: Parallel(g10,g-14)
    c: Coincident(g9,g10)
    c: Distance(g11) = 2
    c: Coincident(g11,g-11)
    c: Perpendicular(g-11,g11)
    c: Distance(g12) = 2
    c: Coincident(g12,g-12)
    c: Perpendicular(g-11,g12)
    c: Coincident(g13,g11)
    c: Coincident(g13,g12)
    c: Coincident(g14,g-32)
    c: Coincident(g14,g12)
    c: Coincident(g14,g9)
    c: Coincident(g15,g-10)
    c: Coincident(g15,g11)
    c: Parallel(g16,g-22)
    c: Distance(g17) = 4
    c: PointOnObject(g17,g16)
    c: Coincident(g15,g16)
    c: Horizontal(g18)
    c: Coincident(g18,g16)
    c: Coincident(g19,g0)
    c: PointOnObject(g19,g-39)
    c: DistanceY(g19,g-36) = 2
    c: Coincident(g18,g19)
    c: Diameter(g22) = 3.6
    c: Coincident(g22,g-9)
    c: Diameter(g23) = 3.6
    c: Coincident(g23,g-8)
    c: Diameter(g24) = 3.6
    c: Diameter(g25) = 3.6
    c: Diameter(g26) = 3.6
    c: Diameter(g27) = 3.6
    c: Diameter(g28) = 3.6
    c: Coincident(g27,g-4)
    c: Coincident(g28,g-3)
    c: Coincident(g25,g-6)
    c: Coincident(g26,g-5)
    c: Coincident(g24,g-7)
    c: Parallel(g20,g-21)
    c: Equal(g20,g-21)
    c: Parallel(g21,g-19)
    c: Equal(g21,g-19)
    c: Distance(g29) = 0.2
    c: Distance(g30) = 0.2
    c: Parallel(g29,g-20)
    c: Parallel(g31,g-20)
    c: Equal(g31,g-20)
    c: Coincident(g30,g31)
    c: Coincident(g31,g29)
    c: Coincident(g29,g-21)
    c: Parallel(g30,g31)
    c: Coincident(g17,g30)
    c: Coincident(g20,g29)
    c: Coincident(g21,g30)
    c: Perpendicular(g16,g17)
    c: Coincident(g32,g21)
    c: Coincident(g32,g20)
    c: Perpendicular(g10,g7)
    c: Diameter(g33) = 12.6
    c: Diameter(g34) = 12.6
    c: Diameter(g35) = 12.6
    c: Horizontal(g36)
    c: PointOnObject(g33,g36)
    c: PointOnObject(g34,g36)
    c: DistanceX(g34,g33) = 23
    c: DistanceX(g35,g34) = 23
    c: DistanceX(g33,g36) = 15
    c: Symmetric(g-24,g-24,g36)
    c: Coincident(g36,g35)
FEATURE [Part::Extrusion] Extrude076  label="Extrude lato sx pistola"
  Base = -> Sketch074
  Dir = (0,-1,2e-16)
  DirMode = 2
  FaceMakerClass = Part::FaceMakerBullseye
  FaceMakerMode = 3
  LengthFwd = -2
  LengthRev = 0
  Solid = true
  Symmetric = false
FEATURE [Sketcher::SketchObject] Sketch075  label="lato dx pistola"
  ArcFitTolerance = 1e-06
  AttachmentSupport = -> [XZ_Plane]
  ExternalGeometry = -> [Sketch016,Sketch,Sketch058,Sketch074]
  FullyConstrained = true
  MakeInternals = false
  MapMode = 5
  Placement = pos=(0,0,0) rot=(1,0,0;1.5708rad)
  sketch-geometry (61):
    g0: LineSegment StartX=-82.8 StartY=3.2 StartZ=0 EndX=0 EndY=3.2 EndZ=0
    g1: LineSegment StartX=-82.8 StartY=3.2 StartZ=0 EndX=-82.8 EndY=6.2 EndZ=0
    g2: LineSegment [constr] StartX=-107.6 StartY=18 StartZ=0 EndX=-107.6 EndY=20 EndZ=0
    g3: LineSegment [constr] StartX=-132.428 StartY=18 StartZ=0 EndX=-132.428 EndY=20 EndZ=0
    g4: LineSegment StartX=-132.428 StartY=20 StartZ=0 EndX=-107.6 EndY=20 EndZ=0
    g5: ArcOfCircle CenterX=-107.6 CenterY=4 CenterZ=0 NormalX=0 NormalY=0 NormalZ=1 AngleXU=0 Radius=16 StartAngle=0.137937 EndAngle=1.5708
    g6: LineSegment StartX=-82.8 StartY=6.2 StartZ=0 EndX=-91.752 EndY=6.2 EndZ=0
    g7: LineSegment [constr] StartX=-145.743 StartY=8.32624 StartZ=0 EndX=-147.645 EndY=8.94427 EndZ=0
    g8: ArcOfCircle CenterX=-132.428 CenterY=4 CenterZ=0 NormalX=0 NormalY=0 NormalZ=1 AngleXU=0 Radius=16 StartAngle=1.5708 EndAngle=2.82743
    g9: LineSegment StartX=-215.932 StartY=-80.4316 StartZ=0 EndX=-176.685 EndY=-80.4316 EndZ=0
    g10: LineSegment StartX=-147.645 StartY=8.94427 StartZ=0 EndX=-176.685 EndY=-80.4316 EndZ=0
    g11: LineSegment [constr] StartX=-193.988 StartY=-2.33927 StartZ=0 EndX=-192.176 EndY=-3.18451 EndZ=0
    g12: LineSegment [constr] StartX=-217.232 StartY=-52.1862 StartZ=0 EndX=-215.42 EndY=-53.0314 EndZ=0
    g13: LineSegment StartX=-192.176 StartY=-3.18451 StartZ=0 EndX=-215.42 EndY=-53.0314 EndZ=0
    g14: ArcOfCircle CenterX=-184.801 CenterY=-67.3089 CenterZ=0 NormalX=0 NormalY=0 NormalZ=1 AngleXU=0 Radius=33.7833 StartAngle=2.70526 EndAngle=3.54053
    g15: ArcOfCircle CenterX=-207.583 CenterY=4 CenterZ=0 NormalX=0 NormalY=0 NormalZ=1 AngleXU=0 Radius=17 StartAngle=5.84685 EndAngle=7.56663
    g16: LineSegment StartX=-202.765 StartY=20.303 StartZ=0 EndX=-195.887 EndY=39.2 EndZ=0
    g17: LineSegment [constr] StartX=-193.885 StartY=33.0037 StartZ=0 EndX=-197.644 EndY=34.3718 EndZ=0
    g18: LineSegment StartX=-195.887 StartY=39.2 StartZ=0 EndX=0 EndY=39.2 EndZ=0
    g19: LineSegment StartX=0 StartY=3.2 StartZ=0 EndX=0 EndY=39.2 EndZ=0
    g20: LineSegment StartX=-189.939 StartY=31.5672 StartZ=0 EndX=-192.333 EndY=24.9893 EndZ=0
    g21: LineSegment StartX=-196.467 StartY=26.4942 StartZ=0 EndX=-194.073 EndY=33.0721 EndZ=0
    g22: Circle CenterX=-213.443 CenterY=-76.8316 CenterZ=0 NormalX=0 NormalY=0 NormalZ=1 AngleXU=0 Radius=1.8
    g23: Circle CenterX=-179.305 CenterY=-76.8316 CenterZ=0 NormalX=0 NormalY=0 NormalZ=1 AngleXU=0 Radius=1.8
    g24: Circle CenterX=-184.08 CenterY=34.8 CenterZ=0 NormalX=0 NormalY=0 NormalZ=1 AngleXU=0 Radius=1.8
    g25: Circle CenterX=-78.51 CenterY=34.8 CenterZ=0 NormalX=0 NormalY=0 NormalZ=1 AngleXU=0 Radius=1.8
    g26: Circle CenterX=-78.51 CenterY=7.6 CenterZ=0 NormalX=0 NormalY=0 NormalZ=1 AngleXU=0 Radius=1.8
    g27: Circle CenterX=-5.6 CenterY=34.8 CenterZ=0 NormalX=0 NormalY=0 NormalZ=1 AngleXU=0 Radius=1.8
    g28: Circle CenterX=-5.6 CenterY=7.6 CenterZ=0 NormalX=0 NormalY=0 NormalZ=1 AngleXU=0 Radius=1.8
    g29: LineSegment StartX=-190.127 StartY=31.6356 StartZ=0 EndX=-189.939 EndY=31.5672 EndZ=0
    g30: LineSegment StartX=-194.073 StartY=33.0721 StartZ=0 EndX=-193.885 EndY=33.0037 EndZ=0
    g31: LineSegment StartX=-193.885 StartY=33.0037 StartZ=0 EndX=-190.127 EndY=31.6356 EndZ=0
    g32: LineSegment StartX=-196.467 StartY=26.4942 StartZ=0 EndX=-192.333 EndY=24.9893 EndZ=0
    g33: LineSegment [constr] StartX=-4 StartY=21.2 StartZ=0 EndX=-87.91 EndY=21.2 EndZ=0
    g34: GeomPoint [constr] X=-4 Y=21.2 Z=0
    g35: LineSegment [constr] StartX=-15.2 StartY=33.7 StartZ=0 EndX=-15.2 EndY=8.7 EndZ=0
    g36: LineSegment [constr] StartX=-15.2 StartY=33.7 StartZ=0 EndX=-56.2 EndY=33.7 EndZ=0
    g37: LineSegment [constr] StartX=-15.2 StartY=8.7 StartZ=0 EndX=-56.2 EndY=8.7 EndZ=0
    g38: LineSegment [constr] StartX=-56.2 StartY=33.7 StartZ=0 EndX=-56.2 EndY=8.7 EndZ=0
    g39: Circle CenterX=-18.6 CenterY=30.3 CenterZ=0 NormalX=0 NormalY=0 NormalZ=1 AngleXU=0 Radius=3.4
    g40: Circle CenterX=-18.6 CenterY=12.1 CenterZ=0 NormalX=0 NormalY=0 NormalZ=1 AngleXU=0 Radius=3.4
    g41: Circle CenterX=-43.2 CenterY=30.3 CenterZ=0 NormalX=0 NormalY=0 NormalZ=1 AngleXU=0 Radius=3.4
    g42: Circle CenterX=-43.2 CenterY=12.1 CenterZ=0 NormalX=0 NormalY=0 NormalZ=1 AngleXU=0 Radius=3.4
    g43: LineSegment [constr] StartX=-4 StartY=21.2 StartZ=0 EndX=-15.2 EndY=21.2 EndZ=0
    g44: LineSegment [constr] StartX=-15.2 StartY=21.2 StartZ=0 EndX=-36.2 EndY=21.2 EndZ=0
    g45: LineSegment [constr] StartX=-41.5 StartY=16.2 StartZ=0 EndX=-30.9 EndY=16.2 EndZ=0
    g46: LineSegment [constr] StartX=-30.9 StartY=16.2 StartZ=0 EndX=-30.9 EndY=26.2 EndZ=0
    g47: LineSegment [constr] StartX=-30.9 StartY=26.2 StartZ=0 EndX=-41.5 EndY=26.2 EndZ=0
    g48: LineSegment [constr] StartX=-41.5 StartY=26.2 StartZ=0 EndX=-41.5 EndY=16.2 EndZ=0
    g49: GeomPoint [constr] X=-36.2 Y=21.2 Z=0
    g50: Circle CenterX=-36.2 CenterY=21.2 CenterZ=0 NormalX=0 NormalY=0 NormalZ=1 AngleXU=0 Radius=2.8
    g51: LineSegment [constr] StartX=-24.2 StartY=26.7 StartZ=0 EndX=-24.2 EndY=15.7 EndZ=0
    g52: Circle CenterX=-24.2 CenterY=26.7 CenterZ=0 NormalX=0 NormalY=0 NormalZ=1 AngleXU=0 Radius=3
    g53: Circle CenterX=-24.2 CenterY=15.7 CenterZ=0 NormalX=0 NormalY=0 NormalZ=1 AngleXU=0 Radius=3
    g54: GeomPoint X=-18.6 Y=30.3 Z=0
    g55: GeomPoint X=-18.6 Y=12.1 Z=0
    g56: GeomPoint X=-43.2 Y=12.1 Z=0
    g57: GeomPoint X=-43.2 Y=30.3 Z=0
    g58: Circle CenterX=-65 CenterY=21.2 CenterZ=0 NormalX=0 NormalY=0 NormalZ=1 AngleXU=0 Radius=1.5
    g59: Circle CenterX=-42 CenterY=21.2 CenterZ=0 NormalX=0 NormalY=0 NormalZ=1 AngleXU=0 Radius=1.5
    g60: Circle CenterX=-19 CenterY=21.2 CenterZ=0 NormalX=0 NormalY=0 NormalZ=1 AngleXU=0 Radius=1.5
  constraints (149):
    c: Coincident(g0,g-41)
    c: Horizontal(g0)
    c: PointOnObject(g0,g-39)
    c: Coincident(g1,g0)
    c: Vertical(g1)
    c: DistanceY(g1,g1) = 3
    c: Coincident(g2,g-17)
    c: Vertical(g2)
    c: Coincident(g3,g-16)
    c: Vertical(g3)
    c: DistanceY(g2,g2) = 2
    c: DistanceY(g3,g3) = 2
    c: Coincident(g4,g3)
    c: Coincident(g4,g2)
    c: Coincident(g5,g-17)
    c: Coincident(g5,g2)
    c: Coincident(g6,g1)
    c: Horizontal(g6)
    c: Coincident(g6,g5)
    c: Coincident(g7,g-15)
    c: Coincident(g8,g7)
    c: Coincident(g8,g3)
    c: Coincident(g8,g-15)
    c: Horizontal(g9)
    c: DistanceY(g-13,g9) = 2
    c: Coincident(g10,g7)
    c: Parallel(g10,g-14)
    c: Coincident(g9,g10)
    c: Distance(g11) = 2
    c: Coincident(g11,g-11)
    c: Perpendicular(g-11,g11)
    c: Distance(g12) = 2
    c: Coincident(g12,g-12)
    c: Perpendicular(g-11,g12)
    c: Coincident(g13,g11)
    c: Coincident(g13,g12)
    c: Coincident(g14,g-32)
    c: Coincident(g14,g12)
    c: Coincident(g14,g9)
    c: Coincident(g15,g-10)
    c: Coincident(g15,g11)
    c: Parallel(g16,g-22)
    c: Distance(g17) = 4
    c: PointOnObject(g17,g16)
    c: Coincident(g15,g16)
    c: Horizontal(g18)
    c: Coincident(g18,g16)
    c: Coincident(g19,g0)
    c: PointOnObject(g19,g-39)
    c: DistanceY(g19,g-36) = 2
    c: Coincident(g18,g19)
    c: Diameter(g22) = 3.6
    c: Coincident(g22,g-9)
    c: Diameter(g23) = 3.6
    c: Coincident(g23,g-8)
    c: Diameter(g24) = 3.6
    c: Diameter(g25) = 3.6
    c: Diameter(g26) = 3.6
    c: Diameter(g27) = 3.6
    c: Diameter(g28) = 3.6
    c: Coincident(g27,g-4)
    c: Coincident(g28,g-3)
    c: Coincident(g25,g-6)
    c: Coincident(g26,g-5)
    c: Coincident(g24,g-7)
    c: Parallel(g20,g-21)
    c: Equal(g20,g-21)
    c: Parallel(g21,g-19)
    c: Equal(g21,g-19)
    c: Distance(g29) = 0.2
    c: Distance(g30) = 0.2
    c: Parallel(g29,g-20)
    c: Parallel(g31,g-20)
    c: Equal(g31,g-20)
    c: Coincident(g30,g31)
    c: Coincident(g31,g29)
    c: Coincident(g29,g-21)
    c: Parallel(g30,g31)
    c: Coincident(g17,g30)
    c: Coincident(g20,g29)
    c: Coincident(g21,g30)
    c: Perpendicular(g16,g17)
    c: Coincident(g32,g21)
    c: Coincident(g32,g20)
    c: Perpendicular(g10,g7)
    c: Horizontal(g33)
    c: Symmetric(g-24,g-24,g33)
    c: PointOnObject(g33,g-28)
    c: Symmetric(g-24,g-24,g34)
    c: DistanceY(g35,g35) = 25
    c: Symmetric(g35,g35,g33)
    c: Distance(g36) = 41
    c: Coincident(g36,g35)
    c: Horizontal(g36)
    c: Coincident(g37,g35)
    c: Horizontal(g37)
    c: Coincident(g38,g36)
    c: Vertical(g38)
    c: Coincident(g37,g38)
    c: Diameter(g39) = 6.8
    c: Diameter(g40) = 6.8
    c: Tangent(g39,g36)
    c: Tangent(g40,g37)
    c: Tangent(g39,g35)
    c: Tangent(g40,g35)
    c: Diameter(g41) = 6.8
    c: Diameter(g42) = 6.8
    c: Tangent(g41,g36)
    c: Tangent(g42,g37)
    c: DistanceX(g41,g39) = 24.6
    c: DistanceX(g42,g40) = 24.6
    c: Distance(g43) = 11.2
    c: Coincident(g43,g33)
    c: PointOnObject(g43,g33)
    c: PointOnObject(g43,g35)
    c: Distance(g44) = 21
    c: Coincident(g44,g43)
    c: PointOnObject(g44,g33)
    c: Coincident(g45,g46)
    c: Coincident(g46,g47)
    c: Coincident(g47,g48)
    c: Coincident(g48,g45)
    c: Horizontal(g45)
    c: Horizontal(g47)
    c: Vertical(g46)
    c: Vertical(g48)
    c: Symmetric(g47,g45,g49)
    c: Distance(g46,g48) = 10.6
    c: Distance(g45,g47) = 10
    c: Coincident(g49,g44)
    c: Diameter(g50) = 5.6
    c: Coincident(g50,g44)
    c: Distance(g51) = 11
    c: Symmetric(g51,g51,g33)
    c: DistanceX(g51,g43) = 9
    c: Diameter(g52) = 6
    c: Coincident(g52,g51)
    c: Diameter(g53) = 6
    c: Coincident(g53,g51)
    c: Coincident(g40,g55)
    c: Coincident(g39,g54)
    c: Coincident(g41,g57)
    c: Coincident(g42,g56)
    c: Diameter(g58) = 3
    c: Diameter(g59) = 3
    c: Diameter(g60) = 3
    c: Coincident(g58,g-44)
    c: Coincident(g59,g-46)
    c: Coincident(g60,g-45)
FEATURE [Sketcher::SketchObject] Sketch076  label="lato sx pistola - scavi pulsanti"
  ArcFitTolerance = 1e-06
  AttachmentSupport = -> [XZ_Plane]
  ExternalGeometry = -> [Sketch074]
  FullyConstrained = true
  MakeInternals = false
  MapMode = 5
  Placement = pos=(0,0,0) rot=(1,0,0;1.5708rad)
  sketch-geometry (3):
    g0: Circle CenterX=-65 CenterY=21.2 CenterZ=0 NormalX=0 NormalY=0 NormalZ=1 AngleXU=0 Radius=7.3
    g1: Circle CenterX=-42 CenterY=21.2 CenterZ=0 NormalX=0 NormalY=0 NormalZ=1 AngleXU=0 Radius=7.3
    g2: Circle CenterX=-19 CenterY=21.2 CenterZ=0 NormalX=0 NormalY=0 NormalZ=1 AngleXU=0 Radius=7.3
  constraints (6):
    c: Diameter(g0) = 14.6
    c: Diameter(g1) = 14.6
    c: Diameter(g2) = 14.6
    c: Coincident(g0,g-3)
    c: Coincident(g1,g-4)
    c: Coincident(g2,g-5)
FEATURE [Part::Extrusion] Extrude077  label="Extrude lato sx pistola - scavi pulsanti"
  Base = -> Sketch076
  Dir = (0,-1,2e-16)
  DirMode = 2
  FaceMakerClass = Part::FaceMakerBullseye
  FaceMakerMode = 3
  LengthFwd = -1.2
  LengthRev = 0
  Solid = true
  Symmetric = false
FEATURE [Part::Cut] Cut044
  Base = -> Extrude076
  Refine = true
  Tool = -> Extrude077
FEATURE [Part::Extrusion] Extrude078  label="Extrude lato dx pistola"
  Base = -> Sketch075
  Dir = (0,-1,2e-16)
  DirMode = 2
  FaceMakerClass = Part::FaceMakerBullseye
  FaceMakerMode = 3
  LengthFwd = 2
  LengthRev = 0
  Solid = true
  Symmetric = false
FEATURE [Sketcher::SketchObject] Sketch077  label="lato dx pistola - scavi pulsanti"
  ArcFitTolerance = 1e-06
  AttachmentSupport = -> [XZ_Plane]
  ExternalGeometry = -> [Sketch075]
  FullyConstrained = true
  MakeInternals = false
  MapMode = 5
  Placement = pos=(0,0,0) rot=(1,0,0;1.5708rad)
  sketch-geometry (4):
    g0: LineSegment StartX=-27.2 StartY=26.7 StartZ=0 EndX=-27.2 EndY=15.7 EndZ=0
    g1: LineSegment StartX=-21.2 StartY=26.7 StartZ=0 EndX=-21.2 EndY=15.7 EndZ=0
    g2: ArcOfCircle CenterX=-24.2 CenterY=26.7 CenterZ=0 NormalX=0 NormalY=0 NormalZ=1 AngleXU=0 Radius=3 StartAngle=5.96642e-06 EndAngle=3.14159
    g3: ArcOfCircle CenterX=-24.2 CenterY=15.7 CenterZ=0 NormalX=0 NormalY=0 NormalZ=1 AngleXU=0 Radius=3 StartAngle=3.14159 EndAngle=6.28319
  constraints (10):
    c: Vertical(g0)
    c: Coincident(g2,g-3)
    c: Vertical(g1)
    c: Coincident(g3,g-4)
    c: Tangent(g1,g-3)
    c: Tangent(g0,g-3)
    c: Tangent(g3,g0) = -1.5708
    c: Coincident(g3,g1)
    c: Tangent(g0,g2) = -1.5708
    c: Coincident(g1,g2)
FEATURE [Part::Extrusion] Extrude079  label="Extrude lato dx pistola - scavi pulsanti"
  Base = -> Sketch077
  Dir = (0,-1,2e-16)
  DirMode = 2
  FaceMakerClass = Part::FaceMakerBullseye
  FaceMakerMode = 3
  LengthFwd = 1.2
  LengthRev = 0
  Solid = true
  Symmetric = false
FEATURE [Part::Cut] Cut045
  Base = -> Extrude078
  Refine = true
  Tool = -> Extrude079
FEATURE [Sketcher::SketchObject] Sketch078
  ArcFitTolerance = 1e-06
  AttachmentSupport = -> [XZ_Plane005]
  FullyConstrained = true
  MakeInternals = false
  MapMode = 5
  Placement = pos=(0,0,0) rot=(1,0,0;1.5708rad)
  sketch-geometry (5):
    g0: LineSegment [constr] StartX=0 StartY=5.5 StartZ=0 EndX=0 EndY=-5.5 EndZ=0
    g1: ArcOfCircle CenterX=0 CenterY=5.5 CenterZ=0 NormalX=0 NormalY=0 NormalZ=1 AngleXU=0 Radius=2.7 StartAngle=0 EndAngle=3.14159
    g2: ArcOfCircle CenterX=0 CenterY=-5.5 CenterZ=0 NormalX=0 NormalY=0 NormalZ=1 AngleXU=0 Radius=2.7 StartAngle=3.1416 EndAngle=6.28318
    g3: LineSegment StartX=-2.7 StartY=5.5 StartZ=0 EndX=-2.7 EndY=-5.50001 EndZ=0
    g4: LineSegment StartX=2.7 StartY=5.5 StartZ=0 EndX=2.7 EndY=-5.50001 EndZ=0
  constraints (13):
    c: Distance(g0) = 11
    c: Vertical(g0)
    c: Symmetric(g0,g0,g-1)
    c: Radius(g1) = 2.7
    c: Coincident(g1,g0)
    c: Radius(g2) = 2.7
    c: Coincident(g2,g0)
    c: Vertical(g3)
    c: Vertical(g4)
    c: Coincident(g2,g4)
    c: Coincident(g2,g3)
    c: Tangent(g3,g1) = -1.5708
    c: Tangent(g4,g1) = 1.5708
FEATURE [PartDesign::Pad] Pad002
  Direction = (0,-1,2e-16)
  Length = 0.8
  Length2 = 10
  Placement = pos=(0,0,0) rot=(1,0,0;1.5708rad)
  Profile = -> Sketch078
  ReferenceAxis = -> Sketch078 [N_Axis]
  Refine = true
  Suppressed = false
  Type = 0
FEATURE [Sketcher::SketchObject] Sketch079
  ArcFitTolerance = 1e-06
  AttachmentSupport = -> [XZ_Plane005]
  ExternalGeometry = -> [Sketch078]
  FullyConstrained = true
  MakeInternals = false
  MapMode = 5
  Placement = pos=(0,0,0) rot=(1,0,0;1.5708rad)
  sketch-geometry (2):
    g0: Circle CenterX=-1e-16 CenterY=5.5 CenterZ=0 NormalX=0 NormalY=0 NormalZ=1 AngleXU=0 Radius=2.7
    g1: Circle CenterX=0 CenterY=-5.5 CenterZ=0 NormalX=0 NormalY=0 NormalZ=1 AngleXU=0 Radius=2.7
  constraints (4):
    c: Coincident(g0,g-3)
    c: PointOnObject(g-3,g0)
    c: Coincident(g1,g-4)
    c: Equal(g1,g-4)
FEATURE [PartDesign::Pad] Pad003
  BaseFeature = -> Pad002
  Direction = (0,-1,2e-16)
  Length = 5
  Length2 = 10
  Placement = pos=(0,0,0) rot=(1,0,0;1.5708rad)
  Profile = -> Sketch079
  ReferenceAxis = -> Sketch079 [N_Axis]
  Refine = true
  Suppressed = false
  Type = 0
FEATURE [PartDesign::Fillet] Fillet001
  Base = -> Pad003 [Edge16,Edge14]
  BaseFeature = -> Pad003
  Placement = pos=(0,0,0) rot=(1,0,0;1.5708rad)
  Radius = 0.4
  Refine = true
  SupportTransform = false
  Suppressed = false
  UseAllEdges = false
FEATURE [PartDesign::Body] Body005  label="pulsanti lato destro"
  AllowCompound = false
  Group = -> [Sketch078,Pad002,Sketch079,Pad003,Fillet001]
  Origin = -> Origin005
  Tip = -> Fillet001
FEATURE [Sketcher::SketchObject] Sketch080  label="lato dx pistola - fori per inserto M3 x 3 x 4.5"
  ArcFitTolerance = 1e-06
  AttachmentSupport = -> [XZ_Plane]
  ExternalGeometry = -> [Sketch075]
  FullyConstrained = true
  MakeInternals = false
  MapMode = 5
  Placement = pos=(0,0,0) rot=(1,0,0;1.5708rad)
  sketch-geometry (4):
    g0: Circle CenterX=-18.6 CenterY=12.1 CenterZ=0 NormalX=0 NormalY=0 NormalZ=1 AngleXU=0 Radius=2.25
    g1: Circle CenterX=-18.6 CenterY=30.3 CenterZ=0 NormalX=0 NormalY=0 NormalZ=1 AngleXU=0 Radius=2.25
    g2: Circle CenterX=-43.2 CenterY=30.3 CenterZ=0 NormalX=0 NormalY=0 NormalZ=1 AngleXU=0 Radius=2.25
    g3: Circle CenterX=-43.2 CenterY=12.1 CenterZ=0 NormalX=0 NormalY=0 NormalZ=1 AngleXU=0 Radius=2.25
  constraints (8):
    c: Diameter(g0) = 4.5
    c: Coincident(g0,g-5)
    c: Diameter(g1) = 4.5
    c: Coincident(g1,g-4)
    c: Diameter(g2) = 4.5
    c: Coincident(g2,g-3)
    c: Diameter(g3) = 4.5
    c: Coincident(g3,g-6)
FEATURE [Sketcher::SketchObject] Sketch081  label="lato dx pistola - pieno per inserto M3 x 3 x 4,5"
  ArcFitTolerance = 1e-06
  AttachmentSupport = -> [XZ_Plane]
  ExternalGeometry = -> [Sketch075]
  FullyConstrained = true
  MakeInternals = false
  MapMode = 5
  Placement = pos=(0,0,0) rot=(1,0,0;1.5708rad)
  sketch-geometry (4):
    g0: Circle CenterX=-43.2 CenterY=30.3 CenterZ=0 NormalX=0 NormalY=0 NormalZ=1 AngleXU=0 Radius=3.4
    g1: Circle CenterX=-18.6 CenterY=30.3 CenterZ=0 NormalX=0 NormalY=0 NormalZ=1 AngleXU=0 Radius=3.4
    g2: Circle CenterX=-43.2 CenterY=12.1 CenterZ=0 NormalX=0 NormalY=0 NormalZ=1 AngleXU=0 Radius=3.4
    g3: Circle CenterX=-18.6 CenterY=12.1 CenterZ=0 NormalX=0 NormalY=0 NormalZ=1 AngleXU=0 Radius=3.4
  constraints (8):
    c: Diameter(g0) = 6.8
    c: Coincident(g0,g-6)
    c: Diameter(g1) = 6.8
    c: Coincident(g1,g-3)
    c: Diameter(g2) = 6.8
    c: Coincident(g2,g-5)
    c: Diameter(g3) = 6.8
    c: Coincident(g3,g-4)
FEATURE [Part::Extrusion] Extrude080  label="Extrude lato dx pistola - pieno per inserto M3 x 3 x 4,5"
  Base = -> Sketch081
  Dir = (0,-1,2e-16)
  DirMode = 2
  FaceMakerClass = Part::FaceMakerBullseye
  FaceMakerMode = 3
  LengthFwd = -2.4
  LengthRev = 0
  Solid = true
  Symmetric = false
FEATURE [Part::MultiFuse] Fusion004
  Refine = true
  Shapes = -> [Cut045,Extrude080]
FEATURE [Part::Extrusion] Extrude081  label="Extrude lato dx pistola - fori per inserto M3 x 3 x 4.5"
  Base = -> Sketch080
  Dir = (0,-1,2e-16)
  DirMode = 2
  FaceMakerClass = Part::FaceMakerBullseye
  FaceMakerMode = 3
  LengthFwd = 0.6
  LengthRev = 2.4
  Solid = true
  Symmetric = false
FEATURE [Part::Cut] Cut046
  Base = -> Fusion004
  Refine = true
  Tool = -> Extrude081
FEATURE [Sketcher::SketchObject] Sketch082  label="lato sx pistola - disegno anteriore"
  ArcFitTolerance = 1e-06
  AttachmentSupport = -> [XZ_Plane]
  ExternalGeometry = -> [Sketch074]
  FullyConstrained = true
  MakeInternals = false
  MapMode = 5
  Placement = pos=(0,0,0) rot=(1,0,0;1.5708rad)
  sketch-geometry (12):
    g0: ArcOfCircle CenterX=-65 CenterY=21.2 CenterZ=0 NormalX=0 NormalY=0 NormalZ=1 AngleXU=0 Radius=10 StartAngle=1.5708 EndAngle=4.71239
    g1: ArcOfCircle CenterX=-19 CenterY=21.2 CenterZ=0 NormalX=0 NormalY=0 NormalZ=1 AngleXU=0 Radius=10 StartAngle=4.71239 EndAngle=7.85398
    g2: LineSegment StartX=-65 StartY=31.2 StartZ=0 EndX=-19 EndY=31.2 EndZ=0
    g3: LineSegment StartX=-65 StartY=11.2 StartZ=0 EndX=-19 EndY=11.2 EndZ=0
    g4: LineSegment StartX=-82.8 StartY=3.2 StartZ=0 EndX=0 EndY=3.2 EndZ=0
    g5: LineSegment StartX=0 StartY=3.2 StartZ=0 EndX=0 EndY=39.2 EndZ=0
    g6: LineSegment StartX=0 StartY=39.2 StartZ=0 EndX=-82.8 EndY=39.2 EndZ=0
    g7: LineSegment StartX=-82.8 StartY=39.2 StartZ=0 EndX=-82.8 EndY=3.2 EndZ=0
    g8: Circle CenterX=-78.51 CenterY=34.8 CenterZ=0 NormalX=0 NormalY=0 NormalZ=1 AngleXU=0 Radius=1.8
    g9: Circle CenterX=-5.6 CenterY=34.8 CenterZ=0 NormalX=0 NormalY=0 NormalZ=1 AngleXU=0 Radius=1.8
    g10: Circle CenterX=-5.6 CenterY=7.6 CenterZ=0 NormalX=0 NormalY=0 NormalZ=1 AngleXU=0 Radius=1.8
    g11: Circle CenterX=-78.51 CenterY=7.6 CenterZ=0 NormalX=0 NormalY=0 NormalZ=1 AngleXU=0 Radius=1.8
  constraints (26):
    c: Tangent(g0,g2) = 1.5708
    c: Tangent(g0,g3) = -1.5708
    c: Tangent(g1,g2) = 1.5708
    c: Tangent(g1,g3) = -1.5708
    c: Equal(g0,g1)
    c: Coincident(g4,g5)
    c: Coincident(g5,g6)
    c: Coincident(g6,g7)
    c: Coincident(g7,g4)
    c: Horizontal(g4)
    c: Horizontal(g6)
    c: Vertical(g5)
    c: Vertical(g7)
    c: Coincident(g4,g-7)
    c: Coincident(g5,g-9)
    c: Diameter(g1) = 20
    c: Coincident(g1,g-5)
    c: Coincident(g0,g-4)
    c: Equal(g9,g-11)
    c: Equal(g10,g-12)
    c: Equal(g11,g-13)
    c: Equal(g8,g-10)
    c: Coincident(g8,g-10)
    c: Coincident(g11,g-13)
    c: Coincident(g10,g-12)
    c: Coincident(g9,g-11)
FEATURE [Sketcher::SketchObject] Sketch083  label="lato dx pistola - disegno anteriore"
  ArcFitTolerance = 1e-06
  AttachmentSupport = -> [XZ_Plane]
  ExternalGeometry = -> [Sketch082]
  FullyConstrained = true
  MakeInternals = false
  MapMode = 5
  Placement = pos=(0,0,0) rot=(1,0,0;1.5708rad)
  sketch-geometry (12):
    g0: LineSegment StartX=-82.8 StartY=3.2 StartZ=0 EndX=0 EndY=3.2 EndZ=0
    g1: LineSegment StartX=0 StartY=3.2 StartZ=0 EndX=0 EndY=39.2 EndZ=0
    g2: LineSegment StartX=0 StartY=39.2 StartZ=0 EndX=-82.8 EndY=39.2 EndZ=0
    g3: LineSegment StartX=-82.8 StartY=39.2 StartZ=0 EndX=-82.8 EndY=3.2 EndZ=0
    g4: ArcOfCircle CenterX=-65 CenterY=21.2 CenterZ=0 NormalX=0 NormalY=0 NormalZ=1 AngleXU=0 Radius=10 StartAngle=1.5708 EndAngle=4.71239
    g5: ArcOfCircle CenterX=-19 CenterY=21.2 CenterZ=0 NormalX=0 NormalY=0 NormalZ=1 AngleXU=0 Radius=10 StartAngle=4.71239 EndAngle=7.85398
    g6: LineSegment StartX=-65 StartY=31.2 StartZ=0 EndX=-19 EndY=31.2 EndZ=0
    g7: LineSegment StartX=-65 StartY=11.2 StartZ=0 EndX=-19 EndY=11.2 EndZ=0
    g8: Circle CenterX=-78.51 CenterY=34.8 CenterZ=0 NormalX=0 NormalY=0 NormalZ=1 AngleXU=0 Radius=1.8
    g9: Circle CenterX=-5.6 CenterY=34.8 CenterZ=0 NormalX=0 NormalY=0 NormalZ=1 AngleXU=0 Radius=1.8
    g10: Circle CenterX=-5.6 CenterY=7.6 CenterZ=0 NormalX=0 NormalY=0 NormalZ=1 AngleXU=0 Radius=1.8
    g11: Circle CenterX=-78.51 CenterY=7.6 CenterZ=0 NormalX=0 NormalY=0 NormalZ=1 AngleXU=0 Radius=1.8
  constraints (26):
    c: Coincident(g0,g1)
    c: Coincident(g1,g2)
    c: Coincident(g2,g3)
    c: Coincident(g3,g0)
    c: Horizontal(g0)
    c: Horizontal(g2)
    c: Vertical(g1)
    c: Vertical(g3)
    c: Coincident(g0,g-5)
    c: Coincident(g1,g-6)
    c: Tangent(g4,g6) = 1.5708
    c: Tangent(g4,g7) = -1.5708
    c: Tangent(g5,g6) = 1.5708
    c: Tangent(g5,g7) = -1.5708
    c: Equal(g4,g5)
    c: Equal(g5,g-9)
    c: Coincident(g5,g-9)
    c: Coincident(g4,g-8)
    c: Equal(g8,g-11)
    c: Equal(g11,g-12)
    c: Equal(g10,g-13)
    c: Equal(g9,g-14)
    c: Coincident(g9,g-14)
    c: Coincident(g10,g-13)
    c: Coincident(g11,g-12)
    c: Coincident(g8,g-11)
FEATURE [Sketcher::SketchObject] Sketch084  label="lato sx pistola - spazi anteriori per viti"
  ArcFitTolerance = 1e-06
  AttachmentSupport = -> [XZ_Plane]
  ExternalGeometry = -> [Sketch082]
  FullyConstrained = true
  MakeInternals = false
  MapMode = 5
  Placement = pos=(0,0,0) rot=(1,0,0;1.5708rad)
  sketch-geometry (24):
    g0: ArcOfCircle CenterX=-78.51 CenterY=34.8 CenterZ=0 NormalX=0 NormalY=0 NormalZ=1 AngleXU=0 Radius=3.5 StartAngle=4.71239 EndAngle=6.28319
    g1: ArcOfCircle CenterX=-5.6 CenterY=34.8 CenterZ=0 NormalX=0 NormalY=0 NormalZ=1 AngleXU=0 Radius=3.5 StartAngle=3.14159 EndAngle=4.71239
    g2: ArcOfCircle CenterX=-78.51 CenterY=7.6 CenterZ=0 NormalX=0 NormalY=0 NormalZ=1 AngleXU=0 Radius=3.5 StartAngle=3.99598e-11 EndAngle=1.5708
    g3: ArcOfCircle CenterX=-5.6 CenterY=7.6 CenterZ=0 NormalX=0 NormalY=0 NormalZ=1 AngleXU=0 Radius=3.5 StartAngle=1.5708 EndAngle=3.14159
    g4: LineSegment StartX=0 StartY=11.1 StartZ=0 EndX=-5.6 EndY=11.1 EndZ=0
    g5: LineSegment StartX=-9.1 StartY=7.6 StartZ=0 EndX=-9.1 EndY=3.2 EndZ=0
    g6: LineSegment StartX=-75.01 StartY=39.2 StartZ=0 EndX=-75.01 EndY=34.8 EndZ=0
    g7: LineSegment StartX=-82.8 StartY=31.3 StartZ=0 EndX=-78.51 EndY=31.3 EndZ=0
    g8: LineSegment StartX=-82.8 StartY=11.1 StartZ=0 EndX=-78.51 EndY=11.1 EndZ=0
    g9: LineSegment StartX=-75.01 StartY=7.6 StartZ=0 EndX=-75.01 EndY=3.2 EndZ=0
    g10: LineSegment StartX=-9.1 StartY=39.2 StartZ=0 EndX=-9.1 EndY=34.8 EndZ=0
    g11: LineSegment StartX=-5.6 StartY=31.3 StartZ=0 EndX=0 EndY=31.3 EndZ=0
    g12: LineSegment StartX=-9.1 StartY=39.2 StartZ=0 EndX=0 EndY=39.2 EndZ=0
    g13: LineSegment StartX=0 StartY=39.2 StartZ=0 EndX=0 EndY=31.3 EndZ=0
    g14: LineSegment StartX=0 StartY=11.1 StartZ=0 EndX=0 EndY=3.2 EndZ=0
    g15: LineSegment StartX=0 StartY=3.2 StartZ=0 EndX=-9.1 EndY=3.2 EndZ=0
    g16: LineSegment StartX=-75.01 StartY=3.2 StartZ=0 EndX=-82.8 EndY=3.2 EndZ=0
    g17: LineSegment StartX=-82.8 StartY=3.2 StartZ=0 EndX=-82.8 EndY=11.1 EndZ=0
    g18: LineSegment StartX=-82.8 StartY=31.3 StartZ=0 EndX=-82.8 EndY=39.2 EndZ=0
    g19: LineSegment StartX=-82.8 StartY=39.2 StartZ=0 EndX=-75.01 EndY=39.2 EndZ=0
    g20: Circle CenterX=-78.51 CenterY=34.8 CenterZ=0 NormalX=0 NormalY=0 NormalZ=1 AngleXU=0 Radius=1.8
    g21: Circle CenterX=-5.6 CenterY=34.8 CenterZ=0 NormalX=0 NormalY=0 NormalZ=1 AngleXU=0 Radius=1.8
    g22: Circle CenterX=-5.6 CenterY=7.6 CenterZ=0 NormalX=0 NormalY=0 NormalZ=1 AngleXU=0 Radius=1.8
    g23: Circle CenterX=-78.51 CenterY=7.6 CenterZ=0 NormalX=0 NormalY=0 NormalZ=1 AngleXU=0 Radius=1.8
  constraints (56):
    c: Radius(g0) = 3.5
    c: Coincident(g0,g-5)
    c: Radius(g1) = 3.5
    c: Coincident(g1,g-10)
    c: Radius(g2) = 3.5
    c: Coincident(g2,g-4)
    c: Radius(g3) = 3.5
    c: Coincident(g3,g-9)
    c: Horizontal(g4)
    c: Vertical(g5)
    c: Vertical(g6)
    c: Horizontal(g7)
    c: Horizontal(g8)
    c: Vertical(g9)
    c: Vertical(g10)
    c: Horizontal(g11)
    c: Tangent(g11,g1) = -1.5708
    c: Tangent(g1,g10) = -1.5708
    c: Tangent(g3,g5) = -1.5708
    c: Tangent(g3,g4) = -1.5708
    c: Tangent(g9,g2) = 1.5708
    c: Tangent(g8,g2) = 1.5708
    c: Tangent(g7,g0) = -1.5708
    c: Tangent(g0,g6) = 1.5708
    c: PointOnObject(g10,g-7)
    c: PointOnObject(g11,g-11)
    c: PointOnObject(g4,g-11)
    c: PointOnObject(g5,g-8)
    c: PointOnObject(g9,g-8)
    c: PointOnObject(g8,g-6)
    c: PointOnObject(g7,g-6)
    c: PointOnObject(g6,g-7)
    c: Coincident(g12,g10)
    c: Coincident(g12,g-11)
    c: Coincident(g13,g12)
    c: Coincident(g13,g11)
    c: Coincident(g14,g4)
    c: Coincident(g14,g-11)
    c: Coincident(g15,g14)
    c: Coincident(g15,g5)
    c: Coincident(g16,g9)
    c: Coincident(g16,g-8)
    c: Coincident(g17,g16)
    c: Coincident(g17,g8)
    c: Coincident(g18,g7)
    c: Coincident(g18,g-7)
    c: Coincident(g19,g18)
    c: Coincident(g19,g6)
    c: Equal(g21,g-10)
    c: Equal(g-9,g22)
    c: Equal(g23,g-4)
    c: Equal(g20,g-5)
    c: Coincident(g20,g0)
    c: Coincident(g21,g1)
    c: Coincident(g22,g3)
    c: Coincident(g23,g2)
FEATURE [Sketcher::SketchObject] Sketch085  label="lato dx pistola - spazi anteriori per viti"
  ArcFitTolerance = 1e-06
  AttachmentSupport = -> [XZ_Plane]
  ExternalGeometry = -> [Sketch083]
  FullyConstrained = true
  MakeInternals = false
  MapMode = 5
  Placement = pos=(0,0,0) rot=(1,0,0;1.5708rad)
  sketch-geometry (24):
    g0: ArcOfCircle CenterX=-78.51 CenterY=34.8 CenterZ=0 NormalX=0 NormalY=0 NormalZ=1 AngleXU=0 Radius=3.5 StartAngle=4.71239 EndAngle=6.28319
    g1: ArcOfCircle CenterX=-5.6 CenterY=34.8 CenterZ=0 NormalX=0 NormalY=0 NormalZ=1 AngleXU=0 Radius=3.5 StartAngle=3.14159 EndAngle=4.71239
    g2: ArcOfCircle CenterX=-78.51 CenterY=7.6 CenterZ=0 NormalX=0 NormalY=0 NormalZ=1 AngleXU=0 Radius=3.5 StartAngle=3.99599e-11 EndAngle=1.5708
    g3: ArcOfCircle CenterX=-5.6 CenterY=7.6 CenterZ=0 NormalX=0 NormalY=0 NormalZ=1 AngleXU=0 Radius=3.5 StartAngle=1.5708 EndAngle=3.14159
    g4: LineSegment StartX=-9.1 StartY=39.2 StartZ=0 EndX=-9.1 EndY=34.8 EndZ=0
    g5: LineSegment StartX=-5.6 StartY=31.3 StartZ=0 EndX=0 EndY=31.3 EndZ=0
    g6: LineSegment StartX=-5.6 StartY=11.1 StartZ=0 EndX=0 EndY=11.1 EndZ=0
    g7: LineSegment StartX=-9.1 StartY=7.6 StartZ=0 EndX=-9.1 EndY=3.2 EndZ=0
    g8: LineSegment StartX=-82.8 StartY=11.1 StartZ=0 EndX=-78.51 EndY=11.1 EndZ=0
    g9: LineSegment StartX=-75.01 StartY=7.6 StartZ=0 EndX=-75.01 EndY=3.2 EndZ=0
    g10: LineSegment StartX=-82.8 StartY=31.3 StartZ=0 EndX=-78.51 EndY=31.3 EndZ=0
    g11: LineSegment StartX=-75.01 StartY=34.8 StartZ=0 EndX=-75.01 EndY=39.2 EndZ=0
    g12: LineSegment StartX=-75.01 StartY=3.2 StartZ=0 EndX=-82.8 EndY=3.2 EndZ=0
    g13: LineSegment StartX=-82.8 StartY=3.2 StartZ=0 EndX=-82.8 EndY=11.1 EndZ=0
    g14: LineSegment StartX=-82.8 StartY=31.3 StartZ=0 EndX=-82.8 EndY=39.2 EndZ=0
    g15: LineSegment StartX=-82.8 StartY=39.2 StartZ=0 EndX=-75.01 EndY=39.2 EndZ=0
    g16: LineSegment StartX=-9.1 StartY=39.2 StartZ=0 EndX=0 EndY=39.2 EndZ=0
    g17: LineSegment StartX=0 StartY=39.2 StartZ=0 EndX=0 EndY=31.3 EndZ=0
    g18: LineSegment StartX=-9.1 StartY=3.2 StartZ=0 EndX=0 EndY=3.2 EndZ=0
    g19: LineSegment StartX=0 StartY=3.2 StartZ=0 EndX=0 EndY=11.1 EndZ=0
    g20: Circle CenterX=-78.51 CenterY=34.8 CenterZ=0 NormalX=0 NormalY=0 NormalZ=1 AngleXU=0 Radius=1.8
    g21: Circle CenterX=-5.6 CenterY=34.8 CenterZ=0 NormalX=0 NormalY=0 NormalZ=1 AngleXU=0 Radius=1.8
    g22: Circle CenterX=-5.6 CenterY=7.6 CenterZ=0 NormalX=0 NormalY=0 NormalZ=1 AngleXU=0 Radius=1.8
    g23: Circle CenterX=-78.51 CenterY=7.6 CenterZ=0 NormalX=0 NormalY=0 NormalZ=1 AngleXU=0 Radius=1.8
  constraints (56):
    c: Radius(g0) = 3.5
    c: Coincident(g0,g-3)
    c: Radius(g1) = 3.5
    c: Coincident(g1,g-5)
    c: Radius(g2) = 3.5
    c: Coincident(g2,g-4)
    c: Radius(g3) = 3.5
    c: Coincident(g3,g-6)
    c: Vertical(g4)
    c: Horizontal(g5)
    c: Horizontal(g6)
    c: Vertical(g7)
    c: Horizontal(g8)
    c: Vertical(g9)
    c: Horizontal(g10)
    c: Vertical(g11)
    c: Tangent(g4,g1) = -1.5708
    c: Tangent(g5,g1) = -1.5708
    c: Tangent(g6,g3) = 1.5708
    c: Tangent(g7,g3) = -1.5708
    c: Tangent(g9,g2) = 1.5708
    c: Tangent(g8,g2) = 1.5708
    c: Tangent(g10,g0) = -1.5708
    c: Tangent(g11,g0) = -1.5708
    c: PointOnObject(g11,g-9)
    c: PointOnObject(g4,g-9)
    c: PointOnObject(g5,g-10)
    c: PointOnObject(g6,g-10)
    c: PointOnObject(g7,g-7)
    c: PointOnObject(g9,g-7)
    c: PointOnObject(g8,g-8)
    c: PointOnObject(g10,g-8)
    c: Coincident(g12,g9)
    c: Coincident(g12,g-8)
    c: Coincident(g13,g12)
    c: Coincident(g13,g8)
    c: Coincident(g14,g10)
    c: Coincident(g14,g-9)
    c: Coincident(g15,g14)
    c: Coincident(g15,g11)
    c: Coincident(g16,g4)
    c: Coincident(g16,g-10)
    c: Coincident(g17,g16)
    c: Coincident(g17,g5)
    c: Coincident(g18,g7)
    c: Coincident(g18,g-10)
    c: Coincident(g19,g18)
    c: Coincident(g19,g6)
    c: Equal(g20,g-3)
    c: Equal(g21,g-5)
    c: Equal(g22,g-6)
    c: Equal(g23,g-4)
    c: Coincident(g20,g0)
    c: Coincident(g21,g1)
    c: Coincident(g22,g3)
    c: Coincident(g23,g2)
FEATURE [Part::Extrusion] Extrude082  label="Extrude lato sx pistola - disegno anteriore"
  Base = -> Sketch082
  Dir = (0,-1,2e-16)
  DirMode = 2
  FaceMakerClass = Part::FaceMakerBullseye
  FaceMakerMode = 3
  LengthFwd = -1.6
  LengthRev = 0
  Placement = pos=(0,2,0) rot=(0,0,1;0rad)
  Solid = true
  Symmetric = false
FEATURE [Part::Extrusion] Extrude083  label="Extrude lato dx pistola - disegno anteriore"
  Base = -> Sketch083
  Dir = (0,-1,2e-16)
  DirMode = 2
  FaceMakerClass = Part::FaceMakerBullseye
  FaceMakerMode = 3
  LengthFwd = 1.6
  LengthRev = 0
  Placement = pos=(0,-2,0) rot=(0,0,1;0rad)
  Solid = true
  Symmetric = false
FEATURE [Part::Extrusion] Extrude084  label="Extrude lato sx pistola - spazi anteriori per viti"
  Base = -> Sketch084
  Dir = (0,-1,2e-16)
  DirMode = 2
  FaceMakerClass = Part::FaceMakerBullseye
  FaceMakerMode = 3
  LengthFwd = -1.6
  LengthRev = 0
  Placement = pos=(0,2,0) rot=(0,0,1;0rad)
  Solid = true
  Symmetric = false
FEATURE [Part::Extrusion] Extrude085  label="Extrude lato dx pistola - spazi anteriori per viti"
  Base = -> Sketch085
  Dir = (0,-1,2e-16)
  DirMode = 2
  FaceMakerClass = Part::FaceMakerBullseye
  FaceMakerMode = 3
  LengthFwd = 0.8
  LengthRev = 0
  Placement = pos=(0,-2.8,0) rot=(0,0,1;0rad)
  Solid = true
  Symmetric = false
FEATURE [Part::Cut] Cut048  label="Extrude lato dx pistola - disegno anterioro con fori viti"
  Base = -> Extrude083
  Refine = true
  Tool = -> Extrude085
FEATURE [Part::MultiFuse] Fusion006
  Refine = true
  Shapes = -> [Cut046,Cut048]
FEATURE [Sketcher::SketchObject] Sketch087  label="lato sx pistola - rialzo posteriore"
  ArcFitTolerance = 1e-06
  AttachmentSupport = -> [XZ_Plane]
  ExternalGeometry = -> [Sketch074]
  FullyConstrained = true
  MakeInternals = false
  MapMode = 5
  Placement = pos=(0,0,0) rot=(1,0,0;1.5708rad)
  sketch-geometry (10):
    g0: LineSegment StartX=-181.33 StartY=20.0744 StartZ=0 EndX=-144.029 EndY=20.0744 EndZ=0
    g1: LineSegment StartX=-137.815 StartY=39.2 StartZ=0 EndX=-144.029 EndY=20.0744 EndZ=0
    g2: LineSegment StartX=-178.754 StartY=39.2 StartZ=0 EndX=-137.815 EndY=39.2 EndZ=0
    g3: ArcOfCircle CenterX=-184.08 CenterY=34.8 CenterZ=0 NormalX=0 NormalY=0 NormalZ=1 AngleXU=0 Radius=3.5 StartAngle=4.71239 EndAngle=5.93412
    g4: LineSegment StartX=-178.754 StartY=39.2 StartZ=0 EndX=-180.791 EndY=33.6029 EndZ=0
    g5: GeomPoint [constr] X=-181.33 Y=20.0744 Z=0
    g6: LineSegment [constr] StartX=-181.33 StartY=20.0744 StartZ=0 EndX=-192.176 EndY=-3.18451 EndZ=0
    g7: LineSegment StartX=-184.08 StartY=31.3 StartZ=0 EndX=-186.139 EndY=31.3 EndZ=0
    g8: LineSegment StartX=-186.139 StartY=31.3 StartZ=0 EndX=-190.224 EndY=20.0744 EndZ=0
    g9: LineSegment StartX=-181.33 StartY=20.0744 StartZ=0 EndX=-190.224 EndY=20.0744 EndZ=0
  constraints (23):
    c: Horizontal(g0)
    c: Tangent(g1,g-5)
    c: PointOnObject(g2,g-4)
    c: Coincident(g2,g1)
    c: Radius(g3) = 3.5
    c: Coincident(g3,g-10)
    c: Horizontal(g2)
    c: Equal(g1,g-3)
    c: Coincident(g0,g1)
    c: Tangent(g4,g3) = 1.5708
    c: Coincident(g4,g2)
    c: Coincident(g6,g5)
    c: Tangent(g6,g-11) = -1.5708
    c: Coincident(g0,g5)
    c: Parallel(g4,g-3)
    c: Horizontal(g7)
    c: Parallel(g8,g-3)
    c: Tangent(g3,g7) = 1.5708
    c: Coincident(g8,g7)
    c: Coincident(g9,g0)
    c: Horizontal(g9)
    c: Coincident(g9,g8)
    c: DistanceX(g-8,g7) = 3.8
FEATURE [Sketcher::SketchObject] Sketch086  label="lato sx pistola - rialzo centrale"
  ArcFitTolerance = 1e-06
  AttachmentOffset = pos=(0,2,0) rot=(0,0,1;0rad)
  AttachmentSupport = -> [XZ_Plane]
  ExternalGeometry = -> [Sketch074,Sketch087]
  FullyConstrained = true
  MakeInternals = false
  MapMode = 5
  Placement = pos=(0,4e-16,2) rot=(1,0,0;1.5708rad)
  sketch-geometry (6):
    g0: LineSegment StartX=-137.815 StartY=37.2 StartZ=0 EndX=-142.793 EndY=21.8787 EndZ=0
    g1: LineSegment StartX=-137.815 StartY=37.2 StartZ=0 EndX=-110.815 EndY=37.2 EndZ=0
    g2: LineSegment StartX=-110.815 StartY=37.2 StartZ=0 EndX=-112.201 EndY=32.9344 EndZ=0
    g3: LineSegment StartX=-127.418 StartY=21.8787 StartZ=0 EndX=-142.793 EndY=21.8787 EndZ=0
    g4: ArcOfCircle CenterX=-127.418 CenterY=37.8787 CenterZ=0 NormalX=0 NormalY=0 NormalZ=1 AngleXU=0 Radius=16 StartAngle=4.71239 EndAngle=5.96903
    g5: GeomPoint [constr] X=-115.793 Y=21.8787 Z=0
  constraints (15):
    c: Distance(g1) = 27
    c: Coincident(g1,g0)
    c: PointOnObject(g1,g-4)
    c: Parallel(g2,g-3)
    c: Coincident(g2,g1)
    c: Horizontal(g3)
    c: PointOnObject(g5,g2)
    c: PointOnObject(g5,g3)
    c: Tangent(g2,g4) = 1.5708
    c: Tangent(g3,g4) = 1.5708
    c: Radius(g4) = 16
    c: Parallel(g0,g-7)
    c: Coincident(g0,g-7)
    c: Coincident(g0,g3)
    c: Distance(g0,g-7) = 4
FEATURE [Sketcher::SketchObject] Sketch088  label="lato sx pistola - rialzo impugnatura"
  ArcFitTolerance = 1e-06
  AttachmentSupport = -> [XZ_Plane]
  ExternalGeometry = -> [Sketch074,Sketch087]
  FullyConstrained = true
  MakeInternals = false
  MapMode = 5
  Placement = pos=(0,0,0) rot=(1,0,0;1.5708rad)
  sketch-geometry (11):
    g0: LineSegment StartX=-144.029 StartY=20.0744 StartZ=0 EndX=-176.685 EndY=-80.4316 EndZ=0
    g1: Circle CenterX=-213.443 CenterY=-76.8316 CenterZ=0 NormalX=0 NormalY=0 NormalZ=1 AngleXU=0 Radius=3
    g2: Circle CenterX=-179.305 CenterY=-76.8316 CenterZ=0 NormalX=0 NormalY=0 NormalZ=1 AngleXU=0 Radius=3
    g3: LineSegment StartX=-176.685 StartY=-80.4316 StartZ=0 EndX=-215.932 EndY=-80.4316 EndZ=0
    g4: LineSegment StartX=-192.176 StartY=-3.18451 StartZ=0 EndX=-215.42 EndY=-53.0314 EndZ=0
    g5: ArcOfCircle CenterX=-184.801 CenterY=-67.3089 CenterZ=0 NormalX=0 NormalY=0 NormalZ=1 AngleXU=0 Radius=33.7833 StartAngle=2.70526 EndAngle=3.54053
    g6: LineSegment [constr] StartX=-192.176 StartY=-3.18451 StartZ=0 EndX=-181.33 EndY=20.0744 EndZ=0
    g7: LineSegment StartX=-144.029 StartY=20.0744 StartZ=0 EndX=-190.224 EndY=20.0744 EndZ=0
    g8: LineSegment StartX=-190.224 StartY=20.0744 StartZ=0 EndX=-191.316 EndY=17.0744 EndZ=0
    g9: LineSegment StartX=-191.316 StartY=17.0744 StartZ=0 EndX=-182.729 EndY=17.0744 EndZ=0
    g10: LineSegment StartX=-192.176 StartY=-3.18451 StartZ=0 EndX=-182.729 EndY=17.0744 EndZ=0
  constraints (26):
    c: Coincident(g0,g-5)
    c: Coincident(g2,g-10)
    c: Coincident(g1,g-9)
    c: Diameter(g2) = 6
    c: Diameter(g1) = 6
    c: Coincident(g3,g0)
    c: Coincident(g3,g-4)
    c: Equal(g4,g-15)
    c: Parallel(g4,g-15)
    c: Coincident(g4,g-15)
    c: Coincident(g5,g4)
    c: Coincident(g5,g3)
    c: Tangent(g6,g4) = 1.5708
    c: PointOnObject(g6,g-13)
    c: Coincident(g0,g-13)
    c: Coincident(g7,g0)
    c: Coincident(g7,g-14)
    c: Coincident(g8,g7)
    c: Coincident(g9,g8)
    c: Horizontal(g9)
    c: PointOnObject(g9,g6)
    c: Coincident(g10,g4)
    c: Coincident(g10,g9)
    c: DistanceY(g8,g8) = 3
    c: Parallel(g8,g-16)
    c: Tangent(g5,g-3)
FEATURE [Sketcher::SketchObject] Sketch089  label="lato sx pistola - disegno centrale"
  ArcFitTolerance = 1e-06
  AttachmentSupport = -> [XZ_Plane]
  ExternalGeometry = -> [Sketch086]
  FullyConstrained = true
  MakeInternals = false
  MapMode = 5
  Placement = pos=(0,0,0) rot=(1,0,0;1.5708rad)
  sketch-geometry (4):
    g0: LineSegment StartX=-130.215 StartY=39.2 StartZ=0 EndX=-119.215 EndY=39.2 EndZ=0
    g1: LineSegment StartX=-130.215 StartY=39.2 StartZ=0 EndX=-132.81 EndY=31.2111 EndZ=0
    g2: LineSegment StartX=-119.215 StartY=39.2 StartZ=0 EndX=-121.81 EndY=31.2111 EndZ=0
    g3: LineSegment StartX=-132.81 StartY=31.2111 StartZ=0 EndX=-121.81 EndY=31.2111 EndZ=0
  constraints (11):
    c: Horizontal(g3)
    c: Parallel(g2,g-4)
    c: Parallel(g1,g-4)
    c: Distance(g1) = 8.4
    c: DistanceX(g0,g0) = 11
    c: Tangent(g0,g-3)
    c: Coincident(g1,g0)
    c: Coincident(g2,g0)
    c: Coincident(g3,g1)
    c: Coincident(g3,g2)
    c: DistanceX(g0,g-4) = 8.4
FEATURE [Sketcher::SketchObject] Sketch090  label="lato sx pistola - disegno pre centrale"
  ArcFitTolerance = 1e-06
  AttachmentSupport = -> [XZ_Plane]
  ExternalGeometry = -> [Sketch074,Sketch086]
  FullyConstrained = true
  MakeInternals = false
  MapMode = 5
  Placement = pos=(0,0,0) rot=(1,0,0;1.5708rad)
  sketch-geometry (4):
    g0: LineSegment StartX=-106.615 StartY=36.8 StartZ=0 EndX=-89.6146 EndY=36.8 EndZ=0
    g1: LineSegment StartX=-110.254 StartY=26.8 StartZ=0 EndX=-89.6146 EndY=26.8 EndZ=0
    g2: LineSegment StartX=-106.615 StartY=36.8 StartZ=0 EndX=-110.254 EndY=26.8 EndZ=0
    g3: ArcOfCircle CenterX=-94.6146 CenterY=31.8 CenterZ=0 NormalX=0 NormalY=0 NormalZ=1 AngleXU=0 Radius=7.07107 StartAngle=5.49779 EndAngle=7.06858
  constraints (13):
    c: Horizontal(g0)
    c: Horizontal(g1)
    c: Parallel(g-3,g2)
    c: Coincident(g0,g2)
    c: DistanceY(g2,g2) = 10
    c: Coincident(g1,g2)
    c: DistanceX(g0,g0) = 17
    c: DistanceX(g0,g1) = 0
    c: Coincident(g3,g1)
    c: DistanceX(g-5,g0) = 4.2
    c: DistanceY(g0,g-5) = 2.4
    c: Coincident(g3,g0)
    c: DistanceX(g3,g0) = 5
FEATURE [PartDesign::Body] Body  label="Struttura pistola"
  AllowCompound = false
  Group = -> [Sketch,Sketch002,Sketch004,DatumPlane,Sketch005,DatumPlane001,CopyCut,Sketch008,Sketch009,Sketch010,Sketch011,Sketch012,Sketch013,Sketch014,Sketch015,Sketch016,Sketch017,Sketch018,Sketch019,Sketch020,Sketch022,Sketch023,Sketch024,Sketch025,Sketch026,Sketch027,Sketch029,Sketch030,Sketch031,Sketch032,Sketch033,Sketch034,Sketch035,Sketch036,Sketch037,Sketch038,Sketch039,Sketch040,Sketch041,Sketch042,+28 more]
  Origin = -> Origin
FEATURE [PartDesign::SubShapeBinder] Binder
  BindCopyOnChange = 0
  BindMode = 0
  ClaimChildren = false
  Context = -> Body006 [Binder.]
  Fuse = false
  MakeFace = true
  OffsetFill = false
  OffsetIntersection = false
  OffsetJoinType = 0
  OffsetOpenResult = false
  PartialLoad = false
  Refine = true
  Relative = true
  Support = -> [Body[Sketch074.]]
  _Version = 2
FEATURE [PartDesign::SubShapeBinder] Binder001
  BindCopyOnChange = 0
  BindMode = 0
  ClaimChildren = false
  Context = -> Body007 [Binder001.]
  Fuse = false
  MakeFace = true
  OffsetFill = false
  OffsetIntersection = false
  OffsetJoinType = 0
  OffsetOpenResult = false
  PartialLoad = false
  Refine = true
  Relative = true
  Support = -> [Body[Sketch075.]]
  _Version = 2
FEATURE [PartDesign::Pad] Pad004
  Direction = (0,1,0)
  Length = 2
  Length2 = 10
  Profile = -> Binder
  Refine = true
  Suppressed = false
  Type = 0
FEATURE [Sketcher::SketchObject] Sketch091  label="Sketch091 - forma anteriore"
  ArcFitTolerance = 1e-06
  AttachmentSupport = -> [Pad004]
  ExternalGeometry = -> [Binder]
  FullyConstrained = true
  MakeInternals = false
  MapMode = 5
  Placement = pos=(0,2,0) rot=(0,0.707107,0.707107;3.14159rad)
  sketch-geometry (12):
    g0: Circle CenterX=5.6 CenterY=34.8 CenterZ=0 NormalX=0 NormalY=0 NormalZ=1 AngleXU=0 Radius=1.8
    g1: Circle CenterX=5.6 CenterY=7.6 CenterZ=0 NormalX=0 NormalY=0 NormalZ=1 AngleXU=0 Radius=1.8
    g2: Circle CenterX=78.51 CenterY=34.8 CenterZ=0 NormalX=0 NormalY=0 NormalZ=1 AngleXU=0 Radius=1.8
    g3: Circle CenterX=78.51 CenterY=7.6 CenterZ=0 NormalX=0 NormalY=0 NormalZ=1 AngleXU=0 Radius=1.8
    g4: LineSegment StartX=0 StartY=39.2 StartZ=0 EndX=0 EndY=3.2 EndZ=0
    g5: LineSegment StartX=0 StartY=3.2 StartZ=0 EndX=82.8 EndY=3.2 EndZ=0
    g6: LineSegment StartX=82.8 StartY=3.2 StartZ=0 EndX=82.8 EndY=39.2 EndZ=0
    g7: LineSegment StartX=82.8 StartY=39.2 StartZ=0 EndX=0 EndY=39.2 EndZ=0
    g8: ArcOfCircle CenterX=19 CenterY=21.2 CenterZ=0 NormalX=0 NormalY=0 NormalZ=1 AngleXU=0 Radius=10 StartAngle=1.5708 EndAngle=4.71239
    g9: ArcOfCircle CenterX=65 CenterY=21.2 CenterZ=0 NormalX=0 NormalY=0 NormalZ=1 AngleXU=0 Radius=10 StartAngle=4.71239 EndAngle=7.85398
    g10: LineSegment StartX=19 StartY=31.2 StartZ=0 EndX=65 EndY=31.2 EndZ=0
    g11: LineSegment StartX=19 StartY=11.2 StartZ=0 EndX=65 EndY=11.2 EndZ=0
  constraints (25):
    c: Equal(g2,g-7)
    c: Equal(g3,g-8)
    c: Equal(g1,g-13)
    c: Equal(g0,g-12)
    c: Coincident(g0,g-12)
    c: Coincident(g1,g-13)
    c: Coincident(g3,g-8)
    c: Coincident(g2,g-7)
    c: Coincident(g4,g-4)
    c: Coincident(g4,g-5)
    c: Coincident(g5,g4)
    c: Coincident(g5,g-6)
    c: Coincident(g6,g5)
    c: PointOnObject(g6,g-3)
    c: Vertical(g6)
    c: Coincident(g7,g6)
    c: Coincident(g7,g4)
    c: Tangent(g8,g10) = 1.5708
    c: Tangent(g8,g11) = -1.5708
    c: Tangent(g9,g10) = 1.5708
    c: Tangent(g9,g11) = -1.5708
    c: Equal(g8,g9)
    c: Radius(g8) = 10
    c: Coincident(g8,g-11)
    c: Coincident(g9,g-9)
FEATURE [PartDesign::Pad] Pad005
  BaseFeature = -> Pad004
  Direction = (0,1,-2e-16)
  Length = 1.6
  Length2 = 10
  Profile = -> Sketch091
  ReferenceAxis = -> Sketch091 [N_Axis]
  Refine = true
  Suppressed = false
  Type = 0
FEATURE [Sketcher::SketchObject] Sketch092  label="Sketch092 - scavi per viti anteriori"
  ArcFitTolerance = 1e-06
  AttachmentSupport = -> [Pad005]
  ExternalGeometry = -> [Binder]
  FullyConstrained = true
  MakeInternals = false
  MapMode = 5
  Placement = pos=(0,3.6,0) rot=(0,0.707107,0.707107;3.14159rad)
  sketch-geometry (20):
    g0: ArcOfCircle CenterX=5.6 CenterY=7.6 CenterZ=0 NormalX=0 NormalY=0 NormalZ=1 AngleXU=0 Radius=3.5 StartAngle=0 EndAngle=1.5708
    g1: ArcOfCircle CenterX=5.6 CenterY=34.8 CenterZ=0 NormalX=0 NormalY=0 NormalZ=1 AngleXU=0 Radius=3.5 StartAngle=4.71239 EndAngle=6.28319
    g2: ArcOfCircle CenterX=78.51 CenterY=34.8 CenterZ=0 NormalX=0 NormalY=0 NormalZ=1 AngleXU=0 Radius=3.5 StartAngle=3.14159 EndAngle=4.71239
    g3: ArcOfCircle CenterX=78.51 CenterY=7.6 CenterZ=0 NormalX=0 NormalY=0 NormalZ=1 AngleXU=0 Radius=3.5 StartAngle=1.5708 EndAngle=3.14159
    g4: LineSegment StartX=0 StartY=3.2 StartZ=0 EndX=0 EndY=11.1 EndZ=0
    g5: LineSegment StartX=0 StartY=11.1 StartZ=0 EndX=5.6 EndY=11.1 EndZ=0
    g6: LineSegment StartX=0 StartY=3.2 StartZ=0 EndX=9.1 EndY=3.2 EndZ=0
    g7: LineSegment StartX=9.1 StartY=3.2 StartZ=0 EndX=9.1 EndY=7.6 EndZ=0
    g8: LineSegment StartX=0 StartY=39.2 StartZ=0 EndX=0 EndY=31.3 EndZ=0
    g9: LineSegment StartX=0 StartY=31.3 StartZ=0 EndX=5.6 EndY=31.3 EndZ=0
    g10: LineSegment StartX=0 StartY=39.2 StartZ=0 EndX=9.1 EndY=39.2 EndZ=0
    g11: LineSegment StartX=9.1 StartY=39.2 StartZ=0 EndX=9.1 EndY=34.8 EndZ=0
    g12: LineSegment StartX=82.8 StartY=39.2 StartZ=0 EndX=75.01 EndY=39.2 EndZ=0
    g13: LineSegment StartX=82.8 StartY=39.2 StartZ=0 EndX=82.8 EndY=31.3 EndZ=0
    g14: LineSegment StartX=82.8 StartY=31.3 StartZ=0 EndX=78.51 EndY=31.3 EndZ=0
    g15: LineSegment StartX=82.8 StartY=3.2 StartZ=0 EndX=75.01 EndY=3.2 EndZ=0
    g16: LineSegment StartX=75.01 StartY=3.2 StartZ=0 EndX=75.01 EndY=7.6 EndZ=0
    g17: LineSegment StartX=82.8 StartY=3.2 StartZ=0 EndX=82.8 EndY=11.1 EndZ=0
    g18: LineSegment StartX=82.8 StartY=11.1 StartZ=0 EndX=78.51 EndY=11.1 EndZ=0
    g19: LineSegment StartX=75.01 StartY=39.2 StartZ=0 EndX=75.01 EndY=34.8 EndZ=0
  constraints (48):
    c: Radius(g0) = 3.5
    c: Coincident(g0,g-10)
    c: Radius(g1) = 3.5
    c: Coincident(g1,g-9)
    c: Radius(g2) = 3.5
    c: Coincident(g2,g-8)
    c: Radius(g3) = 3.5
    c: Coincident(g3,g-7)
    c: Coincident(g4,g-5)
    c: PointOnObject(g4,g-4)
    c: Coincident(g5,g4)
    c: Horizontal(g5)
    c: Coincident(g6,g4)
    c: PointOnObject(g6,g-5)
    c: Coincident(g7,g6)
    c: Vertical(g7)
    c: Coincident(g8,g-4)
    c: PointOnObject(g8,g-4)
    c: Coincident(g9,g8)
    c: Horizontal(g9)
    c: Coincident(g10,g8)
    c: PointOnObject(g10,g-3)
    c: Coincident(g11,g10)
    c: Vertical(g11)
    c: PointOnObject(g12,g-3)
    c: PointOnObject(g12,g-3)
    c: Coincident(g13,g12)
    c: Vertical(g13)
    c: Coincident(g14,g13)
    c: Horizontal(g14)
    c: Coincident(g15,g-6)
    c: PointOnObject(g15,g-5)
    c: Coincident(g16,g15)
    c: Vertical(g16)
    c: Coincident(g17,g15)
    c: Coincident(g18,g17)
    c: Horizontal(g18)
    c: Tangent(g3,g18) = -1.5708
    c: Tangent(g16,g3) = 1.5708
    c: Coincident(g19,g12)
    c: Vertical(g19)
    c: Tangent(g2,g19) = -1.5708
    c: Tangent(g2,g14) = 1.5708
    c: Tangent(g0,g7) = -1.5708
    c: Tangent(g0,g5) = 1.5708
    c: Tangent(g9,g1) = -1.5708
    c: Tangent(g1,g11) = 1.5708
    c: Tangent(g17,g13)
FEATURE [PartDesign::Pocket] Pocket001
  BaseFeature = -> Pad005
  Direction = (0,-1,2e-16)
  Length = 1.6
  Length2 = 5
  Profile = -> Sketch092
  ReferenceAxis = -> Sketch092 [N_Axis]
  Refine = true
  Suppressed = false
  Type = 0
FEATURE [Sketcher::SketchObject] Sketch093  label="Sketch093 - scavi interni pulsanti"
  ArcFitTolerance = 1e-06
  AttachmentSupport = -> [Pad004]
  ExternalGeometry = -> [Binder]
  FullyConstrained = true
  MakeInternals = false
  MapMode = 5
  Placement = pos=(0,9e-16,0) rot=(1,0,0;1.5708rad)
  sketch-geometry (3):
    g0: Circle CenterX=-65 CenterY=21.2 CenterZ=0 NormalX=0 NormalY=0 NormalZ=1 AngleXU=0 Radius=7.3
    g1: Circle CenterX=-42 CenterY=21.2 CenterZ=0 NormalX=0 NormalY=0 NormalZ=1 AngleXU=0 Radius=7.3
    g2: Circle CenterX=-19 CenterY=21.2 CenterZ=0 NormalX=0 NormalY=0 NormalZ=1 AngleXU=0 Radius=7.3
  constraints (6):
    c: Coincident(g0,g-3)
    c: Coincident(g1,g-4)
    c: Coincident(g2,g-5)
    c: Diameter(g0) = 14.6
    c: Diameter(g1) = 14.6
    c: Diameter(g2) = 14.6
FEATURE [PartDesign::Pocket] Pocket002
  BaseFeature = -> Pocket001
  Direction = (0,1,-2e-16)
  Length = 1.2
  Length2 = 5
  Profile = -> Sketch093
  ReferenceAxis = -> Sketch093 [N_Axis]
  Refine = true
  Suppressed = false
  Type = 0
FEATURE [Sketcher::SketchObject] Sketch094  label="Sketch094 - forma centrale"
  ArcFitTolerance = 1e-06
  AttachmentSupport = -> [Pad004]
  ExternalGeometry = -> [Binder]
  FullyConstrained = true
  MakeInternals = false
  MapMode = 5
  Placement = pos=(0,2,0) rot=(0,0.707107,0.707107;3.14159rad)
  sketch-geometry (4):
    g0: LineSegment StartX=137.815 StartY=39.2 StartZ=0 EndX=142.655 EndY=24.303 EndZ=0
    g1: LineSegment StartX=110.815 StartY=24.303 StartZ=0 EndX=142.655 EndY=24.303 EndZ=0
    g2: LineSegment StartX=137.815 StartY=39.2 StartZ=0 EndX=110.815 EndY=39.2 EndZ=0
    g3: ArcOfCircle CenterX=92.2534 CenterY=31.7515 CenterZ=0 NormalX=0 NormalY=0 NormalZ=1 AngleXU=0 Radius=20 StartAngle=5.90156 EndAngle=6.66481
  constraints (12):
    c: PointOnObject(g0,g-3)
    c: Tangent(g0,g-5)
    c: Horizontal(g1)
    c: Coincident(g1,g0)
    c: Coincident(g2,g0)
    c: PointOnObject(g2,g-3)
    c: DistanceX(g2,g2) = 27
    c: Vertical(g1,g2)
    c: Coincident(g3,g2)
    c: Radius(g3) = 20
    c: Coincident(g3,g1)
    c: DistanceY(g-6,g0) = 4
FEATURE [PartDesign::Pad] Pad006
  BaseFeature = -> Pocket002
  Direction = (0,1,-2e-16)
  Length = 0.8
  Length2 = 10
  Profile = -> Sketch094
  ReferenceAxis = -> Sketch094 [N_Axis]
  Refine = true
  Suppressed = false
  Type = 0
FEATURE [Sketcher::SketchObject] Sketch095  label="Sketch095 - forma posteriore"
  ArcFitTolerance = 1e-06
  AttachmentSupport = -> [Pad004]
  ExternalGeometry = -> [Binder]
  FullyConstrained = true
  MakeInternals = false
  MapMode = 5
  Placement = pos=(0,2,0) rot=(0,0.707107,0.707107;3.14159rad)
  sketch-geometry (15):
    g0: LineSegment StartX=137.815 StartY=39.2 StartZ=0 EndX=143.955 EndY=20.303 EndZ=0
    g1: LineSegment StartX=143.955 StartY=20.303 StartZ=0 EndX=190.141 EndY=20.303 EndZ=0
    g2: ArcOfCircle CenterX=184.08 CenterY=34.8 CenterZ=0 NormalX=0 NormalY=0 NormalZ=1 AngleXU=0 Radius=3.5 StartAngle=3.49066 EndAngle=4.71239
    g3: LineSegment StartX=180.791 StartY=33.6029 StartZ=0 EndX=178.754 EndY=39.2 EndZ=0
    g4: LineSegment StartX=184.08 StartY=31.3 StartZ=0 EndX=186.139 EndY=31.3 EndZ=0
    g5: LineSegment StartX=190.141 StartY=20.303 StartZ=0 EndX=186.139 EndY=31.3 EndZ=0
    g6: LineSegment StartX=137.815 StartY=39.2 StartZ=0 EndX=156.815 EndY=39.2 EndZ=0
    g7: LineSegment StartX=178.754 StartY=39.2 StartZ=0 EndX=168.815 EndY=39.2 EndZ=0
    g8: LineSegment StartX=156.815 StartY=31.2 StartZ=0 EndX=168.815 EndY=31.2 EndZ=0
    g9: ArcOfCircle CenterX=176.411 CenterY=35.2 CenterZ=0 NormalX=0 NormalY=0 NormalZ=1 AngleXU=0 Radius=20 StartAngle=2.94023 EndAngle=3.34295
    g10: ArcOfCircle CenterX=188.411 CenterY=35.2 CenterZ=0 NormalX=0 NormalY=0 NormalZ=1 AngleXU=0 Radius=20 StartAngle=2.94023 EndAngle=3.34295
    g11: LineSegment StartX=157.815 StartY=39.2 StartZ=0 EndX=167.815 EndY=39.2 EndZ=0
    g12: LineSegment StartX=157.436 StartY=36.2 StartZ=0 EndX=167.436 EndY=36.2 EndZ=0
    g13: ArcOfCircle CenterX=177.411 CenterY=35.2 CenterZ=0 NormalX=0 NormalY=0 NormalZ=1 AngleXU=0 Radius=20 StartAngle=2.94023 EndAngle=3.09157
    g14: ArcOfCircle CenterX=187.411 CenterY=35.2 CenterZ=0 NormalX=0 NormalY=0 NormalZ=1 AngleXU=0 Radius=20 StartAngle=2.94023 EndAngle=3.09157
  constraints (46):
    c: PointOnObject(g0,g-3)
    c: Tangent(g0,g-6)
    c: Coincident(g1,g0)
    c: Horizontal(g1)
    c: Radius(g2) = 3.5
    c: Coincident(g2,g-5)
    c: PointOnObject(g3,g-3)
    c: Parallel(g3,g-4)
    c: Tangent(g3,g2) = 1.5708
    c: Horizontal(g4)
    c: Tangent(g4,g2) = -1.5708
    c: Coincident(g5,g1)
    c: Parallel(g5,g-4)
    c: Coincident(g5,g4)
    c: DistanceX(g4,g-8) = 3.8
    c: Coincident(g6,g0)
    c: PointOnObject(g6,g-3)
    c: Coincident(g7,g3)
    c: PointOnObject(g7,g-3)
    c: Horizontal(g8)
    c: DistanceX(g6,g7) = 12
    c: Vertical(g8,g6)
    c: Vertical(g7,g8)
    c: DistanceY(g8,g6) = 8
    c: Coincident(g9,g8)
    c: Coincident(g9,g6)
    c: Coincident(g10,g7)
    c: Coincident(g10,g8)
    c: Radius(g9) = 20
    c: Radius(g10) = 20
    c: PointOnObject(g11,g-3)
    c: PointOnObject(g11,g-3)
    c: DistanceX(g11,g11) = 10
    c: DistanceX(g6,g11) = 1
    c: Horizontal(g12)
    c: Equal(g12,g11)
    c: DistanceY(g12,g11) = 3
    c: Coincident(g13,g11)
    c: Coincident(g13,g12)
    c: Radius(g13) = 20
    c: Coincident(g14,g11)
    c: Coincident(g14,g12)
    c: Radius(g14) = 20
    c: DistanceX(g0,g6) = 19
    c: Horizontal(g9,g13)
    c: Horizontal(g0,g-4)
FEATURE [PartDesign::Pad] Pad007
  BaseFeature = -> Pad006
  Direction = (0,1,-2e-16)
  Length = 2
  Length2 = 10
  Profile = -> Sketch095
  ReferenceAxis = -> Sketch095 [N_Axis]
  Refine = true
  Suppressed = false
  Type = 0
FEATURE [Sketcher::SketchObject] Sketch096  label="Sketch096 - forma impugnatura"
  ArcFitTolerance = 1e-06
  AttachmentSupport = -> [Pad004]
  ExternalGeometry = -> [Binder]
  FullyConstrained = true
  MakeInternals = false
  MapMode = 5
  Placement = pos=(0,2,0) rot=(0,0.707107,0.707107;3.14159rad)
  sketch-geometry (8):
    g0: LineSegment StartX=176.685 StartY=-80.4316 StartZ=0 EndX=143.955 EndY=20.303 EndZ=0
    g1: LineSegment StartX=176.685 StartY=-80.4316 StartZ=0 EndX=215.932 EndY=-80.4316 EndZ=0
    g2: Circle CenterX=179.305 CenterY=-76.8316 CenterZ=0 NormalX=0 NormalY=0 NormalZ=1 AngleXU=0 Radius=3
    g3: Circle CenterX=213.443 CenterY=-76.8316 CenterZ=0 NormalX=0 NormalY=0 NormalZ=1 AngleXU=0 Radius=3
    g4: LineSegment StartX=143.955 StartY=20.303 StartZ=0 EndX=202.765 EndY=20.303 EndZ=0
    g5: LineSegment StartX=215.42 StartY=-53.0314 StartZ=0 EndX=192.176 EndY=-3.18451 EndZ=0
    g6: ArcOfCircle CenterX=184.801 CenterY=-67.3089 CenterZ=0 NormalX=0 NormalY=0 NormalZ=1 AngleXU=0 Radius=33.7833 StartAngle=5.88425 EndAngle=6.71952
    g7: ArcOfCircle CenterX=207.583 CenterY=4 CenterZ=0 NormalX=0 NormalY=0 NormalZ=1 AngleXU=0 Radius=17 StartAngle=1.85815 EndAngle=3.57792
  constraints (19):
    c: Coincident(g0,g-4)
    c: PointOnObject(g0,g-3)
    c: Horizontal(g0,g-7)
    c: Coincident(g1,g0)
    c: Coincident(g1,g-5)
    c: Diameter(g2) = 6
    c: Diameter(g3) = 6
    c: Coincident(g2,g-9)
    c: Coincident(g3,g-10)
    c: Coincident(g4,g0)
    c: Coincident(g5,g-6)
    c: Coincident(g6,g1)
    c: Coincident(g6,g5)
    c: Equal(g-5,g6)
    c: Coincident(g5,g-7)
    c: Coincident(g4,g-7)
    c: Tangent(g7,g-7)
    c: Coincident(g7,g4)
    c: Coincident(g7,g5)
FEATURE [PartDesign::Pad] Pad008  label="Pad008 - forma impugnatura"
  BaseFeature = -> Pad007
  Direction = (0,1,-2e-16)
  Length = 1.6
  Length2 = 10
  Profile = -> Sketch096
  ReferenceAxis = -> Sketch096 [N_Axis]
  Refine = true
  Suppressed = false
  Type = 0
FEATURE [Sketcher::SketchObject] Sketch097
  ArcFitTolerance = 1e-06
  AttachmentSupport = -> [Pad004]
  ExternalGeometry = -> [Binder]
  FullyConstrained = true
  MakeInternals = false
  MapMode = 5
  Placement = pos=(0,2,0) rot=(0,0.707107,0.707107;3.14159rad)
  sketch-geometry (4):
    g0: LineSegment StartX=90 StartY=36.8 StartZ=0 EndX=108 EndY=36.8 EndZ=0
    g1: LineSegment StartX=108 StartY=36.8 StartZ=0 EndX=108 EndY=26.8 EndZ=0
    g2: LineSegment StartX=108 StartY=26.8 StartZ=0 EndX=90 EndY=26.8 EndZ=0
    g3: ArcOfCircle CenterX=94 CenterY=31.8 CenterZ=0 NormalX=0 NormalY=0 NormalZ=1 AngleXU=0 Radius=6.40312 StartAngle=2.24554 EndAngle=4.03765
  constraints (13):
    c: Horizontal(g0)
    c: Coincident(g1,g0)
    c: Vertical(g1)
    c: DistanceX(g0,g0) = 18
    c: DistanceY(g1,g1) = 10
    c: Coincident(g2,g1)
    c: Horizontal(g2)
    c: Equal(g2,g0)
    c: DistanceY(g0,g-3) = 2.4
    c: Coincident(g3,g0)
    c: Coincident(g3,g2)
    c: DistanceX(g2,g3) = 4
    c: DistanceX(g-3,g0) = 90
FEATURE [PartDesign::Pad] Pad009
  BaseFeature = -> Pad008
  Direction = (0,1,-2e-16)
  Length = 1.6
  Length2 = 10
  Profile = -> Sketch097
  ReferenceAxis = -> Sketch097 [N_Axis]
  Refine = true
  Suppressed = false
  Type = 0
FEATURE [Sketcher::SketchObject] Sketch098
  ArcFitTolerance = 1e-06
  AttachmentSupport = -> [Pad006]
  ExternalGeometry = -> [Binder]
  FullyConstrained = true
  MakeInternals = false
  MapMode = 5
  Placement = pos=(0,2.8,-7e-16) rot=(0,0.707107,0.707107;3.14159rad)
  sketch-geometry (4):
    g0: LineSegment StartX=118 StartY=39.2 StartZ=0 EndX=129 EndY=39.2 EndZ=0
    g1: LineSegment StartX=120.599 StartY=31.2 StartZ=0 EndX=131.599 EndY=31.2 EndZ=0
    g2: LineSegment StartX=129 StartY=39.2 StartZ=0 EndX=131.599 EndY=31.2 EndZ=0
    g3: LineSegment StartX=118 StartY=39.2 StartZ=0 EndX=120.599 EndY=31.2 EndZ=0
  constraints (12):
    c: PointOnObject(g0,g-3)
    c: PointOnObject(g0,g-3)
    c: DistanceX(g0,g0) = 11
    c: Horizontal(g1)
    c: Equal(g1,g0)
    c: Coincident(g2,g0)
    c: Coincident(g3,g0)
    c: Parallel(g-4,g2)
    c: Coincident(g1,g2)
    c: Coincident(g1,g3)
    c: DistanceY(g1,g0) = 8
    c: DistanceX(g-3,g0) = 118
FEATURE [PartDesign::Pad] Pad010
  BaseFeature = -> Pad009
  Direction = (0,1,-2e-16)
  Length = 1.2
  Length2 = 10
  Profile = -> Sketch098
  ReferenceAxis = -> Sketch098 [N_Axis]
  Refine = true
  Suppressed = false
  Type = 0
FEATURE [Sketcher::SketchObject] Sketch099
  ArcFitTolerance = 1e-06
  AttachmentSupport = -> [Pad008]
  ExternalGeometry = -> [Binder]
  FullyConstrained = true
  MakeInternals = false
  MapMode = 5
  Placement = pos=(0,3.6,0) rot=(0,0.707107,0.707107;3.14159rad)
  sketch-geometry (13):
    g0: LineSegment StartX=192.176 StartY=-3.18451 StartZ=0 EndX=196.804 EndY=-13.1108 EndZ=0
    g1: LineSegment [constr] StartX=202.765 StartY=20.303 StartZ=0 EndX=181.223 EndY=20.303 EndZ=0
    g2: LineSegment [constr] StartX=181.223 StartY=20.303 StartZ=0 EndX=181.223 EndY=-3.18451 EndZ=0
    g3: ArcOfCircle CenterX=181.223 CenterY=-20.3764 CenterZ=0 NormalX=0 NormalY=0 NormalZ=1 AngleXU=0 Radius=17.1918 StartAngle=0.436332 EndAngle=1.57079
    g4: ArcOfEllipse CenterX=181.223 CenterY=8.55923 CenterZ=0 NormalX=0 NormalY=0 NormalZ=1 MajorRadius=23.4779 MinorRadius=11.7437 AngleXU=0 StartAngle=1.5708 EndAngle=4.71239
    g5: LineSegment [constr] StartX=204.701 StartY=8.55923 StartZ=0 EndX=157.745 EndY=8.55923 EndZ=0
    g6: LineSegment [constr] StartX=181.223 StartY=20.303 StartZ=0 EndX=181.223 EndY=-3.18451 EndZ=0
    g7: GeomPoint [constr] X=201.553 Y=8.55923 Z=0
    g8: GeomPoint [constr] X=160.894 Y=8.55923 Z=0
    g9: GeomPoint [constr] X=181.223 Y=-3.18451 Z=0
    g10: LineSegment StartX=181.223 StartY=20.303 StartZ=0 EndX=202.765 EndY=20.303 EndZ=0
    g11: ArcOfCircle CenterX=207.583 CenterY=4 CenterZ=0 NormalX=0 NormalY=0 NormalZ=1 AngleXU=0 Radius=17 StartAngle=1.85815 EndAngle=3.57792
    g12: LineSegment [constr] StartX=172.411 StartY=39.2 StartZ=0 EndX=192.176 EndY=-3.18451 EndZ=0
  constraints (27):
    c: Coincident(g1,g-7)
    c: Horizontal(g1)
    c: Coincident(g2,g1)
    c: Vertical(g2)
    c: Horizontal(g2,g0)
    c: Coincident(g3,g0)
    c: Coincident(g3,g2)
    c: InternalAlignment(g5-g8 -> g4) x4
    c: Horizontal(g5)
    c: PointOnObject(g4,g2)
    c: Coincident(g4,g1)
    c: DistanceX(g-3,g5) = 10.1
    c: Coincident(g4,g2)
    c: Tangent(g3,g-5)
    c: PointOnObject(g9,g4)
    c: PointOnObject(g9,g3)
    c: Tangent(g4,g3,g9) = 1.5708
    c: Coincident(g10,g1)
    c: Coincident(g10,g1)
    c: Equal(g11,g-4)
    c: Coincident(g11,g1)
    c: Coincident(g11,g0)
    c: PointOnObject(g12,g-6)
    c: PointOnObject(g1,g12)
    c: Tangent(g12,g-5) = -1.5708
    c: Tangent(g0,g-5) = -1.5708
    c: Horizontal(g9,g12)
FEATURE [Sketcher::SketchObject] Sketch106  label="Sketch106 - smusso impuniatura interno"
  ArcFitTolerance = 1e-06
  AttachmentSupport = -> [Pad008]
  ExternalGeometry = -> [Pad008]
  FullyConstrained = true
  MakeInternals = false
  MapMode = 5
  Placement = pos=(0,0,-80.4316) rot=(1,0,0;3.14159rad)
  sketch-geometry (9):
    g0: LineSegment StartX=-176.685 StartY=-3.6 StartZ=0 EndX=-176.685 EndY=1.168e-12 EndZ=0
    g1: LineSegment [constr] StartX=-176.685 StartY=1.79e-14 StartZ=0 EndX=-176.685 EndY=1.1682e-12 EndZ=0
    g2: LineSegment [constr] StartX=-186.685 StartY=-3.6 StartZ=0 EndX=-186.685 EndY=1.168e-12 EndZ=0
    g3: ArcOfEllipse CenterX=-186.685 CenterY=1.1682e-12 CenterZ=0 NormalX=0 NormalY=0 NormalZ=1 MajorRadius=10 MinorRadius=3.6 AngleXU=-3.14159 StartAngle=1.5708 EndAngle=3.14159
    g4: LineSegment [constr] StartX=-196.685 StartY=1.79e-14 StartZ=0 EndX=-176.685 EndY=1.79e-14 EndZ=0
    g5: LineSegment [constr] StartX=-186.685 StartY=-3.6 StartZ=0 EndX=-186.685 EndY=3.6 EndZ=0
    g6: GeomPoint [constr] X=-196.015 Y=1.6e-14 Z=0
    g7: GeomPoint [constr] X=-177.356 Y=1.85e-14 Z=0
    g8: LineSegment StartX=-176.685 StartY=-3.6 StartZ=0 EndX=-186.685 EndY=-3.6 EndZ=0
  constraints (15):
    c: PointOnObject(g2,g-3)
    c: Coincident(g1,g-5)
    c: DistanceY(g1,g1) = 0
    c: Coincident(g0,g1)
    c: DistanceX(g2,g-5) = 10
    c: Vertical(g2)
    c: Horizontal(g2,g0)
    c: InternalAlignment(g4-g7 -> g3) x4
    c: Coincident(g3,g2)
    c: Horizontal(g4)
    c: Coincident(g3,g0)
    c: Tangent(g0,g-5) = 1.5708
    c: Coincident(g3,g2)
    c: Coincident(g8,g0)
    c: Coincident(g8,g2)
FEATURE [Sketcher::SketchObject] Sketch107  label="Sketch107 - smusso impugnatura esterno"
  ArcFitTolerance = 1e-06
  AttachmentSupport = -> [Pad008]
  ExternalGeometry = -> [Pad008]
  FullyConstrained = true
  MakeInternals = false
  MapMode = 5
  Placement = pos=(0,0,-80.4316) rot=(1,0,0;3.14159rad)
  sketch-geometry (9):
    g0: LineSegment [constr] StartX=-215.932 StartY=1.79e-14 StartZ=0 EndX=-215.932 EndY=1.94e-14 EndZ=0
    g1: LineSegment StartX=-215.932 StartY=-3.6 StartZ=0 EndX=-215.932 EndY=1.95e-14 EndZ=0
    g2: LineSegment StartX=-215.932 StartY=-3.6 StartZ=0 EndX=-205.932 EndY=-3.6 EndZ=0
    g3: LineSegment [constr] StartX=-205.932 StartY=-3.6 StartZ=0 EndX=-205.932 EndY=1.95e-14 EndZ=0
    g4: ArcOfEllipse CenterX=-205.932 CenterY=1.94e-14 CenterZ=0 NormalX=0 NormalY=0 NormalZ=1 MajorRadius=10 MinorRadius=3.6 AngleXU=3.14159 StartAngle=1e-16 EndAngle=1.5708
    g5: LineSegment [constr] StartX=-215.932 StartY=1.79e-14 StartZ=0 EndX=-195.932 EndY=1.79e-14 EndZ=0
    g6: LineSegment [constr] StartX=-205.932 StartY=-3.6 StartZ=0 EndX=-205.932 EndY=3.6 EndZ=0
    g7: GeomPoint [constr] X=-215.262 Y=1.97e-14 Z=0
    g8: GeomPoint [constr] X=-196.602 Y=1.78e-14 Z=0
  constraints (16):
    c: Coincident(g0,g-6)
    c: PointOnObject(g0,g-6)
    c: DistanceY(g0,g0) = 0
    c: Coincident(g1,g-6)
    c: Coincident(g1,g0)
    c: Tangent(g2,g-3)
    c: DistanceX(g2,g2) = 10
    c: Coincident(g3,g2)
    c: Vertical(g3)
    c: Horizontal(g3,g0)
    c: InternalAlignment(g5-g8 -> g4) x4
    c: Coincident(g4,g3)
    c: Horizontal(g5)
    c: Coincident(g4,g0)
    c: Coincident(g4,g2)
    c: PointOnObject(g2,g1)
FEATURE [PartDesign::SubtractivePipe] SubtractivePipe
  AuxilleryCurvelinear = true
  AuxillerySpineTangent = false
  BaseFeature = -> Pad010
  Binormal = (0,0,0)
  Mode = 0
  Profile = -> Sketch106
  Refine = true
  Spine = -> Pad008 [Edge208]
  SpineTangent = false
  Suppressed = false
  Transformation = 0
  Transition = 0
FEATURE [PartDesign::SubtractivePipe] SubtractivePipe001
  AuxilleryCurvelinear = true
  AuxillerySpineTangent = false
  BaseFeature = -> SubtractivePipe
  Binormal = (0,0,0)
  Mode = 0
  Profile = -> Sketch107
  Refine = true
  Spine = -> Pad008 [Edge206,Edge209,Edge197]
  SpineTangent = false
  Suppressed = false
  Transformation = 0
  Transition = 0
FEATURE [Sketcher::SketchObject] Sketch108
  ArcFitTolerance = 1e-06
  AttachmentOffset = pos=(0,0,-1.6) rot=(0,0,1;0rad)
  AttachmentSupport = -> [Pad008]
  ExternalGeometry = -> [Binder]
  FullyConstrained = true
  MakeInternals = false
  MapMode = 5
  Placement = pos=(0,2,4e-16) rot=(0,0.707107,0.707107;3.14159rad)
  sketch-geometry (14):
    g0: LineSegment StartX=192.176 StartY=-3.18451 StartZ=0 EndX=193.827 EndY=-6.72678 EndZ=0
    g1: LineSegment [constr] StartX=202.765 StartY=20.303 StartZ=0 EndX=181.223 EndY=20.303 EndZ=0
    g2: LineSegment [constr] StartX=181.223 StartY=20.303 StartZ=0 EndX=181.223 EndY=1.30297 EndZ=0
    g3: ArcOfCircle CenterX=181.223 CenterY=-12.6042 CenterZ=0 NormalX=0 NormalY=0 NormalZ=1 AngleXU=0 Radius=13.9072 StartAngle=0.436332 EndAngle=1.5708
    g4: ArcOfEllipse CenterX=181.223 CenterY=10.803 CenterZ=0 NormalX=0 NormalY=0 NormalZ=1 MajorRadius=14.4779 MinorRadius=9.5 AngleXU=0 StartAngle=1.5708 EndAngle=4.71239
    g5: LineSegment [constr] StartX=195.701 StartY=10.803 StartZ=0 EndX=166.745 EndY=10.803 EndZ=0
    g6: LineSegment [constr] StartX=181.223 StartY=20.303 StartZ=0 EndX=181.223 EndY=1.30297 EndZ=0
    g7: GeomPoint [constr] X=192.148 Y=10.803 Z=0
    g8: GeomPoint [constr] X=170.298 Y=10.803 Z=0
    g9: LineSegment StartX=181.223 StartY=20.303 StartZ=0 EndX=202.765 EndY=20.303 EndZ=0
    g10: ArcOfCircle CenterX=207.583 CenterY=4 CenterZ=0 NormalX=0 NormalY=0 NormalZ=1 AngleXU=0 Radius=17 StartAngle=1.85815 EndAngle=3.57792
    g11: LineSegment [constr] StartX=172.411 StartY=39.2 StartZ=0 EndX=192.176 EndY=-3.18451 EndZ=0
    g12: GeomPoint [constr] X=181.223 Y=1.30297 Z=0
    g13: GeomPoint [constr] X=181.223 Y=1.30297 Z=0
  constraints (28):
    c: Coincident(g1,g-7)
    c: Horizontal(g1)
    c: Coincident(g2,g1)
    c: Vertical(g2)
    c: Coincident(g3,g2)
    c: InternalAlignment(g5-g8 -> g4) x4
    c: Horizontal(g5)
    c: PointOnObject(g4,g2)
    c: Coincident(g4,g1)
    c: DistanceX(g-3,g5) = 19.1
    c: Coincident(g4,g2)
    c: Coincident(g9,g1)
    c: Coincident(g9,g1)
    c: Coincident(g10,g1)
    c: Coincident(g10,g0)
    c: PointOnObject(g11,g-6)
    c: PointOnObject(g1,g11)
    c: DistanceY(g2,g1) = 19
    c: Coincident(g10,g-4)
    c: PointOnObject(g12,g4)
    c: PointOnObject(g12,g3)
    c: Tangent(g11,g-5) = -1.5708
    c: Tangent(g0,g-5) = -1.5708
    c: Tangent(g3,g0) = 1.5708
    c: PointOnObject(g13,g4)
    c: PointOnObject(g13,g3)
    c: Tangent(g4,g3,g13) = 1.5708
    c: Horizontal(g11,g0)
FEATURE [Part::Part2DObjectPython] Clone2D  label="Sketch108 (2D)"  # Draft 2D object (typed FeaturePython)
  Fuse = false
  Objects = -> [Sketch108]
  Placement = pos=(0,2,4e-16) rot=(0,0.707107,0.707107;3.14159rad)
  Scale = (1,1,1)
FEATURE [Sketcher::SketchObject] Sketch109
  ArcFitTolerance = 1e-06
  AttachmentOffset = pos=(0,0,-3.8) rot=(0,0,1;0rad)
  AttachmentSupport = -> [Pad008]
  ExternalGeometry = -> [Binder]
  FullyConstrained = true
  MakeInternals = false
  MapMode = 5
  Placement = pos=(0,-0.2,8e-16) rot=(0,0.707107,0.707107;3.14159rad)
  sketch-geometry (1):
    g0: GeomPoint X=197.47 Y=8.55923 Z=0
  constraints (1):
    c: Symmetric(g-7,g-5,g0)
FEATURE [PartDesign::SubtractiveLoft] SubtractiveLoft
  BaseFeature = -> SubtractivePipe001
  Closed = false
  Profile = -> Sketch099
  Refine = true
  Ruled = false
  Sections = -> [Sketch108]
  Suppressed = false
FEATURE [PartDesign::SubtractiveLoft] SubtractiveLoft001
  BaseFeature = -> SubtractiveLoft
  Closed = false
  Profile = -> Clone2D
  Refine = true
  Ruled = false
  Sections = -> [Sketch109]
  Suppressed = false
FEATURE [PartDesign::Chamfer] Chamfer001
  Angle = 45
  Base = -> SubtractiveLoft001 [Edge122,Edge121,Edge118,Edge116,Edge114,Edge113,Edge170,Edge80,Edge76]
  BaseFeature = -> SubtractiveLoft001
  ChamferType = 0
  FlipDirection = false
  Refine = true
  Size = 1.9
  Size2 = 1
  SupportTransform = false
  Suppressed = false
  UseAllEdges = false
FEATURE [PartDesign::Chamfer] Chamfer002
  Angle = 45
  Base = -> Chamfer001 [Edge95,Edge34]
  BaseFeature = -> Chamfer001
  ChamferType = 0
  FlipDirection = false
  Refine = true
  Size = 3.5
  Size2 = 1
  SupportTransform = false
  Suppressed = false
  UseAllEdges = false
FEATURE [PartDesign::Chamfer] Chamfer003
  Angle = 45
  Base = -> Chamfer002 [Edge85]
  BaseFeature = -> Chamfer002
  ChamferType = 0
  FlipDirection = false
  Refine = true
  Size = 1.5
  Size2 = 1
  SupportTransform = false
  Suppressed = false
  UseAllEdges = false
FEATURE [PartDesign::Chamfer] Chamfer004
  Angle = 45
  Base = -> Chamfer003 [Edge18,Edge19,Edge17,Edge20]
  BaseFeature = -> Chamfer003
  ChamferType = 0
  FlipDirection = false
  Refine = true
  Size = 1.5
  Size2 = 1
  SupportTransform = false
  Suppressed = false
  UseAllEdges = false
FEATURE [PartDesign::Chamfer] Chamfer005
  Angle = 45
  Base = -> Chamfer004 [Edge227,Edge224]
  BaseFeature = -> Chamfer004
  ChamferType = 1
  FlipDirection = false
  Refine = true
  Size = 1.5
  Size2 = 2.8
  SupportTransform = false
  Suppressed = false
  UseAllEdges = false
FEATURE [PartDesign::Chamfer] Chamfer006
  Angle = 45
  Base = -> Chamfer005 [Edge223]
  BaseFeature = -> Chamfer005
  ChamferType = 1
  FlipDirection = false
  Refine = true
  Size = 6
  Size2 = 1
  SupportTransform = false
  Suppressed = false
  UseAllEdges = false
FEATURE [PartDesign::Fillet] Fillet002
  Base = -> Chamfer006 [Edge150]
  BaseFeature = -> Chamfer006
  Radius = 1.9
  Refine = true
  SupportTransform = false
  Suppressed = false
  UseAllEdges = false
FEATURE [PartDesign::Fillet] Fillet003
  Base = -> Fillet002 [Edge6]
  BaseFeature = -> Fillet002
  Radius = 1.1
  Refine = true
  SupportTransform = false
  Suppressed = false
  UseAllEdges = false
FEATURE [PartDesign::Fillet] Fillet004
  Base = -> Fillet003 [Edge45]
  BaseFeature = -> Fillet003
  Radius = 1.9
  Refine = true
  SupportTransform = false
  Suppressed = false
  UseAllEdges = false
FEATURE [PartDesign::Fillet] Fillet005
  Base = -> Fillet004 [Edge1]
  BaseFeature = -> Fillet004
  Radius = 1
  Refine = true
  SupportTransform = false
  Suppressed = false
  UseAllEdges = false
FEATURE [PartDesign::Chamfer] Chamfer007
  Angle = 45
  Base = -> Fillet005 [Edge29]
  BaseFeature = -> Fillet005
  ChamferType = 0
  FlipDirection = false
  Refine = true
  Size = 1.9
  Size2 = 1
  SupportTransform = false
  Suppressed = false
  UseAllEdges = false
FEATURE [PartDesign::Fillet] Fillet006
  Base = -> Chamfer007 [Edge339,Edge338]
  BaseFeature = -> Chamfer007
  Radius = 5
  Refine = true
  SupportTransform = false
  Suppressed = false
  UseAllEdges = false
FEATURE [Sketcher::SketchObject] Sketch110
  ArcFitTolerance = 1e-06
  AttachmentSupport = -> [Pad010]
  ExternalGeometry = -> [Sketch098]
  FullyConstrained = true
  MakeInternals = false
  MapMode = 5
  Placement = pos=(0,4,-9e-16) rot=(0,0.707107,0.707107;3.14159rad)
  sketch-geometry (8):
    g0: LineSegment StartX=119.69 StartY=34 StartZ=0 EndX=130.69 EndY=34 EndZ=0
    g1: LineSegment StartX=119.95 StartY=33.2 StartZ=0 EndX=130.95 EndY=33.2 EndZ=0
    g2: LineSegment StartX=119.137 StartY=35.7 StartZ=0 EndX=130.137 EndY=35.7 EndZ=0
    g3: LineSegment StartX=118.877 StartY=36.5 StartZ=0 EndX=129.877 EndY=36.5 EndZ=0
    g4: LineSegment StartX=118.877 StartY=36.5 StartZ=0 EndX=119.137 EndY=35.7 EndZ=0
    g5: LineSegment StartX=129.877 StartY=36.5 StartZ=0 EndX=130.137 EndY=35.7 EndZ=0
    g6: LineSegment StartX=119.69 StartY=34 StartZ=0 EndX=119.95 EndY=33.2 EndZ=0
    g7: LineSegment StartX=130.69 StartY=34 StartZ=0 EndX=130.95 EndY=33.2 EndZ=0
  constraints (24):
    c: Horizontal(g0)
    c: Horizontal(g1)
    c: Horizontal(g2)
    c: Horizontal(g3)
    c: Equal(g1,g-5)
    c: Equal(g0,g-5)
    c: Equal(g2,g-5)
    c: Equal(g3,g-5)
    c: PointOnObject(g0,g-3)
    c: PointOnObject(g1,g-3)
    c: PointOnObject(g2,g-3)
    c: PointOnObject(g3,g-3)
    c: Coincident(g4,g3)
    c: Coincident(g4,g2)
    c: Coincident(g5,g3)
    c: Coincident(g5,g2)
    c: Coincident(g6,g0)
    c: Coincident(g6,g1)
    c: Coincident(g7,g0)
    c: Coincident(g7,g1)
    c: DistanceY(g1,g0) = 0.8
    c: DistanceY(g2,g3) = 0.8
    c: DistanceY(g-5,g1) = 2
    c: DistanceY(g-5,g2) = 4.5
FEATURE [PartDesign::Pocket] Pocket003
  BaseFeature = -> Fillet006
  Direction = (0,-1,2e-16)
  Length = 1
  Length2 = 5
  Profile = -> Sketch110
  ReferenceAxis = -> Sketch110 [N_Axis]
  Refine = true
  Suppressed = false
  Type = 0
FEATURE [Sketcher::SketchObject] Sketch111
  ArcFitTolerance = 1e-06
  AttachmentSupport = -> [Pad009]
  ExternalGeometry = -> [Pad009]
  FullyConstrained = true
  MakeInternals = false
  MapMode = 5
  Placement = pos=(0,3.6,-8e-16) rot=(0,0.707107,0.707107;3.14159rad)
  sketch-geometry (21):
    g0: LineSegment [constr] StartX=97 StartY=36.8 StartZ=0 EndX=97 EndY=26.8 EndZ=0
    g1: LineSegment StartX=97 StartY=28.6 StartZ=0 EndX=97 EndY=27.8 EndZ=0
    g2: LineSegment StartX=97 StartY=27.8 StartZ=0 EndX=108 EndY=27.8 EndZ=0
    g3: LineSegment StartX=108 StartY=27.8 StartZ=0 EndX=108 EndY=28.6 EndZ=0
    g4: LineSegment StartX=108 StartY=28.6 StartZ=0 EndX=97 EndY=28.6 EndZ=0
    g5: LineSegment StartX=97 StartY=35.8 StartZ=0 EndX=97 EndY=35 EndZ=0
    g6: LineSegment StartX=97 StartY=35 StartZ=0 EndX=108 EndY=35 EndZ=0
    g7: LineSegment StartX=108 StartY=35 StartZ=0 EndX=108 EndY=35.8 EndZ=0
    g8: LineSegment StartX=108 StartY=35.8 StartZ=0 EndX=97 EndY=35.8 EndZ=0
    g9: LineSegment StartX=97 StartY=30.4 StartZ=0 EndX=97 EndY=29.6 EndZ=0
    g10: LineSegment StartX=97 StartY=29.6 StartZ=0 EndX=108 EndY=29.6 EndZ=0
    g11: LineSegment StartX=108 StartY=29.6 StartZ=0 EndX=108 EndY=30.4 EndZ=0
    g12: LineSegment StartX=108 StartY=30.4 StartZ=0 EndX=97 EndY=30.4 EndZ=0
    g13: LineSegment StartX=97 StartY=34 StartZ=0 EndX=97 EndY=33.2 EndZ=0
    g14: LineSegment StartX=97 StartY=33.2 StartZ=0 EndX=108 EndY=33.2 EndZ=0
    g15: LineSegment StartX=108 StartY=33.2 StartZ=0 EndX=108 EndY=34 EndZ=0
    g16: LineSegment StartX=108 StartY=34 StartZ=0 EndX=97 EndY=34 EndZ=0
    g17: LineSegment StartX=97 StartY=32.2 StartZ=0 EndX=97 EndY=31.4 EndZ=0
    g18: LineSegment StartX=97 StartY=31.4 StartZ=0 EndX=108 EndY=31.4 EndZ=0
    g19: LineSegment StartX=108 StartY=31.4 StartZ=0 EndX=108 EndY=32.2 EndZ=0
    g20: LineSegment StartX=108 StartY=32.2 StartZ=0 EndX=97 EndY=32.2 EndZ=0
  constraints (54):
    c: Vertical(g0)
    c: PointOnObject(g0,g-3)
    c: PointOnObject(g0,g-4)
    c: DistanceX(g0,g-5) = 11
    c: Coincident(g1,g2)
    c: Coincident(g2,g3)
    c: Coincident(g3,g4)
    c: Coincident(g4,g1)
    c: Horizontal(g2)
    c: Horizontal(g4)
    c: Tangent(g1,g0)
    c: Tangent(g3,g-5)
    c: DistanceY(g2,g3) = 0.8
    c: Coincident(g5,g6)
    c: Coincident(g6,g7)
    c: Coincident(g7,g8)
    c: Coincident(g8,g5)
    c: Horizontal(g6)
    c: Horizontal(g8)
    c: DistanceY(g6,g7) = 0.8
    c: Coincident(g9,g10)
    c: Coincident(g10,g11)
    c: Coincident(g11,g12)
    c: Coincident(g12,g9)
    c: Horizontal(g10)
    c: Horizontal(g12)
    c: DistanceY(g10,g11) = 0.8
    c: Tangent(g5,g0)
    c: Tangent(g7,g-5)
    c: Tangent(g9,g0)
    c: Tangent(g11,g-5)
    c: Coincident(g13,g14)
    c: Coincident(g14,g15)
    c: Coincident(g15,g16)
    c: Coincident(g16,g13)
    c: Horizontal(g14)
    c: Horizontal(g16)
    c: DistanceY(g14,g15) = 0.8
    c: Tangent(g13,g0)
    c: Tangent(g15,g-5)
    c: Coincident(g17,g18)
    c: Coincident(g18,g19)
    c: Coincident(g19,g20)
    c: Coincident(g20,g17)
    c: Horizontal(g18)
    c: Horizontal(g20)
    c: DistanceY(g18,g19) = 0.8
    c: Tangent(g17,g0)
    c: Tangent(g19,g-5)
    c: DistanceY(g1,g9) = 1
    c: DistanceY(g9,g17) = 1
    c: DistanceY(g17,g13) = 1
    c: DistanceY(g13,g5) = 1
    c: DistanceY(g0,g1) = 1
FEATURE [PartDesign::Pocket] Pocket004
  BaseFeature = -> Pocket003
  Direction = (0,-1,2e-16)
  Length = 1
  Length2 = 5
  Profile = -> Sketch111
  ReferenceAxis = -> Sketch111 [N_Axis]
  Refine = true
  Suppressed = false
  Type = 0
FEATURE [Sketcher::SketchObject] Sketch112
  ArcFitTolerance = 1e-06
  AttachmentSupport = -> [Pad008]
  ExternalGeometry = -> [Binder]
  FullyConstrained = true
  MakeInternals = false
  MapMode = 5
  Placement = pos=(0,3.6,0) rot=(0,0.707107,0.707107;3.14159rad)
  sketch-geometry (4):
    g0: LineSegment [constr] StartX=167.782 StartY=-53.0314 StartZ=0 EndX=215.42 EndY=-53.0314 EndZ=0
    g1: GeomPoint [constr] X=191.282 Y=-53.0314 Z=0
    g2: Circle CenterX=191.282 CenterY=-53.0314 CenterZ=0 NormalX=0 NormalY=0 NormalZ=1 AngleXU=0 Radius=11.5
    g3: Circle CenterX=191.282 CenterY=-53.0314 CenterZ=0 NormalX=0 NormalY=0 NormalZ=1 AngleXU=0 Radius=10.7
  constraints (9):
    c: Horizontal(g0)
    c: PointOnObject(g0,g-3)
    c: Diameter(g2) = 23
    c: Coincident(g2,g1)
    c: Diameter(g3) = 21.4
    c: Coincident(g3,g1)
    c: DistanceX(g0,g1) = 23.5
    c: PointOnObject(g1,g0)
    c: Coincident(g0,g-4)
FEATURE [PartDesign::Pocket] Pocket005
  BaseFeature = -> Pocket004
  Direction = (0,-1,2e-16)
  Length = 0.8
  Length2 = 5
  Profile = -> Sketch112
  ReferenceAxis = -> Sketch112 [N_Axis]
  Refine = true
  Suppressed = false
  Type = 0
FEATURE [Part::Mirroring] Part__Mirroring  label="Pocket005 (Mirror #1)"
  Base = (0,0,0)
  Normal = (0,0,1)
  Source = -> Pocket005
FEATURE [Sketcher::SketchObject] Sketch113
  ArcFitTolerance = 1e-06
  AttachmentSupport = -> [Pocket005]
  FullyConstrained = true
  MakeInternals = false
  MapMode = 5
  Placement = pos=(0,3.6,0) rot=(0,0.707107,0.707107;3.14159rad)
FEATURE [PartDesign::Body] Body006  label="lato SX"
  AllowCompound = false
  Group = -> [Binder,Pad004,Sketch091,Pad005,Sketch092,Pocket001,Sketch093,Pocket002,Sketch094,Pad006,Sketch095,Pad007,Sketch096,Pad008,Sketch097,Pad009,Sketch098,Pad010,SubtractivePipe,SubtractivePipe001,Sketch099,Sketch106,Sketch107,Sketch108,Clone2D,Sketch109,SubtractiveLoft,SubtractiveLoft001,Chamfer001,Chamfer002,Chamfer003,Chamfer004,Chamfer005,Chamfer006,Fillet002,Fillet003,Fillet004,Fillet005,+9 more]
  Origin = -> Origin006
  Tip = -> Pocket005
FEATURE [Mesh::Feature] logo_per_PCB_definitivo_positivo
  Placement = pos=(-191,17,-66) rot=(0,1,1;0rad)
FEATURE [Sketcher::SketchObject] Sketch114  label="Sketch114 - base lato DX"
  ArcFitTolerance = 1e-06
  AttachmentSupport = -> [Binder001]
  ExternalGeometry = -> [Binder001]
  FullyConstrained = true
  MakeInternals = false
  MapMode = 5
  Placement = pos=(0,1e-15,0) rot=(0,0.707107,0.707107;3.14159rad)
  sketch-geometry (28):
    g0: Circle CenterX=5.6 CenterY=34.8 CenterZ=0 NormalX=0 NormalY=0 NormalZ=1 AngleXU=0 Radius=1.8
    g1: Circle CenterX=5.6 CenterY=7.6 CenterZ=0 NormalX=0 NormalY=0 NormalZ=1 AngleXU=0 Radius=1.8
    g2: Circle CenterX=24.2 CenterY=26.7 CenterZ=0 NormalX=0 NormalY=0 NormalZ=1 AngleXU=0 Radius=3
    g3: Circle CenterX=24.2 CenterY=15.7 CenterZ=0 NormalX=0 NormalY=0 NormalZ=1 AngleXU=0 Radius=3
    g4: Circle CenterX=36.2 CenterY=21.2 CenterZ=0 NormalX=0 NormalY=0 NormalZ=1 AngleXU=0 Radius=2.8
    g5: Circle CenterX=78.51 CenterY=34.8 CenterZ=0 NormalX=0 NormalY=0 NormalZ=1 AngleXU=0 Radius=1.8
    g6: Circle CenterX=78.51 CenterY=7.6 CenterZ=0 NormalX=0 NormalY=0 NormalZ=1 AngleXU=0 Radius=1.8
    g7: Circle CenterX=184.08 CenterY=34.8 CenterZ=0 NormalX=0 NormalY=0 NormalZ=1 AngleXU=0 Radius=1.8
    g8: Circle CenterX=213.443 CenterY=-76.8316 CenterZ=0 NormalX=0 NormalY=0 NormalZ=1 AngleXU=0 Radius=1.8
    g9: Circle CenterX=179.305 CenterY=-76.8316 CenterZ=0 NormalX=0 NormalY=0 NormalZ=1 AngleXU=0 Radius=1.8
    g10: ArcOfCircle CenterX=132.428 CenterY=4 CenterZ=0 NormalX=0 NormalY=0 NormalZ=1 AngleXU=0 Radius=16 StartAngle=0.314159 EndAngle=1.5708
    g11: ArcOfCircle CenterX=107.6 CenterY=4 CenterZ=0 NormalX=0 NormalY=0 NormalZ=1 AngleXU=0 Radius=16 StartAngle=1.5708 EndAngle=3.00366
    g12: ArcOfCircle CenterX=207.583 CenterY=4 CenterZ=0 NormalX=0 NormalY=0 NormalZ=1 AngleXU=0 Radius=17 StartAngle=1.85815 EndAngle=3.57792
    g13: ArcOfCircle CenterX=184.801 CenterY=-67.3089 CenterZ=0 NormalX=0 NormalY=0 NormalZ=1 AngleXU=0 Radius=33.7833 StartAngle=5.88425 EndAngle=6.71952
    g14: LineSegment StartX=0 StartY=39.2 StartZ=0 EndX=0 EndY=3.2 EndZ=0
    g15: LineSegment StartX=0 StartY=3.2 StartZ=0 EndX=82.8 EndY=3.2 EndZ=0
    g16: LineSegment StartX=82.8 StartY=3.2 StartZ=0 EndX=82.8 EndY=6.2 EndZ=0
    g17: LineSegment StartX=82.8 StartY=6.2 StartZ=0 EndX=91.752 EndY=6.2 EndZ=0
    g18: LineSegment StartX=107.6 StartY=20 StartZ=0 EndX=132.428 EndY=20 EndZ=0
    g19: LineSegment StartX=147.645 StartY=8.94427 StartZ=0 EndX=176.685 EndY=-80.4316 EndZ=0
    g20: LineSegment StartX=176.685 StartY=-80.4316 StartZ=0 EndX=215.932 EndY=-80.4316 EndZ=0
    g21: LineSegment StartX=215.42 StartY=-53.0314 StartZ=0 EndX=192.176 EndY=-3.18451 EndZ=0
    g22: LineSegment StartX=202.765 StartY=20.303 StartZ=0 EndX=195.887 EndY=39.2 EndZ=0
    g23: LineSegment StartX=195.887 StartY=39.2 StartZ=0 EndX=0 EndY=39.2 EndZ=0
    g24: LineSegment StartX=196.467 StartY=26.4942 StartZ=0 EndX=194.073 EndY=33.0721 EndZ=0
    g25: LineSegment StartX=194.073 StartY=33.0721 StartZ=0 EndX=189.939 EndY=31.5672 EndZ=0
    g26: LineSegment StartX=189.939 StartY=31.5672 StartZ=0 EndX=192.333 EndY=24.9893 EndZ=0
    g27: LineSegment StartX=192.333 StartY=24.9893 StartZ=0 EndX=196.467 EndY=26.4942 EndZ=0
  constraints (60):
    c: Equal(g0,g-25)
    c: Equal(g2,g-29)
    c: Equal(g3,g-30)
    c: Equal(g4,g-28)
    c: Equal(g1,g-26)
    c: Coincident(g0,g-25)
    c: Coincident(g1,g-26)
    c: Coincident(g2,g-29)
    c: Coincident(g3,g-30)
    c: Coincident(g4,g-28)
    c: Equal(g5,g-23)
    c: Equal(g6,g-24)
    c: Coincident(g5,g-23)
    c: Coincident(g6,g-24)
    c: Equal(g7,g-20)
    c: Coincident(g7,g-20)
    c: Equal(g9,g-22)
    c: Coincident(g9,g-22)
    c: Equal(g8,g-21)
    c: Coincident(g8,g-21)
    c: Equal(g13,g-12)
    c: Equal(g12,g-14)
    c: Equal(g10,g-9)
    c: Equal(g11,g-7)
    c: Coincident(g14,g-27)
    c: Coincident(g14,g-27)
    c: Coincident(g15,g14)
    c: Coincident(g15,g-5)
    c: Coincident(g16,g15)
    c: Coincident(g16,g-6)
    c: Coincident(g17,g16)
    c: Coincident(g17,g-7)
    c: Coincident(g11,g17)
    c: Coincident(g11,g-8)
    c: Coincident(g18,g11)
    c: Coincident(g18,g-9)
    c: Coincident(g10,g18)
    c: Coincident(g10,g-10)
    c: Coincident(g19,g10)
    c: Coincident(g19,g-11)
    c: Coincident(g20,g19)
    c: Coincident(g20,g-12)
    c: Coincident(g13,g20)
    c: Coincident(g13,g-13)
    c: Coincident(g21,g13)
    c: Coincident(g21,g-14)
    c: Coincident(g12,g21)
    c: Coincident(g12,g-15)
    c: Coincident(g22,g12)
    c: Coincident(g22,g-15)
    c: Coincident(g23,g22)
    c: Coincident(g23,g14)
    c: Coincident(g24,g-18)
    c: Coincident(g24,g-16)
    c: Coincident(g25,g24)
    c: Coincident(g25,g-19)
    c: Coincident(g26,g25)
    c: Coincident(g26,g-19)
    c: Coincident(g27,g26)
    c: Coincident(g27,g24)
FEATURE [PartDesign::Pad] Pad011
  Direction = (0,1,-2e-16)
  Length = 2
  Length2 = 10
  Profile = -> Sketch114
  ReferenceAxis = -> Sketch114 [N_Axis]
  Refine = true
  Reversed = true
  Suppressed = false
  Type = 0
FEATURE [Sketcher::SketchObject] Sketch115
  ArcFitTolerance = 1e-06
  AttachmentSupport = -> [Pad011]
  ExternalGeometry = -> [Binder001]
  FullyConstrained = true
  MakeInternals = false
  MapMode = 5
  Placement = pos=(0,1.1e-15,0) rot=(0,0.707107,0.707107;3.14159rad)
  sketch-geometry (4):
    g0: ArcOfCircle CenterX=24.2 CenterY=26.7 CenterZ=0 NormalX=0 NormalY=0 NormalZ=1 AngleXU=0 Radius=3 StartAngle=4.48384e-08 EndAngle=3.14159
    g1: ArcOfCircle CenterX=24.2 CenterY=15.7 CenterZ=0 NormalX=0 NormalY=0 NormalZ=1 AngleXU=0 Radius=3 StartAngle=3.14159 EndAngle=6.28318
    g2: LineSegment StartX=21.2 StartY=26.7 StartZ=0 EndX=21.2 EndY=15.7 EndZ=0
    g3: LineSegment StartX=27.2 StartY=26.7 StartZ=0 EndX=27.2 EndY=15.7 EndZ=0
  constraints (12):
    c: Equal(g1,g-4)
    c: Equal(g0,g-3)
    c: Coincident(g0,g-3)
    c: Coincident(g1,g-4)
    c: Vertical(g2)
    c: Vertical(g3)
    c: Tangent(g3,g-3)
    c: Tangent(g2,g-3)
    c: Coincident(g0,g2)
    c: Coincident(g0,g3)
    c: Coincident(g1,g2)
    c: Coincident(g3,g1)
FEATURE [PartDesign::Pocket] Pocket006
  BaseFeature = -> Pad011
  Direction = (0,-1,2e-16)
  Length = 1.2
  Length2 = 5
  Profile = -> Sketch115
  ReferenceAxis = -> Sketch115 [N_Axis]
  Refine = true
  Suppressed = false
  Type = 0
FEATURE [Sketcher::SketchObject] Sketch116
  ArcFitTolerance = 1e-06
  AttachmentSupport = -> [Pocket006]
  ExternalGeometry = -> [Binder001]
  FullyConstrained = true
  MakeInternals = false
  MapMode = 5
  Placement = pos=(0,1.1e-15,0) rot=(0,0.707107,0.707107;3.14159rad)
  sketch-geometry (4):
    g0: Circle CenterX=43.2 CenterY=30.3 CenterZ=0 NormalX=0 NormalY=0 NormalZ=1 AngleXU=0 Radius=3.4
    g1: Circle CenterX=43.2 CenterY=12.1 CenterZ=0 NormalX=0 NormalY=0 NormalZ=1 AngleXU=0 Radius=3.4
    g2: Circle CenterX=18.6 CenterY=30.3 CenterZ=0 NormalX=0 NormalY=0 NormalZ=1 AngleXU=0 Radius=3.4
    g3: Circle CenterX=18.6 CenterY=12.1 CenterZ=0 NormalX=0 NormalY=0 NormalZ=1 AngleXU=0 Radius=3.4
  constraints (8):
    c: Diameter(g0) = 6.8
    c: Diameter(g1) = 6.8
    c: Diameter(g2) = 6.8
    c: Diameter(g3) = 6.8
    c: Coincident(g2,g-3)
    c: Coincident(g0,g-4)
    c: Coincident(g3,g-6)
    c: Coincident(g1,g-5)
FEATURE [PartDesign::Pad] Pad012
  BaseFeature = -> Pocket006
  Direction = (0,1,-2e-16)
  Length = 2.4
  Length2 = 10
  Profile = -> Sketch116
  ReferenceAxis = -> Sketch116 [N_Axis]
  Refine = true
  Suppressed = false
  Type = 0
FEATURE [Sketcher::SketchObject] Sketch117
  ArcFitTolerance = 1e-06
  AttachmentSupport = -> [Pad011]
  ExternalGeometry = -> [Binder001]
  FullyConstrained = true
  MakeInternals = false
  MapMode = 5
  Placement = pos=(0,1.1e-15,0) rot=(0,0.707107,0.707107;3.14159rad)
  sketch-geometry (4):
    g0: Circle CenterX=43.2 CenterY=30.3 CenterZ=0 NormalX=0 NormalY=0 NormalZ=1 AngleXU=0 Radius=2.25
    g1: Circle CenterX=43.2 CenterY=12.1 CenterZ=0 NormalX=0 NormalY=0 NormalZ=1 AngleXU=0 Radius=2.25
    g2: Circle CenterX=18.6 CenterY=30.3 CenterZ=0 NormalX=0 NormalY=0 NormalZ=1 AngleXU=0 Radius=2.25
    g3: Circle CenterX=18.6 CenterY=12.1 CenterZ=0 NormalX=0 NormalY=0 NormalZ=1 AngleXU=0 Radius=2.25
  constraints (8):
    c: Diameter(g0) = 4.5
    c: Diameter(g1) = 4.5
    c: Diameter(g2) = 4.5
    c: Diameter(g3) = 4.5
    c: Coincident(g2,g-3)
    c: Coincident(g3,g-6)
    c: Coincident(g0,g-4)
    c: Coincident(g1,g-5)
FEATURE [PartDesign::Pocket] Pocket007
  BaseFeature = -> Pad012
  Direction = (0,-1,2e-16)
  Length = 0.6
  Length2 = 2.4
  Profile = -> Sketch117
  ReferenceAxis = -> Sketch117 [N_Axis]
  Refine = true
  Suppressed = false
  Type = 4
FEATURE [Sketcher::SketchObject] Sketch118
  ArcFitTolerance = 1e-06
  AttachmentSupport = -> [Pad011]
  ExternalGeometry = -> [Binder001]
  FullyConstrained = true
  MakeInternals = false
  MapMode = 5
  Placement = pos=(0,-2,4e-16) rot=(1,0,0;1.5708rad)
  sketch-geometry (12):
    g0: Circle CenterX=-78.51 CenterY=34.8 CenterZ=0 NormalX=0 NormalY=0 NormalZ=1 AngleXU=0 Radius=1.8
    g1: Circle CenterX=-78.51 CenterY=7.6 CenterZ=0 NormalX=0 NormalY=0 NormalZ=1 AngleXU=0 Radius=1.8
    g2: Circle CenterX=-5.6 CenterY=34.8 CenterZ=0 NormalX=0 NormalY=0 NormalZ=1 AngleXU=0 Radius=1.8
    g3: Circle CenterX=-5.6 CenterY=7.6 CenterZ=0 NormalX=0 NormalY=0 NormalZ=1 AngleXU=0 Radius=1.8
    g4: LineSegment StartX=0 StartY=39.2 StartZ=0 EndX=0 EndY=3.2 EndZ=0
    g5: LineSegment StartX=0 StartY=3.2 StartZ=0 EndX=-82.8 EndY=3.2 EndZ=0
    g6: LineSegment StartX=-82.8 StartY=3.2 StartZ=0 EndX=-82.8 EndY=39.2 EndZ=0
    g7: LineSegment StartX=-82.8 StartY=39.2 StartZ=0 EndX=0 EndY=39.2 EndZ=0
    g8: ArcOfCircle CenterX=-65 CenterY=21.2 CenterZ=0 NormalX=0 NormalY=0 NormalZ=1 AngleXU=0 Radius=10 StartAngle=1.5708 EndAngle=4.71239
    g9: ArcOfCircle CenterX=-19 CenterY=21.2 CenterZ=0 NormalX=0 NormalY=0 NormalZ=1 AngleXU=0 Radius=10 StartAngle=4.71239 EndAngle=7.85398
    g10: LineSegment StartX=-65 StartY=31.2 StartZ=0 EndX=-19 EndY=31.2 EndZ=0
    g11: LineSegment StartX=-65 StartY=11.2 StartZ=0 EndX=-19 EndY=11.2 EndZ=0
  constraints (25):
    c: Equal(g2,g-5)
    c: Equal(g3,g-7)
    c: Equal(g1,g-6)
    c: Equal(g0,g-4)
    c: Coincident(g0,g-4)
    c: Coincident(g1,g-6)
    c: Coincident(g3,g-7)
    c: Coincident(g2,g-5)
    c: Coincident(g4,g-8)
    c: Coincident(g4,g-9)
    c: Coincident(g5,g4)
    c: Coincident(g5,g-10)
    c: Coincident(g6,g5)
    c: PointOnObject(g6,g-3)
    c: Vertical(g6)
    c: Coincident(g7,g6)
    c: Coincident(g7,g4)
    c: Tangent(g8,g10) = 1.5708
    c: Tangent(g8,g11) = -1.5708
    c: Tangent(g9,g10) = 1.5708
    c: Tangent(g9,g11) = -1.5708
    c: Equal(g8,g9)
    c: Radius(g8) = 10
    c: Coincident(g8,g-11)
    c: Coincident(g9,g-12)
FEATURE [PartDesign::Pad] Pad013
  BaseFeature = -> Pocket007
  Direction = (0,-1,2e-16)
  Length = 1.6
  Length2 = 10
  Profile = -> Sketch118
  ReferenceAxis = -> Sketch118 [N_Axis]
  Refine = true
  Suppressed = false
  Type = 0
FEATURE [Sketcher::SketchObject] Sketch119
  ArcFitTolerance = 1e-06
  AttachmentSupport = -> [Pad013]
  ExternalGeometry = -> [Binder001]
  FullyConstrained = true
  MakeInternals = false
  MapMode = 5
  Placement = pos=(0,-3.6,0) rot=(1,0,0;1.5708rad)
  sketch-geometry (21):
    g0: LineSegment [constr] StartX=-82.8 StartY=3.2 StartZ=0 EndX=-82.8 EndY=39.2 EndZ=0
    g1: ArcOfCircle CenterX=-78.51 CenterY=34.8 CenterZ=0 NormalX=0 NormalY=0 NormalZ=1 AngleXU=0 Radius=3.5 StartAngle=4.71239 EndAngle=6.28319
    g2: ArcOfCircle CenterX=-78.51 CenterY=7.6 CenterZ=0 NormalX=0 NormalY=0 NormalZ=1 AngleXU=0 Radius=3.5 StartAngle=0 EndAngle=1.5708
    g3: ArcOfCircle CenterX=-5.6 CenterY=34.8 CenterZ=0 NormalX=0 NormalY=0 NormalZ=1 AngleXU=0 Radius=3.5 StartAngle=3.14159 EndAngle=4.71239
    g4: ArcOfCircle CenterX=-5.6 CenterY=7.6 CenterZ=0 NormalX=0 NormalY=0 NormalZ=1 AngleXU=0 Radius=3.5 StartAngle=1.5708 EndAngle=3.14159
    g5: LineSegment StartX=0 StartY=39.2 StartZ=0 EndX=0 EndY=31.3 EndZ=0
    g6: LineSegment StartX=0 StartY=39.2 StartZ=0 EndX=-9.1 EndY=39.2 EndZ=0
    g7: LineSegment StartX=0 StartY=3.2 StartZ=0 EndX=0 EndY=11.1 EndZ=0
    g8: LineSegment StartX=0 StartY=3.2 StartZ=0 EndX=-9.1 EndY=3.2 EndZ=0
    g9: LineSegment StartX=-82.8 StartY=3.2 StartZ=0 EndX=-75.01 EndY=3.2 EndZ=0
    g10: LineSegment StartX=-82.8 StartY=3.2 StartZ=0 EndX=-82.8 EndY=11.1 EndZ=0
    g11: LineSegment StartX=-82.8 StartY=39.2 StartZ=0 EndX=-82.8 EndY=31.3 EndZ=0
    g12: LineSegment StartX=-82.8 StartY=39.2 StartZ=0 EndX=-75.01 EndY=39.2 EndZ=0
    g13: LineSegment StartX=-82.8 StartY=31.3 StartZ=0 EndX=-78.51 EndY=31.3 EndZ=0
    g14: LineSegment StartX=-75.01 StartY=39.2 StartZ=0 EndX=-75.01 EndY=34.8 EndZ=0
    g15: LineSegment StartX=-82.8 StartY=11.1 StartZ=0 EndX=-78.51 EndY=11.1 EndZ=0
    g16: LineSegment StartX=-75.01 StartY=3.2 StartZ=0 EndX=-75.01 EndY=7.6 EndZ=0
    g17: LineSegment StartX=-9.1 StartY=39.2 StartZ=0 EndX=-9.1 EndY=34.8 EndZ=0
    g18: LineSegment StartX=0 StartY=31.3 StartZ=0 EndX=-5.6 EndY=31.3 EndZ=0
    g19: LineSegment StartX=0 StartY=11.1 StartZ=0 EndX=-5.6 EndY=11.1 EndZ=0
    g20: LineSegment StartX=-9.1 StartY=3.2 StartZ=0 EndX=-9.1 EndY=7.6 EndZ=0
  constraints (51):
    c: Coincident(g0,g-10)
    c: PointOnObject(g0,g-8)
    c: Vertical(g0)
    c: Coincident(g1,g-3)
    c: Coincident(g2,g-4)
    c: Coincident(g3,g-5)
    c: Coincident(g4,g-6)
    c: Radius(g4) = 3.5
    c: Radius(g3) = 3.5
    c: Radius(g1) = 3.5
    c: Radius(g2) = 3.5
    c: Coincident(g5,g-9)
    c: PointOnObject(g5,g-9)
    c: Coincident(g6,g5)
    c: PointOnObject(g6,g-8)
    c: Coincident(g7,g-9)
    c: PointOnObject(g7,g-9)
    c: Coincident(g8,g7)
    c: PointOnObject(g8,g-7)
    c: Coincident(g9,g0)
    c: PointOnObject(g9,g-7)
    c: Coincident(g10,g0)
    c: PointOnObject(g10,g0)
    c: Coincident(g11,g0)
    c: PointOnObject(g11,g0)
    c: Coincident(g12,g0)
    c: PointOnObject(g12,g-8)
    c: Coincident(g13,g11)
    c: Horizontal(g13)
    c: Coincident(g14,g12)
    c: Vertical(g14)
    c: Coincident(g15,g10)
    c: Horizontal(g15)
    c: Coincident(g16,g9)
    c: Vertical(g16)
    c: Coincident(g17,g6)
    c: Vertical(g17)
    c: Coincident(g18,g5)
    c: Horizontal(g18)
    c: Coincident(g19,g7)
    c: Horizontal(g19)
    c: Coincident(g20,g8)
    c: Vertical(g20)
    c: Tangent(g20,g4) = 1.5708
    c: Tangent(g4,g19) = -1.5708
    c: Tangent(g18,g3) = 1.5708
    c: Tangent(g3,g17) = -1.5708
    c: Tangent(g13,g1) = -1.5708
    c: Tangent(g1,g14) = 1.5708
    c: Tangent(g16,g2) = -1.5708
    c: Tangent(g2,g15) = 1.5708
FEATURE [PartDesign::Pocket] Pocket008
  BaseFeature = -> Pad013
  Direction = (0,1,-2e-16)
  Length = 1.6
  Length2 = 5
  Profile = -> Sketch119
  ReferenceAxis = -> Sketch119 [N_Axis]
  Refine = true
  Suppressed = false
  Type = 0
FEATURE [Sketcher::SketchObject] Sketch120
  ArcFitTolerance = 1e-06
  AttachmentSupport = -> [Pad011]
  ExternalGeometry = -> [Binder001]
  FullyConstrained = true
  MakeInternals = false
  MapMode = 5
  Placement = pos=(0,-2,4e-16) rot=(1,0,0;1.5708rad)
  sketch-geometry (4):
    g0: LineSegment StartX=-137.815 StartY=39.2 StartZ=0 EndX=-142.655 EndY=24.303 EndZ=0
    g1: LineSegment StartX=-137.815 StartY=39.2 StartZ=0 EndX=-110.815 EndY=39.2 EndZ=0
    g2: LineSegment StartX=-142.655 StartY=24.303 StartZ=0 EndX=-110.815 EndY=24.303 EndZ=0
    g3: ArcOfCircle CenterX=-92.2534 CenterY=31.7515 CenterZ=0 NormalX=0 NormalY=0 NormalZ=1 AngleXU=0 Radius=20 StartAngle=2.75997 EndAngle=3.52321
  constraints (12):
    c: PointOnObject(g0,g-3)
    c: Coincident(g1,g0)
    c: PointOnObject(g1,g-3)
    c: Coincident(g2,g0)
    c: Horizontal(g2)
    c: Tangent(g0,g-4)
    c: Vertical(g2,g1)
    c: DistanceX(g1,g1) = 27
    c: DistanceY(g-6,g0) = 4
    c: Radius(g3) = 20
    c: Coincident(g3,g1)
    c: Coincident(g3,g2)
FEATURE [Sketcher::SketchObject] Sketch121
  ArcFitTolerance = 1e-06
  AttachmentSupport = -> [Pad011]
  ExternalGeometry = -> [Binder001]
  FullyConstrained = true
  MakeInternals = false
  MapMode = 5
  Placement = pos=(0,-2,4e-16) rot=(1,0,0;1.5708rad)
  sketch-geometry (15):
    g0: LineSegment StartX=-137.815 StartY=39.2 StartZ=0 EndX=-143.955 EndY=20.303 EndZ=0
    g1: LineSegment StartX=-143.955 StartY=20.303 StartZ=0 EndX=-190.141 EndY=20.303 EndZ=0
    g2: LineSegment StartX=-190.141 StartY=20.303 StartZ=0 EndX=-186.139 EndY=31.3 EndZ=0
    g3: LineSegment StartX=-178.754 StartY=39.2 StartZ=0 EndX=-180.791 EndY=33.6029 EndZ=0
    g4: ArcOfCircle CenterX=-184.08 CenterY=34.8 CenterZ=0 NormalX=0 NormalY=0 NormalZ=1 AngleXU=0 Radius=3.5 StartAngle=4.71239 EndAngle=5.93412
    g5: LineSegment StartX=-184.08 StartY=31.3 StartZ=0 EndX=-186.139 EndY=31.3 EndZ=0
    g6: LineSegment StartX=-137.815 StartY=39.2 StartZ=0 EndX=-156.815 EndY=39.2 EndZ=0
    g7: LineSegment StartX=-168.815 StartY=39.2 StartZ=0 EndX=-178.754 EndY=39.2 EndZ=0
    g8: LineSegment StartX=-157.815 StartY=39.2 StartZ=0 EndX=-167.815 EndY=39.2 EndZ=0
    g9: LineSegment StartX=-168.815 StartY=31.2 StartZ=0 EndX=-156.815 EndY=31.2 EndZ=0
    g10: LineSegment StartX=-167.436 StartY=36.2 StartZ=0 EndX=-157.436 EndY=36.2 EndZ=0
    g11: ArcOfCircle CenterX=-176.411 CenterY=35.2 CenterZ=0 NormalX=0 NormalY=0 NormalZ=1 AngleXU=0 Radius=20 StartAngle=6.08183 EndAngle=6.48454
    g12: ArcOfCircle CenterX=-188.411 CenterY=35.2 CenterZ=0 NormalX=0 NormalY=0 NormalZ=1 AngleXU=0 Radius=20 StartAngle=6.08183 EndAngle=6.48454
    g13: ArcOfCircle CenterX=-177.411 CenterY=35.2 CenterZ=0 NormalX=0 NormalY=0 NormalZ=1 AngleXU=0 Radius=20 StartAngle=0.0500209 EndAngle=0.201358
    g14: ArcOfCircle CenterX=-187.411 CenterY=35.2 CenterZ=0 NormalX=0 NormalY=0 NormalZ=1 AngleXU=0 Radius=20 StartAngle=0.0500209 EndAngle=0.201358
  constraints (46):
    c: PointOnObject(g0,g-3)
    c: Tangent(g0,g-5)
    c: Coincident(g1,g0)
    c: Horizontal(g1)
    c: Coincident(g2,g1)
    c: PointOnObject(g3,g-3)
    c: Parallel(g3,g-6)
    c: Parallel(g2,g-6)
    c: Radius(g4) = 3.5
    c: Coincident(g4,g-7)
    c: Tangent(g3,g4) = 1.5708
    c: Horizontal(g5)
    c: Tangent(g5,g4) = 1.5708
    c: DistanceX(g-8,g5) = 3.8
    c: Coincident(g2,g5)
    c: Coincident(g6,g0)
    c: PointOnObject(g6,g-3)
    c: DistanceX(g6,g6) = 19
    c: PointOnObject(g7,g-3)
    c: DistanceX(g7,g6) = 12
    c: Coincident(g7,g3)
    c: PointOnObject(g8,g-3)
    c: PointOnObject(g8,g-3)
    c: DistanceX(g8,g8) = 10
    c: DistanceX(g8,g6) = 1
    c: Horizontal(g9)
    c: Vertical(g7,g9)
    c: Vertical(g6,g9)
    c: DistanceY(g9,g7) = 8
    c: Horizontal(g10)
    c: Equal(g8,g10)
    c: DistanceY(g10,g8) = 3
    c: Radius(g11) = 20
    c: Coincident(g11,g6)
    c: Coincident(g11,g9)
    c: Radius(g12) = 20
    c: Coincident(g12,g7)
    c: Coincident(g12,g9)
    c: Equal(g13,g11)
    c: Coincident(g13,g8)
    c: Coincident(g13,g10)
    c: Horizontal(g13,g11)
    c: Equal(g14,g12)
    c: Coincident(g14,g8)
    c: Coincident(g14,g10)
    c: Horizontal(g1,g-6)
FEATURE [Sketcher::SketchObject] Sketch122
  ArcFitTolerance = 1e-06
  AttachmentSupport = -> [Pad011]
  ExternalGeometry = -> [Binder001]
  FullyConstrained = true
  MakeInternals = false
  MapMode = 5
  Placement = pos=(0,-2,4e-16) rot=(1,0,0;1.5708rad)
  sketch-geometry (8):
    g0: LineSegment StartX=-202.765 StartY=20.303 StartZ=0 EndX=-143.955 EndY=20.303 EndZ=0
    g1: ArcOfCircle CenterX=-184.801 CenterY=-67.3089 CenterZ=0 NormalX=0 NormalY=0 NormalZ=1 AngleXU=0 Radius=33.7833 StartAngle=2.70526 EndAngle=3.54053
    g2: LineSegment StartX=-176.685 StartY=-80.4316 StartZ=0 EndX=-215.932 EndY=-80.4316 EndZ=0
    g3: LineSegment StartX=-215.42 StartY=-53.0315 StartZ=0 EndX=-192.176 EndY=-3.18454 EndZ=0
    g4: ArcOfCircle CenterX=-207.583 CenterY=4 CenterZ=0 NormalX=0 NormalY=0 NormalZ=1 AngleXU=0 Radius=17 StartAngle=5.84685 EndAngle=7.56663
    g5: Circle CenterX=-213.443 CenterY=-76.8316 CenterZ=0 NormalX=0 NormalY=0 NormalZ=1 AngleXU=0 Radius=3
    g6: Circle CenterX=-179.305 CenterY=-76.8316 CenterZ=0 NormalX=0 NormalY=0 NormalZ=1 AngleXU=0 Radius=3
    g7: LineSegment StartX=-143.955 StartY=20.303 StartZ=0 EndX=-176.685 EndY=-80.4316 EndZ=0
  constraints (18):
    c: Coincident(g0,g-6)
    c: Coincident(g1,g-7)
    c: Coincident(g1,g-8)
    c: Coincident(g2,g1)
    c: Tangent(g3,g-5)
    c: Coincident(g4,g-6)
    c: Coincident(g4,g0)
    c: Coincident(g3,g4)
    c: Coincident(g1,g3)
    c: Diameter(g5) = 6
    c: Diameter(g6) = 6
    c: Coincident(g5,g-9)
    c: Coincident(g6,g-10)
    c: Horizontal(g0)
    c: Horizontal(g2)
    c: Coincident(g7,g0)
    c: Coincident(g7,g2)
    c: Tangent(g7,g-4)
FEATURE [Sketcher::SketchObject] Sketch123
  ArcFitTolerance = 1e-06
  AttachmentSupport = -> [Pad011]
  ExternalGeometry = -> [Binder001]
  FullyConstrained = true
  MakeInternals = false
  MapMode = 5
  Placement = pos=(0,-2,4e-16) rot=(1,0,0;1.5708rad)
  sketch-geometry (4):
    g0: LineSegment StartX=-108 StartY=36.8 StartZ=0 EndX=-90 EndY=36.8 EndZ=0
    g1: LineSegment StartX=-108 StartY=36.8 StartZ=0 EndX=-108 EndY=26.8 EndZ=0
    g2: LineSegment StartX=-108 StartY=26.8 StartZ=0 EndX=-90 EndY=26.8 EndZ=0
    g3: ArcOfCircle CenterX=-94 CenterY=31.8 CenterZ=0 NormalX=0 NormalY=0 NormalZ=1 AngleXU=0 Radius=6.40312 StartAngle=5.38713 EndAngle=7.17924
  constraints (13):
    c: Horizontal(g0)
    c: Coincident(g1,g0)
    c: Vertical(g1)
    c: Coincident(g2,g1)
    c: Horizontal(g2)
    c: DistanceX(g0,g0) = 18
    c: DistanceY(g1,g1) = 10
    c: Equal(g0,g2)
    c: DistanceX(g0,g-3) = 90
    c: DistanceY(g0,g-3) = 2.4
    c: Coincident(g3,g0)
    c: Coincident(g3,g2)
    c: DistanceX(g3,g0) = 4
FEATURE [PartDesign::Pad] Pad017
  BaseFeature = -> Pocket008
  Direction = (0,-1,2e-16)
  Length = 1.6
  Length2 = 10
  Profile = -> Sketch123
  ReferenceAxis = -> Sketch123 [N_Axis]
  Refine = true
  Suppressed = false
  Type = 0
FEATURE [Sketcher::SketchObject] Sketch125
  ArcFitTolerance = 1e-06
  AttachmentSupport = -> [Pad017]
  ExternalGeometry = -> [Pad017]
  FullyConstrained = true
  MakeInternals = false
  MapMode = 5
  Placement = pos=(0,-3.6,8e-16) rot=(1,0,0;1.5708rad)
  sketch-geometry (20):
    g0: LineSegment StartX=-108 StartY=35.8 StartZ=0 EndX=-108 EndY=35 EndZ=0
    g1: LineSegment StartX=-108 StartY=35 StartZ=0 EndX=-97 EndY=35 EndZ=0
    g2: LineSegment StartX=-97 StartY=35 StartZ=0 EndX=-97 EndY=35.8 EndZ=0
    g3: LineSegment StartX=-97 StartY=35.8 StartZ=0 EndX=-108 EndY=35.8 EndZ=0
    g4: LineSegment StartX=-108 StartY=28.6 StartZ=0 EndX=-108 EndY=27.8 EndZ=0
    g5: LineSegment StartX=-108 StartY=27.8 StartZ=0 EndX=-97 EndY=27.8 EndZ=0
    g6: LineSegment StartX=-97 StartY=27.8 StartZ=0 EndX=-97 EndY=28.6 EndZ=0
    g7: LineSegment StartX=-97 StartY=28.6 StartZ=0 EndX=-108 EndY=28.6 EndZ=0
    g8: LineSegment StartX=-108 StartY=30.4 StartZ=0 EndX=-108 EndY=29.6 EndZ=0
    g9: LineSegment StartX=-108 StartY=29.6 StartZ=0 EndX=-97 EndY=29.6 EndZ=0
    g10: LineSegment StartX=-97 StartY=29.6 StartZ=0 EndX=-97 EndY=30.4 EndZ=0
    g11: LineSegment StartX=-97 StartY=30.4 StartZ=0 EndX=-108 EndY=30.4 EndZ=0
    g12: LineSegment StartX=-108 StartY=32.2 StartZ=0 EndX=-108 EndY=31.4 EndZ=0
    g13: LineSegment StartX=-108 StartY=31.4 StartZ=0 EndX=-97 EndY=31.4 EndZ=0
    g14: LineSegment StartX=-97 StartY=31.4 StartZ=0 EndX=-97 EndY=32.2 EndZ=0
    g15: LineSegment StartX=-97 StartY=32.2 StartZ=0 EndX=-108 EndY=32.2 EndZ=0
    g16: LineSegment StartX=-108 StartY=34 StartZ=0 EndX=-108 EndY=33.2 EndZ=0
    g17: LineSegment StartX=-108 StartY=33.2 StartZ=0 EndX=-97 EndY=33.2 EndZ=0
    g18: LineSegment StartX=-97 StartY=33.2 StartZ=0 EndX=-97 EndY=34 EndZ=0
    g19: LineSegment StartX=-97 StartY=34 StartZ=0 EndX=-108 EndY=34 EndZ=0
  constraints (55):
    c: Coincident(g1,g0)
    c: Horizontal(g1)
    c: Coincident(g2,g1)
    c: Vertical(g2)
    c: Coincident(g3,g2)
    c: Horizontal(g3)
    c: Coincident(g3,g0)
    c: DistanceX(g1,g1) = 11
    c: DistanceY(g2,g2) = 0.8
    c: Coincident(g5,g4)
    c: Horizontal(g5)
    c: Coincident(g6,g5)
    c: Vertical(g6)
    c: Coincident(g7,g6)
    c: Horizontal(g7)
    c: Coincident(g7,g4)
    c: Coincident(g9,g8)
    c: Horizontal(g9)
    c: Coincident(g10,g9)
    c: Vertical(g10)
    c: Coincident(g11,g10)
    c: Horizontal(g11)
    c: Coincident(g11,g8)
    c: Coincident(g13,g12)
    c: Horizontal(g13)
    c: Coincident(g14,g13)
    c: Vertical(g14)
    c: Coincident(g15,g14)
    c: Horizontal(g15)
    c: Coincident(g15,g12)
    c: Coincident(g17,g16)
    c: Horizontal(g17)
    c: Coincident(g18,g17)
    c: Vertical(g18)
    c: Coincident(g19,g18)
    c: Horizontal(g19)
    c: Coincident(g19,g16)
    c: Equal(g3,g19)
    c: Equal(g3,g15)
    c: Equal(g3,g11)
    c: Equal(g3,g7)
    c: Equal(g2,g18)
    c: Equal(g2,g14)
    c: Equal(g2,g10)
    c: Equal(g2,g6)
    c: DistanceY(g-4,g4) = 1
    c: DistanceY(g4,g8) = 1
    c: DistanceY(g8,g12) = 1
    c: DistanceY(g12,g16) = 1
    c: DistanceY(g16,g0) = 1
    c: Tangent(g0,g-5)
    c: Tangent(g16,g-5)
    c: Tangent(g12,g-5)
    c: Tangent(g8,g-5)
    c: Tangent(g4,g-5)
FEATURE [PartDesign::Chamfer] Chamfer009
  Angle = 45
  Base = -> Pad017 [Edge147,Edge150]
  BaseFeature = -> Pad017
  ChamferType = 1
  FlipDirection = false
  Refine = true
  Size = 1.5
  Size2 = 2.8
  SupportTransform = false
  Suppressed = false
  UseAllEdges = false
FEATURE [PartDesign::Pocket] Pocket009
  BaseFeature = -> Chamfer009
  Direction = (0,1,-2e-16)
  Length = 1
  Length2 = 5
  Profile = -> Sketch125
  ReferenceAxis = -> Sketch125 [N_Axis]
  Refine = true
  Suppressed = false
  Type = 0
FEATURE [PartDesign::Pad] Pad014
  BaseFeature = -> Pocket009
  Direction = (0,-1,2e-16)
  Length = 0.8
  Length2 = 10
  Profile = -> Sketch120
  ReferenceAxis = -> Sketch120 [N_Axis]
  Refine = true
  Suppressed = false
  Type = 0
FEATURE [Sketcher::SketchObject] Sketch124
  ArcFitTolerance = 1e-06
  AttachmentSupport = -> [Pad014]
  ExternalGeometry = -> [Binder001]
  FullyConstrained = true
  MakeInternals = false
  MapMode = 5
  Placement = pos=(0,-2.8,6e-16) rot=(1,0,0;1.5708rad)
  sketch-geometry (4):
    g0: LineSegment StartX=-129 StartY=39.2 StartZ=0 EndX=-131.599 EndY=31.2 EndZ=0
    g1: LineSegment StartX=-118 StartY=39.2 StartZ=0 EndX=-120.599 EndY=31.2 EndZ=0
    g2: LineSegment StartX=-129 StartY=39.2 StartZ=0 EndX=-118 EndY=39.2 EndZ=0
    g3: LineSegment StartX=-120.599 StartY=31.2 StartZ=0 EndX=-131.599 EndY=31.2 EndZ=0
  constraints (12):
    c: PointOnObject(g0,g-3)
    c: PointOnObject(g1,g-3)
    c: Parallel(g-4,g0)
    c: Parallel(g-4,g1)
    c: Coincident(g2,g0)
    c: Coincident(g2,g1)
    c: DistanceX(g2,g2) = 11
    c: DistanceY(g1,g1) = 8
    c: Coincident(g3,g1)
    c: Horizontal(g3)
    c: Coincident(g3,g0)
    c: DistanceX(g1,g-3) = 118
FEATURE [PartDesign::Pad] Pad018
  BaseFeature = -> Pad014
  Direction = (0,-1,2e-16)
  Length = 1.2
  Length2 = 10
  Profile = -> Sketch124
  ReferenceAxis = -> Sketch124 [N_Axis]
  Refine = true
  Suppressed = false
  Type = 0
FEATURE [Sketcher::SketchObject] Sketch126
  ArcFitTolerance = 1e-06
  AttachmentSupport = -> [Pad018]
  ExternalGeometry = -> [Pad018]
  FullyConstrained = true
  MakeInternals = false
  MapMode = 5
  Placement = pos=(0,-4,0) rot=(1,0,0;1.5708rad)
  sketch-geometry (8):
    g0: LineSegment StartX=-129.877 StartY=36.5 StartZ=0 EndX=-130.137 EndY=35.7 EndZ=0
    g1: LineSegment StartX=-130.69 StartY=34 StartZ=0 EndX=-130.95 EndY=33.2 EndZ=0
    g2: LineSegment StartX=-129.877 StartY=36.5 StartZ=0 EndX=-118.877 EndY=36.5 EndZ=0
    g3: LineSegment StartX=-130.137 StartY=35.7 StartZ=0 EndX=-119.137 EndY=35.7 EndZ=0
    g4: LineSegment StartX=-130.69 StartY=34 StartZ=0 EndX=-119.69 EndY=34 EndZ=0
    g5: LineSegment StartX=-130.95 StartY=33.2 StartZ=0 EndX=-119.95 EndY=33.2 EndZ=0
    g6: LineSegment StartX=-118.877 StartY=36.5 StartZ=0 EndX=-119.137 EndY=35.7 EndZ=0
    g7: LineSegment StartX=-119.69 StartY=34 StartZ=0 EndX=-119.95 EndY=33.2 EndZ=0
  constraints (20):
    c: Coincident(g2,g0)
    c: Horizontal(g2)
    c: Coincident(g3,g0)
    c: Horizontal(g3)
    c: Coincident(g4,g1)
    c: Horizontal(g4)
    c: Coincident(g5,g1)
    c: Horizontal(g5)
    c: Coincident(g6,g2)
    c: Coincident(g6,g3)
    c: Coincident(g7,g4)
    c: Coincident(g7,g5)
    c: Tangent(g0,g-4)
    c: Tangent(g6,g-5)
    c: Tangent(g1,g-4)
    c: Tangent(g7,g-5)
    c: DistanceY(g3,g2) = 0.8
    c: DistanceY(g5,g4) = 0.8
    c: DistanceY(g-6,g1) = 2
    c: DistanceY(g-6,g0) = 4.5
FEATURE [PartDesign::Chamfer] Chamfer008
  Angle = 45
  Base = -> Pad018 [Edge253]
  BaseFeature = -> Pad018
  ChamferType = 1
  FlipDirection = false
  Refine = true
  Size = 1
  Size2 = 6
  SupportTransform = false
  Suppressed = false
  UseAllEdges = false
FEATURE [PartDesign::Pocket] Pocket010
  BaseFeature = -> Chamfer008
  Direction = (0,1,-2e-16)
  Length = 1
  Length2 = 5
  Profile = -> Sketch126
  ReferenceAxis = -> Sketch126 [N_Axis]
  Refine = true
  Suppressed = false
  Type = 0
FEATURE [PartDesign::Pad] Pad015
  BaseFeature = -> Pocket010
  Direction = (0,-1,2e-16)
  Length = 2
  Length2 = 10
  Profile = -> Sketch121
  ReferenceAxis = -> Sketch121 [N_Axis]
  Refine = true
  Suppressed = false
  Type = 0
FEATURE [PartDesign::Pad] Pad016
  BaseFeature = -> Pad015
  Direction = (0,-1,2e-16)
  Length = 1.6
  Length2 = 10
  Profile = -> Sketch122
  ReferenceAxis = -> Sketch122 [N_Axis]
  Refine = true
  Suppressed = false
  Type = 0
FEATURE [Sketcher::SketchObject] Sketch127
  ArcFitTolerance = 1e-06
  AttachmentSupport = -> [Pad016]
  ExternalGeometry = -> [Pad016]
  FullyConstrained = true
  MakeInternals = false
  MapMode = 5
  Placement = pos=(0,0,-80.4316) rot=(1,0,0;3.14159rad)
  sketch-geometry (8):
    g0: LineSegment StartX=-176.685 StartY=3.6 StartZ=0 EndX=-186.685 EndY=3.6 EndZ=0
    g1: LineSegment [constr] StartX=-186.685 StartY=3.6 StartZ=0 EndX=-186.685 EndY=-9e-16 EndZ=0
    g2: LineSegment StartX=-176.685 StartY=3.6 StartZ=0 EndX=-176.685 EndY=0 EndZ=0
    g3: ArcOfEllipse CenterX=-186.685 CenterY=-9e-16 CenterZ=0 NormalX=0 NormalY=0 NormalZ=1 MajorRadius=10 MinorRadius=3.6 AngleXU=1e-16 StartAngle=0 EndAngle=1.5708
    g4: LineSegment [constr] StartX=-176.685 StartY=-2e-15 StartZ=0 EndX=-196.685 EndY=-2e-15 EndZ=0
    g5: LineSegment [constr] StartX=-186.685 StartY=3.6 StartZ=0 EndX=-186.685 EndY=-3.6 EndZ=0
    g6: GeomPoint [constr] X=-177.356 Y=-1e-16 Z=0
    g7: GeomPoint [constr] X=-196.015 Y=-1.9e-15 Z=0
  constraints (13):
    c: Coincident(g0,g-4)
    c: PointOnObject(g0,g-4)
    c: DistanceX(g0,g0) = 10
    c: Coincident(g1,g0)
    c: PointOnObject(g1,g-5)
    c: Vertical(g1)
    c: Coincident(g2,g0)
    c: Coincident(g2,g-5)
    c: InternalAlignment(g4-g7 -> g3) x4
    c: Coincident(g3,g1)
    c: Coincident(g3,g0)
    c: Coincident(g3,g2)
    c: Horizontal(g4)
FEATURE [Sketcher::SketchObject] Sketch128
  ArcFitTolerance = 1e-06
  AttachmentSupport = -> [Pad016]
  ExternalGeometry = -> [Pad016]
  FullyConstrained = true
  MakeInternals = false
  MapMode = 5
  Placement = pos=(0,0,-80.4316) rot=(1,0,0;3.14159rad)
  sketch-geometry (8):
    g0: LineSegment StartX=-215.932 StartY=3.6 StartZ=0 EndX=-215.932 EndY=0 EndZ=0
    g1: LineSegment StartX=-215.932 StartY=3.6 StartZ=0 EndX=-205.932 EndY=3.6 EndZ=0
    g2: LineSegment [constr] StartX=-205.932 StartY=3.6 StartZ=0 EndX=-205.932 EndY=-9e-16 EndZ=0
    g3: ArcOfEllipse CenterX=-205.932 CenterY=-9e-16 CenterZ=0 NormalX=0 NormalY=0 NormalZ=1 MajorRadius=10 MinorRadius=3.6 AngleXU=-3.14159 StartAngle=4.71239 EndAngle=6.28319
    g4: LineSegment [constr] StartX=-215.932 StartY=-1e-15 StartZ=0 EndX=-195.932 EndY=-1e-15 EndZ=0
    g5: LineSegment [constr] StartX=-205.932 StartY=-3.6 StartZ=0 EndX=-205.932 EndY=3.6 EndZ=0
    g6: GeomPoint [constr] X=-215.262 Y=-1e-15 Z=0
    g7: GeomPoint [constr] X=-196.602 Y=-1e-15 Z=0
  constraints (13):
    c: Coincident(g0,g-4)
    c: Coincident(g0,g-5)
    c: Coincident(g1,g0)
    c: PointOnObject(g1,g-3)
    c: DistanceX(g1,g1) = 10
    c: Coincident(g2,g1)
    c: Vertical(g2)
    c: PointOnObject(g2,g-5)
    c: InternalAlignment(g4-g7 -> g3) x4
    c: Coincident(g3,g2)
    c: Coincident(g3,g1)
    c: Coincident(g3,g0)
    c: Horizontal(g4)
FEATURE [PartDesign::SubtractivePipe] SubtractivePipe002
  AuxilleryCurvelinear = true
  AuxillerySpineTangent = false
  BaseFeature = -> Pad016
  Binormal = (0,0,0)
  Mode = 0
  Profile = -> Sketch127
  Refine = true
  Spine = -> Pad016 [Edge280]
  SpineTangent = false
  Suppressed = false
  Transformation = 0
  Transition = 0
FEATURE [PartDesign::SubtractivePipe] SubtractivePipe003
  AuxilleryCurvelinear = true
  AuxillerySpineTangent = false
  BaseFeature = -> SubtractivePipe002
  Binormal = (0,0,0)
  Mode = 0
  Profile = -> Sketch128
  Refine = true
  Spine = -> Pad016 [Edge282,Edge277,Edge278]
  SpineTangent = false
  Suppressed = false
  Transformation = 0
  Transition = 0
FEATURE [Sketcher::SketchObject] Sketch129
  ArcFitTolerance = 1e-06
  AttachmentSupport = -> [Pad016]
  ExternalGeometry = -> [Binder001]
  FullyConstrained = true
  MakeInternals = false
  MapMode = 5
  Placement = pos=(0,-3.6,0) rot=(1,0,0;1.5708rad)
  sketch-geometry (12):
    g0: LineSegment [constr] StartX=-192.176 StartY=-3.18451 StartZ=0 EndX=-181.223 EndY=20.303 EndZ=0
    g1: LineSegment [constr] StartX=-202.765 StartY=20.303 StartZ=0 EndX=-181.223 EndY=20.303 EndZ=0
    g2: LineSegment StartX=-202.765 StartY=20.303 StartZ=0 EndX=-181.223 EndY=20.303 EndZ=0
    g3: LineSegment StartX=-192.176 StartY=-3.18451 StartZ=0 EndX=-196.804 EndY=-13.1107 EndZ=0
    g4: ArcOfCircle CenterX=-207.583 CenterY=4 CenterZ=0 NormalX=0 NormalY=0 NormalZ=1 AngleXU=0 Radius=17 StartAngle=5.84685 EndAngle=7.56663
    g5: ArcOfEllipse CenterX=-181.223 CenterY=8.55923 CenterZ=0 NormalX=0 NormalY=0 NormalZ=1 MajorRadius=23.4779 MinorRadius=11.7437 AngleXU=2e-16 StartAngle=4.71239 EndAngle=7.85398
    g6: LineSegment [constr] StartX=-157.745 StartY=8.55923 StartZ=0 EndX=-204.701 EndY=8.55923 EndZ=0
    g7: LineSegment [constr] StartX=-181.223 StartY=20.303 StartZ=0 EndX=-181.223 EndY=-3.18451 EndZ=0
    g8: GeomPoint [constr] X=-160.894 Y=8.55923 Z=0
    g9: GeomPoint [constr] X=-201.553 Y=8.55923 Z=0
    g10: ArcOfCircle CenterX=-181.223 CenterY=-20.3763 CenterZ=0 NormalX=0 NormalY=0 NormalZ=1 AngleXU=0 Radius=17.1918 StartAngle=1.57079 EndAngle=2.70526
    g11: GeomPoint [constr] X=-181.223 Y=-3.18451 Z=0
  constraints (23):
    c: Coincident(g0,g-5)
    c: Coincident(g1,g-6)
    c: Horizontal(g1)
    c: Coincident(g1,g0)
    c: Parallel(g0,g-4)
    c: Coincident(g2,g1)
    c: Coincident(g2,g0)
    c: Coincident(g3,g0)
    c: Equal(g4,g-5)
    c: Coincident(g4,g1)
    c: Coincident(g4,g0)
    c: InternalAlignment(g6-g9 -> g5) x4
    c: Vertical(g5,g0)
    c: Horizontal(g6)
    c: Coincident(g5,g0)
    c: DistanceX(g6,g-3) = 10.1
    c: Tangent(g10,g3) = -1.5708
    c: PointOnObject(g11,g10)
    c: Tangent(g5,g10,g11) = 1.5708
    c: Coincident(g10,g5)
    c: Coincident(g11,g7)
    c: Parallel(g3,g-4)
    c: Horizontal(g5,g0)
FEATURE [Sketcher::SketchObject] Sketch130
  ArcFitTolerance = 1e-06
  AttachmentOffset = pos=(0,0,-1.6) rot=(0,0,1;0rad)
  AttachmentSupport = -> [Pad016]
  ExternalGeometry = -> [Binder001]
  FullyConstrained = true
  MakeInternals = false
  MapMode = 5
  Placement = pos=(0,-2,-4e-16) rot=(1,0,0;1.5708rad)
  sketch-geometry (12):
    g0: LineSegment [constr] StartX=-192.176 StartY=-3.18451 StartZ=0 EndX=-181.223 EndY=20.303 EndZ=0
    g1: LineSegment [constr] StartX=-202.765 StartY=20.303 StartZ=0 EndX=-181.223 EndY=20.303 EndZ=0
    g2: LineSegment StartX=-202.765 StartY=20.303 StartZ=0 EndX=-181.223 EndY=20.303 EndZ=0
    g3: LineSegment StartX=-192.176 StartY=-3.18451 StartZ=0 EndX=-193.827 EndY=-6.72678 EndZ=0
    g4: ArcOfCircle CenterX=-207.583 CenterY=4 CenterZ=0 NormalX=0 NormalY=0 NormalZ=1 AngleXU=0 Radius=17 StartAngle=5.84685 EndAngle=7.56663
    g5: ArcOfEllipse CenterX=-181.223 CenterY=10.803 CenterZ=0 NormalX=0 NormalY=0 NormalZ=1 MajorRadius=14.4779 MinorRadius=9.5 AngleXU=0 StartAngle=4.71239 EndAngle=7.85398
    g6: LineSegment [constr] StartX=-166.745 StartY=10.803 StartZ=0 EndX=-195.701 EndY=10.803 EndZ=0
    g7: LineSegment [constr] StartX=-181.223 StartY=20.303 StartZ=0 EndX=-181.223 EndY=1.30297 EndZ=0
    g8: GeomPoint [constr] X=-170.298 Y=10.803 Z=0
    g9: GeomPoint [constr] X=-192.148 Y=10.803 Z=0
    g10: ArcOfCircle CenterX=-181.223 CenterY=-12.6042 CenterZ=0 NormalX=0 NormalY=0 NormalZ=1 AngleXU=0 Radius=13.9072 StartAngle=1.5708 EndAngle=2.70526
    g11: GeomPoint [constr] X=-181.223 Y=1.30297 Z=0
  constraints (23):
    c: Coincident(g0,g-5)
    c: Coincident(g1,g-6)
    c: Horizontal(g1)
    c: Coincident(g1,g0)
    c: Parallel(g0,g-4)
    c: Coincident(g2,g1)
    c: Coincident(g2,g0)
    c: Coincident(g3,g0)
    c: Equal(g4,g-5)
    c: Coincident(g4,g1)
    c: Coincident(g4,g0)
    c: InternalAlignment(g6-g9 -> g5) x4
    c: Vertical(g5,g0)
    c: Horizontal(g6)
    c: Coincident(g5,g0)
    c: DistanceX(g6,g-3) = 19.1
    c: Tangent(g10,g3) = -1.5708
    c: PointOnObject(g11,g10)
    c: Tangent(g5,g10,g11) = 1.5708
    c: Coincident(g10,g5)
    c: Coincident(g11,g7)
    c: Parallel(g3,g-4)
    c: DistanceY(g5,g0) = 19
FEATURE [Part::Part2DObjectPython] Clone2D001  label="Sketch130 (2D)"  # Draft 2D object (typed FeaturePython)
  Fuse = false
  Objects = -> [Sketch130]
  Placement = pos=(0,-2,-4e-16) rot=(1,0,0;1.5708rad)
  Scale = (1,1,1)
FEATURE [Sketcher::SketchObject] Sketch131
  ArcFitTolerance = 1e-06
  AttachmentOffset = pos=(0,0,-3.8) rot=(0,0,1;0rad)
  AttachmentSupport = -> [Pad016]
  ExternalGeometry = -> [Binder001]
  FullyConstrained = true
  MakeInternals = false
  MapMode = 5
  Placement = pos=(0,0.2,-8e-16) rot=(1,0,0;1.5708rad)
  sketch-geometry (1):
    g0: GeomPoint X=-197.47 Y=8.55923 Z=0
  constraints (1):
    c: Symmetric(g-6,g-4,g0)
FEATURE [PartDesign::SubtractiveLoft] SubtractiveLoft002
  BaseFeature = -> SubtractivePipe003
  Closed = false
  Profile = -> Sketch129
  Refine = true
  Ruled = false
  Sections = -> [Sketch130]
  Suppressed = false
FEATURE [PartDesign::SubtractiveLoft] SubtractiveLoft003
  BaseFeature = -> SubtractiveLoft002
  Closed = false
  Profile = -> Clone2D001
  Refine = true
  Ruled = false
  Sections = -> [Sketch131]
  Suppressed = false
FEATURE [PartDesign::Chamfer] Chamfer010
  Angle = 45
  Base = -> SubtractiveLoft003 [Edge209,Edge210,Edge212,Edge211,Edge203]
  BaseFeature = -> SubtractiveLoft003
  ChamferType = 0
  FlipDirection = false
  Refine = true
  Size = 1.5
  Size2 = 1
  SupportTransform = false
  Suppressed = false
  UseAllEdges = false
FEATURE [PartDesign::Chamfer] Chamfer011
  Angle = 45
  Base = -> Chamfer010 [Edge10]
  BaseFeature = -> Chamfer010
  ChamferType = 0
  FlipDirection = false
  Refine = true
  Size = 3.5
  Size2 = 1
  SupportTransform = false
  Suppressed = false
  UseAllEdges = false
FEATURE [PartDesign::Chamfer] Chamfer012
  Angle = 45
  Base = -> Chamfer011 [Edge10]
  BaseFeature = -> Chamfer011
  ChamferType = 0
  FlipDirection = false
  Refine = true
  Size = 3.5
  Size2 = 1
  SupportTransform = false
  Suppressed = false
  UseAllEdges = false
FEATURE [PartDesign::Chamfer] Chamfer013
  Angle = 45
  Base = -> Chamfer012 [Edge105,Edge104,Edge103,Edge101,Edge98]
  BaseFeature = -> Chamfer012
  ChamferType = 0
  FlipDirection = false
  Refine = true
  Size = 1.9
  Size2 = 1
  SupportTransform = false
  Suppressed = false
  UseAllEdges = false
FEATURE [PartDesign::Fillet] Fillet008
  Base = -> Chamfer013 [Edge203,Edge218,Edge88]
  BaseFeature = -> Chamfer013
  Radius = 1.1
  Refine = true
  SupportTransform = false
  Suppressed = false
  UseAllEdges = false
FEATURE [Sketcher::SketchObject] Sketch132
  ArcFitTolerance = 1e-06
  AttachmentSupport = -> [Pad016]
  ExternalGeometry = -> [Binder001]
  FullyConstrained = true
  MakeInternals = false
  MapMode = 5
  Placement = pos=(0,-3.6,0) rot=(1,0,0;1.5708rad)
  sketch-geometry (3):
    g0: LineSegment [constr] StartX=-215.42 StartY=-53.0314 StartZ=0 EndX=-167.782 EndY=-53.0314 EndZ=0
    g1: Circle CenterX=-191.282 CenterY=-53.0314 CenterZ=0 NormalX=0 NormalY=0 NormalZ=1 AngleXU=0 Radius=11.5
    g2: Circle CenterX=-191.282 CenterY=-53.0314 CenterZ=0 NormalX=0 NormalY=0 NormalZ=1 AngleXU=0 Radius=10.7
  constraints (8):
    c: Coincident(g0,g-3)
    c: PointOnObject(g0,g-4)
    c: Horizontal(g0)
    c: Diameter(g1) = 23
    c: PointOnObject(g1,g0)
    c: DistanceX(g1,g0) = 23.5
    c: Diameter(g2) = 21.4
    c: Coincident(g2,g1)
FEATURE [PartDesign::Fillet] Fillet009
  Base = -> Fillet008 [Edge24]
  BaseFeature = -> Fillet008
  Radius = 1.9
  Refine = true
  SupportTransform = false
  Suppressed = false
  UseAllEdges = false
FEATURE [PartDesign::Pocket] Pocket011
  BaseFeature = -> Fillet009
  Direction = (0,1,-2e-16)
  Length = 0.8
  Length2 = 5
  Profile = -> Sketch132
  ReferenceAxis = -> Sketch132 [N_Axis]
  Refine = true
  Suppressed = false
  Type = 0
FEATURE [PartDesign::Body] Body007  label="lato DX"
  AllowCompound = false
  Group = -> [Binder001,Sketch114,Pad011,Sketch115,Pocket006,Sketch116,Pad012,Sketch117,Pocket007,Sketch118,Pad013,Sketch119,Pocket008,Pad017,Chamfer009,Pocket009,Sketch123,Sketch120,Pad014,Pad018,Chamfer008,Pocket010,Sketch121,Pad015,Sketch122,Pad016,Sketch124,Sketch125,Sketch126,Sketch127,Sketch128,SubtractivePipe002,SubtractivePipe003,Sketch129,Sketch130,Clone2D001,Sketch131,SubtractiveLoft002,+9 more]
  Origin = -> Origin007
  Tip = -> Pocket011
